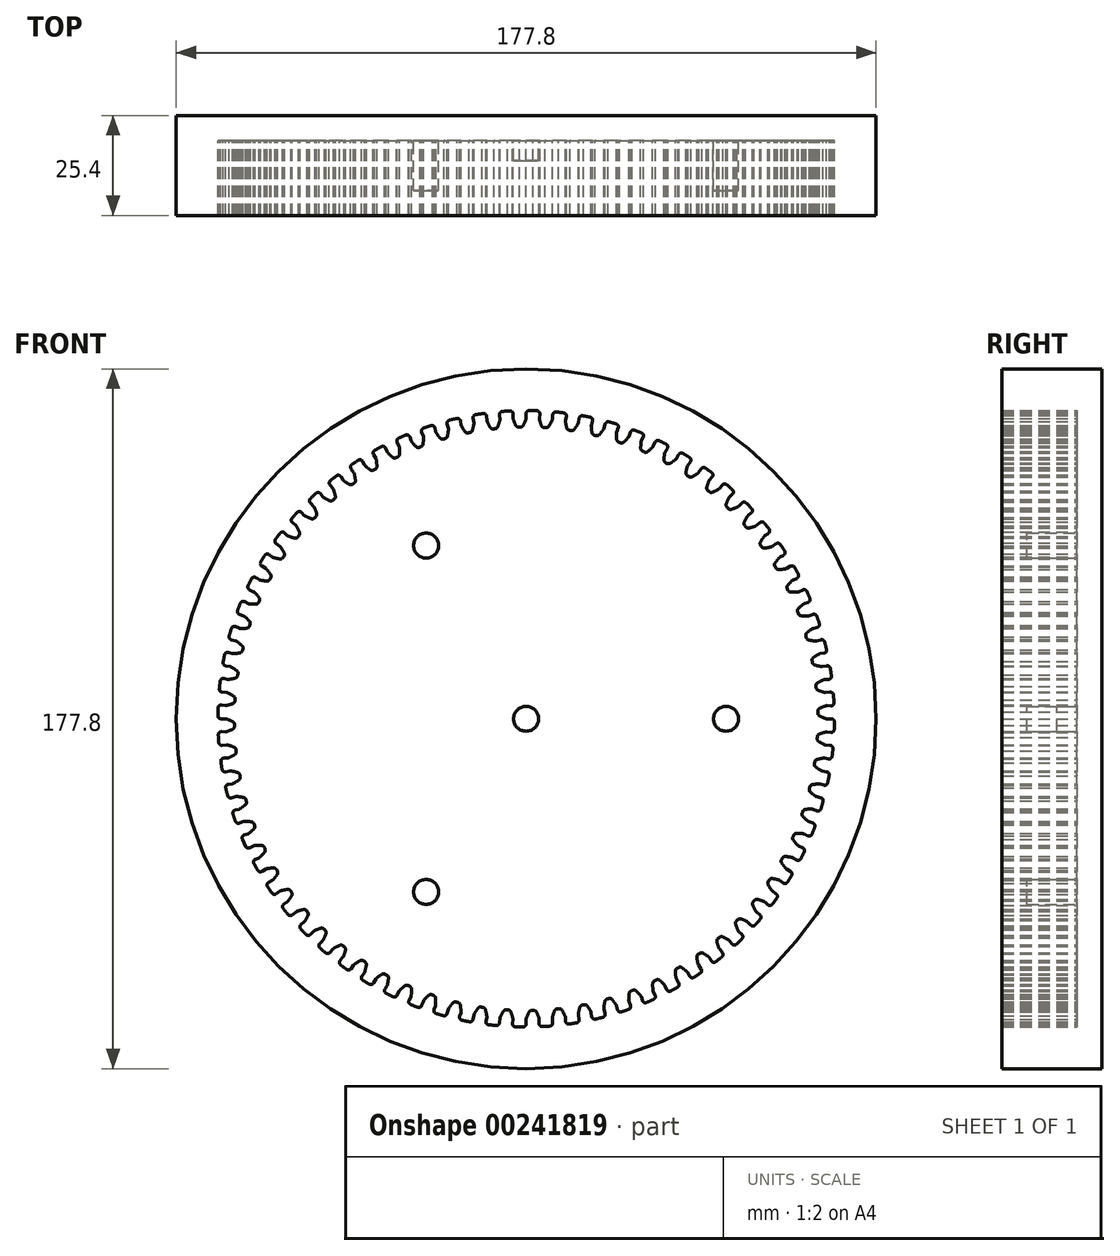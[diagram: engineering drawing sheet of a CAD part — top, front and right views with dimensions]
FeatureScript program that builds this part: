
annotation { "Feature Type Name" : "Feature", "Feature Type Description" : "" }
export const myFeature = defineFeature(function(context is Context, id is Id, definition is map)
    precondition{}
    {
        {
            var Q0;
            Q0=qCreatedBy(makeId("Front.planeOp"),FACE);
            var sketch = newSketch(context, id + "F0", { "sketchPlane" : qUnion([Q0])});
            skArc(sketch, "E0", {"start": v(-4.1, 78.2) * mm, "mid": v(-5.07, 78.15) * mm, "end": v(-6.03, 78.08) * mm});
            skArc(sketch, "E1.MirrorCS", {"start": v(-0.05, 76.06) * mm, "mid": v(-0.38, 75.29) * mm, "end": v(-0.74, 74.53) * mm});
            skLineSegment(sketch, "E2.MirrorCS", {"start": v(0, 76.35) * mm, "end": v(0, 77.53) * mm});
            skLineSegment(sketch, "E3.MirrorCS", {"start": v(-1.45, 74.1) * mm, "end": v(-1.7, 74.1) * mm});
            skLineSegment(sketch, "E4.MirrorCS", {"start": v(-1.97, 74.1) * mm, "end": v(-1.7, 74.1) * mm});
            skArc(sketch, "E5.MirrorCS", {"start": v(-3.28, 76.13) * mm, "mid": v(-2.99, 75.34) * mm, "end": v(-2.66, 74.57) * mm});
            skLineSegment(sketch, "E6.MirrorCS", {"start": v(-3.32, 76.42) * mm, "end": v(-3.28, 77.39) * mm});
            skPoint(sketch, "E7.end.orphan", {"position": v(-1.7, 78.3) * mm});
            skPoint(sketch, "E7.start.orphan", {"position": v(-0.96, 78.31) * mm});
            skPoint(sketch, "E8.MirrorCS.start.orphan", {"position": v(-2.45, 78.28) * mm});
            skPoint(sketch, "E9.orphan", {"position": v(-3.32, 76.13) * mm});
            skPoint(sketch, "E10.MirrorCS.end.orphan", {"position": v(-3.2, 73.49) * mm});
            skPoint(sketch, "E11.end.orphan", {"position": v(0, 73.56) * mm});
            skPoint(sketch, "E12.orphan", {"position": v(-3.2, 78.91) * mm});
            skPoint(sketch, "E13.orphan", {"position": v(0, 78.84) * mm});
            skPoint(sketch, "E14.start.orphan", {"position": v(0, 76.2) * mm});
            skPoint(sketch, "E15.visualSharp", {"position": v(-2.45, 74.12) * mm});
            skArc(sketch, "E15.filletArc", {"start": v(-2.48, 74.18) * mm, "mid": v(-2.44, 74.14) * mm, "end": v(-2.4, 74.12) * mm});
            skArc(sketch, "E16.filletArc", {"start": v(-0.05, 76.06) * mm, "mid": v(-0.01, 76.2) * mm, "end": v(0, 76.35) * mm});
            skPoint(sketch, "E17.visualSharp", {"position": v(-3.32, 76.27) * mm});
            skArc(sketch, "E17.filletArc", {"start": v(-3.32, 76.42) * mm, "mid": v(-3.3, 76.27) * mm, "end": v(-3.28, 76.13) * mm});
            skPoint(sketch, "E18.visualSharp", {"position": v(-0.96, 74.09) * mm});
            skArc(sketch, "E18.filletArc", {"start": v(-1.45, 74.1) * mm, "mid": v(-1.03, 74.21) * mm, "end": v(-0.74, 74.53) * mm});
            skArc(sketch, "E19.filletArc", {"start": v(-2.66, 74.57) * mm, "mid": v(-2.38, 74.24) * mm, "end": v(-1.97, 74.1) * mm});
            skPoint(sketch, "E20.visualSharp", {"position": v(-3.24, 78.25) * mm});
            skArc(sketch, "E20.filletArc", {"start": v(-3.28, 77.39) * mm, "mid": v(-3.5, 77.98) * mm, "end": v(-4.1, 78.2) * mm});
            skPoint(sketch, "E21.visualSharp", {"position": v(0, 78.32) * mm});
            skArc(sketch, "E21.filletArc", {"start": v(0.8, 78.31) * mm, "mid": v(0.23, 78.08) * mm, "end": v(0, 77.53) * mm});
            skCircle(sketch, "E22", {"center": v(0, 0) * mm, "radius": 88.9 * mm});
            skArc(sketch, "E23.1.0", {"start": v(-10, 76.8) * mm, "mid": v(-10.3, 77.38) * mm, "end": v(-10.9, 77.55) * mm});
            skLineSegment(sketch, "E23.1.1", {"start": v(-9.97, 75.84) * mm, "end": v(-10, 76.8) * mm});
            skArc(sketch, "E23.1.2", {"start": v(-9.97, 75.84) * mm, "mid": v(-9.94, 75.7) * mm, "end": v(-9.9, 75.55) * mm});
            skArc(sketch, "E23.1.3", {"start": v(-9.9, 75.55) * mm, "mid": v(-9.54, 74.8) * mm, "end": v(-9.15, 74.06) * mm});
            skArc(sketch, "E23.1.4", {"start": v(-9.15, 74.06) * mm, "mid": v(-8.84, 73.75) * mm, "end": v(-8.42, 73.65) * mm});
            skLineSegment(sketch, "E23.1.5", {"start": v(-8.42, 73.65) * mm, "end": v(-8.16, 73.67) * mm});
            skLineSegment(sketch, "E23.1.6", {"start": v(-7.9, 73.69) * mm, "end": v(-8.16, 73.67) * mm});
            skArc(sketch, "E23.1.7", {"start": v(-7.9, 73.69) * mm, "mid": v(-7.5, 73.84) * mm, "end": v(-7.23, 74.18) * mm});
            skArc(sketch, "E23.1.8", {"start": v(-6.68, 75.77) * mm, "mid": v(-6.94, 74.97) * mm, "end": v(-7.23, 74.18) * mm});
            skArc(sketch, "E23.1.9", {"start": v(-6.68, 75.77) * mm, "mid": v(-6.66, 75.9) * mm, "end": v(-6.65, 76.06) * mm});
            skLineSegment(sketch, "E23.1.10", {"start": v(-6.65, 76.06) * mm, "end": v(-6.76, 77.23) * mm});
            skArc(sketch, "E23.1.11", {"start": v(-6.03, 78.08) * mm, "mid": v(-6.57, 77.8) * mm, "end": v(-6.76, 77.23) * mm});
            skArc(sketch, "E23.2.0", {"start": v(-16.66, 75.64) * mm, "mid": v(-17, 76.19) * mm, "end": v(-17.62, 76.3) * mm});
            skLineSegment(sketch, "E23.2.1", {"start": v(-16.54, 74.68) * mm, "end": v(-16.66, 75.64) * mm});
            skArc(sketch, "E23.2.2", {"start": v(-16.54, 74.68) * mm, "mid": v(-16.5, 74.54) * mm, "end": v(-16.45, 74.4) * mm});
            skArc(sketch, "E23.2.3", {"start": v(-16.45, 74.4) * mm, "mid": v(-16.02, 73.68) * mm, "end": v(-15.57, 72.98) * mm});
            skArc(sketch, "E23.2.4", {"start": v(-15.57, 72.98) * mm, "mid": v(-15.24, 72.7) * mm, "end": v(-14.8, 72.64) * mm});
            skLineSegment(sketch, "E23.2.5", {"start": v(-14.8, 72.64) * mm, "end": v(-14.55, 72.68) * mm});
            skLineSegment(sketch, "E23.2.6", {"start": v(-14.3, 72.72) * mm, "end": v(-14.55, 72.68) * mm});
            skArc(sketch, "E23.2.7", {"start": v(-14.3, 72.72) * mm, "mid": v(-13.9, 72.9) * mm, "end": v(-13.67, 73.27) * mm});
            skArc(sketch, "E23.2.8", {"start": v(-13.26, 74.9) * mm, "mid": v(-13.45, 74.08) * mm, "end": v(-13.67, 73.27) * mm});
            skArc(sketch, "E23.2.9", {"start": v(-13.26, 74.9) * mm, "mid": v(-13.25, 75.04) * mm, "end": v(-13.26, 75.19) * mm});
            skLineSegment(sketch, "E23.2.10", {"start": v(-13.26, 75.19) * mm, "end": v(-13.46, 76.35) * mm});
            skArc(sketch, "E23.2.11", {"start": v(-12.82, 77.26) * mm, "mid": v(-13.33, 76.94) * mm, "end": v(-13.46, 76.35) * mm});
            skArc(sketch, "E23.3.0", {"start": v(-23.2, 73.9) * mm, "mid": v(-23.57, 74.42) * mm, "end": v(-24.2, 74.48) * mm});
            skLineSegment(sketch, "E23.3.1", {"start": v(-22.98, 72.96) * mm, "end": v(-23.2, 73.9) * mm});
            skArc(sketch, "E23.3.2", {"start": v(-22.98, 72.96) * mm, "mid": v(-22.94, 72.82) * mm, "end": v(-22.87, 72.69) * mm});
            skArc(sketch, "E23.3.3", {"start": v(-22.87, 72.69) * mm, "mid": v(-22.38, 72) * mm, "end": v(-21.87, 71.34) * mm});
            skArc(sketch, "E23.3.4", {"start": v(-21.87, 71.34) * mm, "mid": v(-21.52, 71.1) * mm, "end": v(-21.08, 71.07) * mm});
            skLineSegment(sketch, "E23.3.5", {"start": v(-21.08, 71.07) * mm, "end": v(-20.83, 71.13) * mm});
            skLineSegment(sketch, "E23.3.6", {"start": v(-20.58, 71.2) * mm, "end": v(-20.83, 71.13) * mm});
            skArc(sketch, "E23.3.7", {"start": v(-20.58, 71.2) * mm, "mid": v(-20.2, 71.42) * mm, "end": v(-20, 71.8) * mm});
            skArc(sketch, "E23.3.8", {"start": v(-19.74, 73.45) * mm, "mid": v(-19.85, 72.62) * mm, "end": v(-20, 71.8) * mm});
            skArc(sketch, "E23.3.9", {"start": v(-19.74, 73.45) * mm, "mid": v(-19.74, 73.6) * mm, "end": v(-19.76, 73.75) * mm});
            skLineSegment(sketch, "E23.3.10", {"start": v(-19.76, 73.75) * mm, "end": v(-20.07, 74.88) * mm});
            skArc(sketch, "E23.3.11", {"start": v(-19.5, 75.85) * mm, "mid": v(-19.98, 75.48) * mm, "end": v(-20.07, 74.88) * mm});
            skArc(sketch, "E23.4.0", {"start": v(-29.55, 71.6) * mm, "mid": v(-29.97, 72.08) * mm, "end": v(-30.6, 72.09) * mm});
            skLineSegment(sketch, "E23.4.1", {"start": v(-29.25, 70.68) * mm, "end": v(-29.55, 71.6) * mm});
            skArc(sketch, "E23.4.2", {"start": v(-29.25, 70.68) * mm, "mid": v(-29.2, 70.54) * mm, "end": v(-29.12, 70.42) * mm});
            skArc(sketch, "E23.4.3", {"start": v(-29.12, 70.42) * mm, "mid": v(-28.57, 69.78) * mm, "end": v(-28, 69.17) * mm});
            skArc(sketch, "E23.4.4", {"start": v(-28, 69.17) * mm, "mid": v(-27.63, 68.95) * mm, "end": v(-27.2, 68.96) * mm});
            skLineSegment(sketch, "E23.4.5", {"start": v(-27.2, 68.96) * mm, "end": v(-26.95, 69.05) * mm});
            skLineSegment(sketch, "E23.4.6", {"start": v(-26.7, 69.13) * mm, "end": v(-26.95, 69.05) * mm});
            skArc(sketch, "E23.4.7", {"start": v(-26.7, 69.13) * mm, "mid": v(-26.35, 69.38) * mm, "end": v(-26.18, 69.78) * mm});
            skArc(sketch, "E23.4.8", {"start": v(-26.07, 71.45) * mm, "mid": v(-26.1, 70.62) * mm, "end": v(-26.18, 69.78) * mm});
            skArc(sketch, "E23.4.9", {"start": v(-26.07, 71.45) * mm, "mid": v(-26.08, 71.6) * mm, "end": v(-26.11, 71.74) * mm});
            skLineSegment(sketch, "E23.4.10", {"start": v(-26.11, 71.74) * mm, "end": v(-26.52, 72.85) * mm});
            skArc(sketch, "E23.4.11", {"start": v(-26.04, 73.86) * mm, "mid": v(-26.49, 73.46) * mm, "end": v(-26.52, 72.85) * mm});
            skArc(sketch, "E23.5.0", {"start": v(-35.67, 68.75) * mm, "mid": v(-36.14, 69.2) * mm, "end": v(-36.77, 69.15) * mm});
            skLineSegment(sketch, "E23.5.1", {"start": v(-35.3, 67.86) * mm, "end": v(-35.67, 68.75) * mm});
            skArc(sketch, "E23.5.2", {"start": v(-35.3, 67.86) * mm, "mid": v(-35.23, 67.73) * mm, "end": v(-35.14, 67.61) * mm});
            skArc(sketch, "E23.5.3", {"start": v(-35.14, 67.61) * mm, "mid": v(-34.55, 67.02) * mm, "end": v(-33.93, 66.46) * mm});
            skArc(sketch, "E23.5.4", {"start": v(-33.93, 66.46) * mm, "mid": v(-33.53, 66.28) * mm, "end": v(-33.1, 66.33) * mm});
            skLineSegment(sketch, "E23.5.5", {"start": v(-33.1, 66.33) * mm, "end": v(-32.86, 66.43) * mm});
            skLineSegment(sketch, "E23.5.6", {"start": v(-32.63, 66.54) * mm, "end": v(-32.86, 66.43) * mm});
            skArc(sketch, "E23.5.7", {"start": v(-32.63, 66.54) * mm, "mid": v(-32.3, 66.82) * mm, "end": v(-32.16, 67.24) * mm});
            skArc(sketch, "E23.5.8", {"start": v(-32.2, 68.91) * mm, "mid": v(-32.16, 68.07) * mm, "end": v(-32.16, 67.24) * mm});
            skArc(sketch, "E23.5.9", {"start": v(-32.2, 68.91) * mm, "mid": v(-32.22, 69.06) * mm, "end": v(-32.27, 69.2) * mm});
            skLineSegment(sketch, "E23.5.10", {"start": v(-32.27, 69.2) * mm, "end": v(-32.76, 70.26) * mm});
            skArc(sketch, "E23.5.11", {"start": v(-32.38, 71.31) * mm, "mid": v(-32.79, 70.87) * mm, "end": v(-32.76, 70.26) * mm});
            skArc(sketch, "E23.6.0", {"start": v(-41.53, 65.38) * mm, "mid": v(-42.03, 65.78) * mm, "end": v(-42.66, 65.68) * mm});
            skLineSegment(sketch, "E23.6.1", {"start": v(-41.08, 64.52) * mm, "end": v(-41.53, 65.38) * mm});
            skArc(sketch, "E23.6.2", {"start": v(-41.08, 64.52) * mm, "mid": v(-41, 64.4) * mm, "end": v(-40.9, 64.3) * mm});
            skArc(sketch, "E23.6.3", {"start": v(-40.9, 64.3) * mm, "mid": v(-40.26, 63.76) * mm, "end": v(-39.6, 63.25) * mm});
            skArc(sketch, "E23.6.4", {"start": v(-39.6, 63.25) * mm, "mid": v(-39.18, 63.1) * mm, "end": v(-38.76, 63.2) * mm});
            skLineSegment(sketch, "E23.6.5", {"start": v(-38.76, 63.2) * mm, "end": v(-38.53, 63.32) * mm});
            skLineSegment(sketch, "E23.6.6", {"start": v(-38.3, 63.44) * mm, "end": v(-38.53, 63.32) * mm});
            skArc(sketch, "E23.6.7", {"start": v(-38.3, 63.44) * mm, "mid": v(-38, 63.75) * mm, "end": v(-37.9, 64.18) * mm});
            skArc(sketch, "E23.6.8", {"start": v(-38.08, 65.84) * mm, "mid": v(-37.97, 65.01) * mm, "end": v(-37.9, 64.18) * mm});
            skArc(sketch, "E23.6.9", {"start": v(-38.08, 65.84) * mm, "mid": v(-38.11, 65.99) * mm, "end": v(-38.17, 66.12) * mm});
            skLineSegment(sketch, "E23.6.10", {"start": v(-38.17, 66.12) * mm, "end": v(-38.76, 67.14) * mm});
            skArc(sketch, "E23.6.11", {"start": v(-38.47, 68.22) * mm, "mid": v(-38.84, 67.74) * mm, "end": v(-38.76, 67.14) * mm});
            skArc(sketch, "E23.7.0", {"start": v(-47.07, 61.51) * mm, "mid": v(-47.6, 61.87) * mm, "end": v(-48.22, 61.71) * mm});
            skLineSegment(sketch, "E23.7.1", {"start": v(-46.55, 60.7) * mm, "end": v(-47.07, 61.51) * mm});
            skArc(sketch, "E23.7.2", {"start": v(-46.55, 60.7) * mm, "mid": v(-46.46, 60.58) * mm, "end": v(-46.35, 60.48) * mm});
            skArc(sketch, "E23.7.3", {"start": v(-46.35, 60.48) * mm, "mid": v(-45.66, 60) * mm, "end": v(-44.95, 59.56) * mm});
            skArc(sketch, "E23.7.4", {"start": v(-44.95, 59.56) * mm, "mid": v(-44.53, 59.45) * mm, "end": v(-44.12, 59.58) * mm});
            skLineSegment(sketch, "E23.7.5", {"start": v(-44.12, 59.58) * mm, "end": v(-43.9, 59.72) * mm});
            skLineSegment(sketch, "E23.7.6", {"start": v(-43.69, 59.86) * mm, "end": v(-43.9, 59.72) * mm});
            skArc(sketch, "E23.7.7", {"start": v(-43.69, 59.86) * mm, "mid": v(-43.4, 60.2) * mm, "end": v(-43.35, 60.63) * mm});
            skArc(sketch, "E23.7.8", {"start": v(-43.67, 62.27) * mm, "mid": v(-43.5, 61.46) * mm, "end": v(-43.35, 60.63) * mm});
            skArc(sketch, "E23.7.9", {"start": v(-43.67, 62.27) * mm, "mid": v(-43.72, 62.41) * mm, "end": v(-43.8, 62.54) * mm});
            skLineSegment(sketch, "E23.7.10", {"start": v(-43.8, 62.54) * mm, "end": v(-44.47, 63.5) * mm});
            skArc(sketch, "E23.7.11", {"start": v(-44.27, 64.6) * mm, "mid": v(-44.6, 64.1) * mm, "end": v(-44.47, 63.5) * mm});
            skArc(sketch, "E23.8.0", {"start": v(-52.25, 57.18) * mm, "mid": v(-52.81, 57.48) * mm, "end": v(-53.41, 57.27) * mm});
            skLineSegment(sketch, "E23.8.1", {"start": v(-51.66, 56.4) * mm, "end": v(-52.25, 57.18) * mm});
            skArc(sketch, "E23.8.2", {"start": v(-51.66, 56.4) * mm, "mid": v(-51.56, 56.3) * mm, "end": v(-51.44, 56.21) * mm});
            skArc(sketch, "E23.8.3", {"start": v(-51.44, 56.21) * mm, "mid": v(-50.72, 55.8) * mm, "end": v(-49.97, 55.42) * mm});
            skArc(sketch, "E23.8.4", {"start": v(-49.97, 55.42) * mm, "mid": v(-49.54, 55.34) * mm, "end": v(-49.14, 55.5) * mm});
            skLineSegment(sketch, "E23.8.5", {"start": v(-49.14, 55.5) * mm, "end": v(-48.94, 55.66) * mm});
            skLineSegment(sketch, "E23.8.6", {"start": v(-48.74, 55.83) * mm, "end": v(-48.94, 55.66) * mm});
            skArc(sketch, "E23.8.7", {"start": v(-48.74, 55.83) * mm, "mid": v(-48.5, 56.19) * mm, "end": v(-48.47, 56.62) * mm});
            skArc(sketch, "E23.8.8", {"start": v(-48.93, 58.23) * mm, "mid": v(-48.68, 57.43) * mm, "end": v(-48.47, 56.62) * mm});
            skArc(sketch, "E23.8.9", {"start": v(-48.93, 58.23) * mm, "mid": v(-49, 58.36) * mm, "end": v(-49.08, 58.49) * mm});
            skLineSegment(sketch, "E23.8.10", {"start": v(-49.08, 58.49) * mm, "end": v(-49.83, 59.39) * mm});
            skArc(sketch, "E23.8.11", {"start": v(-49.73, 60.5) * mm, "mid": v(-50.01, 59.97) * mm, "end": v(-49.83, 59.39) * mm});
            skArc(sketch, "E23.9.0", {"start": v(-57.04, 52.4) * mm, "mid": v(-57.62, 52.66) * mm, "end": v(-58.2, 52.4) * mm});
            skLineSegment(sketch, "E23.9.1", {"start": v(-56.38, 51.7) * mm, "end": v(-57.04, 52.4) * mm});
            skArc(sketch, "E23.9.2", {"start": v(-56.38, 51.7) * mm, "mid": v(-56.27, 51.6) * mm, "end": v(-56.15, 51.52) * mm});
            skArc(sketch, "E23.9.3", {"start": v(-56.15, 51.52) * mm, "mid": v(-55.39, 51.17) * mm, "end": v(-54.61, 50.85) * mm});
            skArc(sketch, "E23.9.4", {"start": v(-54.61, 50.85) * mm, "mid": v(-54.18, 50.81) * mm, "end": v(-53.8, 51.01) * mm});
            skLineSegment(sketch, "E23.9.5", {"start": v(-53.8, 51.01) * mm, "end": v(-53.6, 51.19) * mm});
            skLineSegment(sketch, "E23.9.6", {"start": v(-53.42, 51.37) * mm, "end": v(-53.6, 51.19) * mm});
            skArc(sketch, "E23.9.7", {"start": v(-53.42, 51.37) * mm, "mid": v(-53.2, 51.75) * mm, "end": v(-53.22, 52.18) * mm});
            skArc(sketch, "E23.9.8", {"start": v(-53.82, 53.74) * mm, "mid": v(-53.5, 52.97) * mm, "end": v(-53.22, 52.18) * mm});
            skArc(sketch, "E23.9.9", {"start": v(-53.82, 53.74) * mm, "mid": v(-53.9, 53.87) * mm, "end": v(-53.99, 53.99) * mm});
            skLineSegment(sketch, "E23.9.10", {"start": v(-53.99, 53.99) * mm, "end": v(-54.82, 54.82) * mm});
            skArc(sketch, "E23.9.11", {"start": v(-54.81, 55.94) * mm, "mid": v(-55.05, 55.38) * mm, "end": v(-54.82, 54.82) * mm});
            skArc(sketch, "E23.10.0", {"start": v(-61.39, 47.24) * mm, "mid": v(-62, 47.44) * mm, "end": v(-62.55, 47.13) * mm});
            skLineSegment(sketch, "E23.10.1", {"start": v(-60.67, 46.58) * mm, "end": v(-61.39, 47.24) * mm});
            skArc(sketch, "E23.10.2", {"start": v(-60.67, 46.58) * mm, "mid": v(-60.56, 46.5) * mm, "end": v(-60.42, 46.43) * mm});
            skArc(sketch, "E23.10.3", {"start": v(-60.42, 46.43) * mm, "mid": v(-59.64, 46.14) * mm, "end": v(-58.84, 45.9) * mm});
            skArc(sketch, "E23.10.4", {"start": v(-58.84, 45.9) * mm, "mid": v(-58.4, 45.9) * mm, "end": v(-58.03, 46.13) * mm});
            skLineSegment(sketch, "E23.10.5", {"start": v(-58.03, 46.13) * mm, "end": v(-57.86, 46.32) * mm});
            skLineSegment(sketch, "E23.10.6", {"start": v(-57.7, 46.52) * mm, "end": v(-57.86, 46.32) * mm});
            skArc(sketch, "E23.10.7", {"start": v(-57.7, 46.52) * mm, "mid": v(-57.51, 46.91) * mm, "end": v(-57.57, 47.34) * mm});
            skArc(sketch, "E23.10.8", {"start": v(-58.3, 48.85) * mm, "mid": v(-57.92, 48.1) * mm, "end": v(-57.57, 47.34) * mm});
            skArc(sketch, "E23.10.9", {"start": v(-58.3, 48.85) * mm, "mid": v(-58.38, 48.97) * mm, "end": v(-58.49, 49.08) * mm});
            skLineSegment(sketch, "E23.10.10", {"start": v(-58.49, 49.08) * mm, "end": v(-59.39, 49.83) * mm});
            skArc(sketch, "E23.10.11", {"start": v(-59.48, 50.95) * mm, "mid": v(-59.67, 50.37) * mm, "end": v(-59.39, 49.83) * mm});
            skArc(sketch, "E23.11.0", {"start": v(-65.27, 41.7) * mm, "mid": v(-65.9, 41.86) * mm, "end": v(-66.42, 41.5) * mm});
            skLineSegment(sketch, "E23.11.1", {"start": v(-64.5, 41.12) * mm, "end": v(-65.27, 41.7) * mm});
            skArc(sketch, "E23.11.2", {"start": v(-64.5, 41.12) * mm, "mid": v(-64.38, 41.04) * mm, "end": v(-64.24, 40.98) * mm});
            skArc(sketch, "E23.11.3", {"start": v(-64.24, 40.98) * mm, "mid": v(-63.43, 40.77) * mm, "end": v(-62.61, 40.6) * mm});
            skArc(sketch, "E23.11.4", {"start": v(-62.61, 40.6) * mm, "mid": v(-62.18, 40.63) * mm, "end": v(-61.83, 40.9) * mm});
            skLineSegment(sketch, "E23.11.5", {"start": v(-61.83, 40.9) * mm, "end": v(-61.68, 41.1) * mm});
            skLineSegment(sketch, "E23.11.6", {"start": v(-61.53, 41.31) * mm, "end": v(-61.68, 41.1) * mm});
            skArc(sketch, "E23.11.7", {"start": v(-61.53, 41.31) * mm, "mid": v(-61.38, 41.72) * mm, "end": v(-61.47, 42.15) * mm});
            skArc(sketch, "E23.11.8", {"start": v(-62.34, 43.58) * mm, "mid": v(-61.89, 42.87) * mm, "end": v(-61.47, 42.15) * mm});
            skArc(sketch, "E23.11.9", {"start": v(-62.34, 43.58) * mm, "mid": v(-62.43, 43.7) * mm, "end": v(-62.54, 43.8) * mm});
            skLineSegment(sketch, "E23.11.10", {"start": v(-62.54, 43.8) * mm, "end": v(-63.5, 44.47) * mm});
            skArc(sketch, "E23.11.11", {"start": v(-63.7, 45.57) * mm, "mid": v(-63.83, 44.98) * mm, "end": v(-63.5, 44.47) * mm});
            skArc(sketch, "E23.12.0", {"start": v(-68.66, 35.86) * mm, "mid": v(-69.29, 35.95) * mm, "end": v(-69.78, 35.55) * mm});
            skLineSegment(sketch, "E23.12.1", {"start": v(-67.84, 35.34) * mm, "end": v(-68.66, 35.86) * mm});
            skArc(sketch, "E23.12.2", {"start": v(-67.84, 35.34) * mm, "mid": v(-67.7, 35.27) * mm, "end": v(-67.57, 35.23) * mm});
            skArc(sketch, "E23.12.3", {"start": v(-67.57, 35.23) * mm, "mid": v(-66.74, 35.09) * mm, "end": v(-65.91, 34.98) * mm});
            skArc(sketch, "E23.12.4", {"start": v(-65.91, 34.98) * mm, "mid": v(-65.48, 35.06) * mm, "end": v(-65.16, 35.35) * mm});
            skLineSegment(sketch, "E23.12.5", {"start": v(-65.16, 35.35) * mm, "end": v(-65.03, 35.57) * mm});
            skLineSegment(sketch, "E23.12.6", {"start": v(-64.9, 35.8) * mm, "end": v(-65.03, 35.57) * mm});
            skArc(sketch, "E23.12.7", {"start": v(-64.9, 35.8) * mm, "mid": v(-64.78, 36.21) * mm, "end": v(-64.91, 36.63) * mm});
            skArc(sketch, "E23.12.8", {"start": v(-65.9, 37.98) * mm, "mid": v(-65.4, 37.32) * mm, "end": v(-64.91, 36.63) * mm});
            skArc(sketch, "E23.12.9", {"start": v(-65.9, 37.98) * mm, "mid": v(-66, 38.09) * mm, "end": v(-66.12, 38.17) * mm});
            skLineSegment(sketch, "E23.12.10", {"start": v(-66.12, 38.17) * mm, "end": v(-67.14, 38.76) * mm});
            skArc(sketch, "E23.12.11", {"start": v(-67.42, 39.85) * mm, "mid": v(-67.5, 39.24) * mm, "end": v(-67.14, 38.76) * mm});
            skArc(sketch, "E23.13.0", {"start": v(-71.52, 29.74) * mm, "mid": v(-72.16, 29.78) * mm, "end": v(-72.62, 29.33) * mm});
            skLineSegment(sketch, "E23.13.1", {"start": v(-70.66, 29.3) * mm, "end": v(-71.52, 29.74) * mm});
            skArc(sketch, "E23.13.2", {"start": v(-70.66, 29.3) * mm, "mid": v(-70.53, 29.23) * mm, "end": v(-70.38, 29.2) * mm});
            skArc(sketch, "E23.13.3", {"start": v(-70.38, 29.2) * mm, "mid": v(-69.55, 29.14) * mm, "end": v(-68.71, 29.1) * mm});
            skArc(sketch, "E23.13.4", {"start": v(-68.71, 29.1) * mm, "mid": v(-68.3, 29.22) * mm, "end": v(-68, 29.54) * mm});
            skLineSegment(sketch, "E23.13.5", {"start": v(-68, 29.54) * mm, "end": v(-67.88, 29.77) * mm});
            skLineSegment(sketch, "E23.13.6", {"start": v(-67.77, 30) * mm, "end": v(-67.88, 29.77) * mm});
            skArc(sketch, "E23.13.7", {"start": v(-67.77, 30) * mm, "mid": v(-67.7, 30.43) * mm, "end": v(-67.86, 30.83) * mm});
            skArc(sketch, "E23.13.8", {"start": v(-68.96, 32.1) * mm, "mid": v(-68.4, 31.48) * mm, "end": v(-67.86, 30.83) * mm});
            skArc(sketch, "E23.13.9", {"start": v(-68.96, 32.1) * mm, "mid": v(-69.07, 32.2) * mm, "end": v(-69.2, 32.27) * mm});
            skLineSegment(sketch, "E23.13.10", {"start": v(-69.2, 32.27) * mm, "end": v(-70.26, 32.76) * mm});
            skArc(sketch, "E23.13.11", {"start": v(-70.64, 33.82) * mm, "mid": v(-70.67, 33.21) * mm, "end": v(-70.26, 32.76) * mm});
            skArc(sketch, "E23.14.0", {"start": v(-73.84, 23.4) * mm, "mid": v(-74.48, 23.38) * mm, "end": v(-74.9, 22.9) * mm});
            skLineSegment(sketch, "E23.14.1", {"start": v(-72.95, 23.02) * mm, "end": v(-73.84, 23.4) * mm});
            skArc(sketch, "E23.14.2", {"start": v(-72.95, 23.02) * mm, "mid": v(-72.8, 22.98) * mm, "end": v(-72.66, 22.96) * mm});
            skArc(sketch, "E23.14.3", {"start": v(-72.66, 22.96) * mm, "mid": v(-71.82, 22.96) * mm, "end": v(-70.99, 23) * mm});
            skArc(sketch, "E23.14.4", {"start": v(-70.99, 23) * mm, "mid": v(-70.58, 23.15) * mm, "end": v(-70.31, 23.5) * mm});
            skLineSegment(sketch, "E23.14.5", {"start": v(-70.31, 23.5) * mm, "end": v(-70.21, 23.74) * mm});
            skLineSegment(sketch, "E23.14.6", {"start": v(-70.12, 23.98) * mm, "end": v(-70.21, 23.74) * mm});
            skArc(sketch, "E23.14.7", {"start": v(-70.12, 23.98) * mm, "mid": v(-70.09, 24.41) * mm, "end": v(-70.29, 24.8) * mm});
            skArc(sketch, "E23.14.8", {"start": v(-71.5, 25.96) * mm, "mid": v(-70.88, 25.4) * mm, "end": v(-70.29, 24.8) * mm});
            skArc(sketch, "E23.14.9", {"start": v(-71.5, 25.96) * mm, "mid": v(-71.61, 26.05) * mm, "end": v(-71.74, 26.11) * mm});
            skLineSegment(sketch, "E23.14.10", {"start": v(-71.74, 26.11) * mm, "end": v(-72.85, 26.52) * mm});
            skArc(sketch, "E23.14.11", {"start": v(-73.32, 27.53) * mm, "mid": v(-73.3, 26.93) * mm, "end": v(-72.85, 26.52) * mm});
            skArc(sketch, "E23.15.0", {"start": v(-75.6, 16.87) * mm, "mid": v(-76.23, 16.8) * mm, "end": v(-76.6, 16.28) * mm});
            skLineSegment(sketch, "E23.15.1", {"start": v(-74.67, 16.57) * mm, "end": v(-75.6, 16.87) * mm});
            skArc(sketch, "E23.15.2", {"start": v(-74.67, 16.57) * mm, "mid": v(-74.53, 16.54) * mm, "end": v(-74.38, 16.54) * mm});
            skArc(sketch, "E23.15.3", {"start": v(-74.38, 16.54) * mm, "mid": v(-73.55, 16.62) * mm, "end": v(-72.72, 16.73) * mm});
            skArc(sketch, "E23.15.4", {"start": v(-72.72, 16.73) * mm, "mid": v(-72.33, 16.91) * mm, "end": v(-72.1, 17.28) * mm});
            skLineSegment(sketch, "E23.15.5", {"start": v(-72.1, 17.28) * mm, "end": v(-72.02, 17.53) * mm});
            skLineSegment(sketch, "E23.15.6", {"start": v(-71.95, 17.78) * mm, "end": v(-72.02, 17.53) * mm});
            skArc(sketch, "E23.15.7", {"start": v(-71.95, 17.78) * mm, "mid": v(-71.95, 18.21) * mm, "end": v(-72.18, 18.58) * mm});
            skArc(sketch, "E23.15.8", {"start": v(-73.48, 19.63) * mm, "mid": v(-72.82, 19.12) * mm, "end": v(-72.18, 18.58) * mm});
            skArc(sketch, "E23.15.9", {"start": v(-73.48, 19.63) * mm, "mid": v(-73.6, 19.7) * mm, "end": v(-73.75, 19.76) * mm});
            skLineSegment(sketch, "E23.15.10", {"start": v(-73.75, 19.76) * mm, "end": v(-74.88, 20.07) * mm});
            skArc(sketch, "E23.15.11", {"start": v(-75.44, 21.04) * mm, "mid": v(-75.36, 20.44) * mm, "end": v(-74.88, 20.07) * mm});
            skArc(sketch, "E23.16.0", {"start": v(-76.78, 10.21) * mm, "mid": v(-77.4, 10.09) * mm, "end": v(-77.73, 9.54) * mm});
            skLineSegment(sketch, "E23.16.1", {"start": v(-75.84, 10) * mm, "end": v(-76.78, 10.21) * mm});
            skArc(sketch, "E23.16.2", {"start": v(-75.84, 10) * mm, "mid": v(-75.69, 9.98) * mm, "end": v(-75.54, 10) * mm});
            skArc(sketch, "E23.16.3", {"start": v(-75.54, 10) * mm, "mid": v(-74.72, 10.14) * mm, "end": v(-73.9, 10.33) * mm});
            skArc(sketch, "E23.16.4", {"start": v(-73.9, 10.33) * mm, "mid": v(-73.53, 10.55) * mm, "end": v(-73.32, 10.93) * mm});
            skLineSegment(sketch, "E23.16.5", {"start": v(-73.32, 10.93) * mm, "end": v(-73.27, 11.18) * mm});
            skLineSegment(sketch, "E23.16.6", {"start": v(-73.22, 11.44) * mm, "end": v(-73.27, 11.18) * mm});
            skArc(sketch, "E23.16.7", {"start": v(-73.22, 11.44) * mm, "mid": v(-73.26, 11.87) * mm, "end": v(-73.53, 12.22) * mm});
            skArc(sketch, "E23.16.8", {"start": v(-74.91, 13.15) * mm, "mid": v(-74.2, 12.7) * mm, "end": v(-73.53, 12.22) * mm});
            skArc(sketch, "E23.16.9", {"start": v(-74.91, 13.15) * mm, "mid": v(-75.05, 13.22) * mm, "end": v(-75.19, 13.26) * mm});
            skLineSegment(sketch, "E23.16.10", {"start": v(-75.19, 13.26) * mm, "end": v(-76.35, 13.46) * mm});
            skArc(sketch, "E23.16.11", {"start": v(-76.98, 14.38) * mm, "mid": v(-76.86, 13.79) * mm, "end": v(-76.35, 13.46) * mm});
            skArc(sketch, "E23.17.0", {"start": v(-77.38, 3.48) * mm, "mid": v(-78, 3.3) * mm, "end": v(-78.27, 2.73) * mm});
            skLineSegment(sketch, "E23.17.1", {"start": v(-76.42, 3.36) * mm, "end": v(-77.38, 3.48) * mm});
            skArc(sketch, "E23.17.2", {"start": v(-76.42, 3.36) * mm, "mid": v(-76.27, 3.35) * mm, "end": v(-76.13, 3.37) * mm});
            skArc(sketch, "E23.17.3", {"start": v(-76.13, 3.37) * mm, "mid": v(-75.32, 3.6) * mm, "end": v(-74.52, 3.85) * mm});
            skArc(sketch, "E23.17.4", {"start": v(-74.52, 3.85) * mm, "mid": v(-74.16, 4.1) * mm, "end": v(-74, 4.5) * mm});
            skLineSegment(sketch, "E23.17.5", {"start": v(-74, 4.5) * mm, "end": v(-73.97, 4.76) * mm});
            skLineSegment(sketch, "E23.17.6", {"start": v(-73.94, 5.01) * mm, "end": v(-73.97, 4.76) * mm});
            skArc(sketch, "E23.17.7", {"start": v(-73.94, 5.01) * mm, "mid": v(-74.02, 5.44) * mm, "end": v(-74.31, 5.76) * mm});
            skArc(sketch, "E23.17.8", {"start": v(-75.77, 6.57) * mm, "mid": v(-75.03, 6.18) * mm, "end": v(-74.31, 5.76) * mm});
            skArc(sketch, "E23.17.9", {"start": v(-75.77, 6.57) * mm, "mid": v(-75.91, 6.63) * mm, "end": v(-76.06, 6.65) * mm});
            skLineSegment(sketch, "E23.17.10", {"start": v(-76.06, 6.65) * mm, "end": v(-77.23, 6.76) * mm});
            skArc(sketch, "E23.17.11", {"start": v(-77.95, 7.62) * mm, "mid": v(-77.77, 7.04) * mm, "end": v(-77.23, 6.76) * mm});
            skArc(sketch, "E23.18.0", {"start": v(-77.39, -3.28) * mm, "mid": v(-77.98, -3.5) * mm, "end": v(-78.2, -4.1) * mm});
            skLineSegment(sketch, "E23.18.1", {"start": v(-76.42, -3.32) * mm, "end": v(-77.39, -3.28) * mm});
            skArc(sketch, "E23.18.2", {"start": v(-76.42, -3.32) * mm, "mid": v(-76.27, -3.3) * mm, "end": v(-76.13, -3.28) * mm});
            skArc(sketch, "E23.18.3", {"start": v(-76.13, -3.28) * mm, "mid": v(-75.34, -2.99) * mm, "end": v(-74.57, -2.66) * mm});
            skArc(sketch, "E23.18.4", {"start": v(-74.57, -2.66) * mm, "mid": v(-74.24, -2.38) * mm, "end": v(-74.1, -1.97) * mm});
            skLineSegment(sketch, "E23.18.5", {"start": v(-74.1, -1.97) * mm, "end": v(-74.1, -1.7) * mm});
            skLineSegment(sketch, "E23.18.6", {"start": v(-74.1, -1.45) * mm, "end": v(-74.1, -1.7) * mm});
            skArc(sketch, "E23.18.7", {"start": v(-74.1, -1.45) * mm, "mid": v(-74.21, -1.03) * mm, "end": v(-74.53, -0.74) * mm});
            skArc(sketch, "E23.18.8", {"start": v(-76.06, -0.05) * mm, "mid": v(-75.29, -0.38) * mm, "end": v(-74.53, -0.74) * mm});
            skArc(sketch, "E23.18.9", {"start": v(-76.06, -0.05) * mm, "mid": v(-76.2, -0.01) * mm, "end": v(-76.35, 0) * mm});
            skLineSegment(sketch, "E23.18.10", {"start": v(-76.35, 0) * mm, "end": v(-77.53, 0) * mm});
            skArc(sketch, "E23.18.11", {"start": v(-78.31, 0.8) * mm, "mid": v(-78.08, 0.23) * mm, "end": v(-77.53, 0) * mm});
            skArc(sketch, "E23.19.0", {"start": v(-76.8, -10) * mm, "mid": v(-77.38, -10.3) * mm, "end": v(-77.55, -10.9) * mm});
            skLineSegment(sketch, "E23.19.1", {"start": v(-75.84, -9.97) * mm, "end": v(-76.8, -10) * mm});
            skArc(sketch, "E23.19.2", {"start": v(-75.84, -9.97) * mm, "mid": v(-75.7, -9.94) * mm, "end": v(-75.55, -9.9) * mm});
            skArc(sketch, "E23.19.3", {"start": v(-75.55, -9.9) * mm, "mid": v(-74.8, -9.54) * mm, "end": v(-74.06, -9.15) * mm});
            skArc(sketch, "E23.19.4", {"start": v(-74.06, -9.15) * mm, "mid": v(-73.75, -8.84) * mm, "end": v(-73.65, -8.42) * mm});
            skLineSegment(sketch, "E23.19.5", {"start": v(-73.65, -8.42) * mm, "end": v(-73.67, -8.16) * mm});
            skLineSegment(sketch, "E23.19.6", {"start": v(-73.69, -7.9) * mm, "end": v(-73.67, -8.16) * mm});
            skArc(sketch, "E23.19.7", {"start": v(-73.69, -7.9) * mm, "mid": v(-73.84, -7.5) * mm, "end": v(-74.18, -7.23) * mm});
            skArc(sketch, "E23.19.8", {"start": v(-75.77, -6.68) * mm, "mid": v(-74.97, -6.94) * mm, "end": v(-74.18, -7.23) * mm});
            skArc(sketch, "E23.19.9", {"start": v(-75.77, -6.68) * mm, "mid": v(-75.9, -6.66) * mm, "end": v(-76.06, -6.65) * mm});
            skLineSegment(sketch, "E23.19.10", {"start": v(-76.06, -6.65) * mm, "end": v(-77.23, -6.76) * mm});
            skArc(sketch, "E23.19.11", {"start": v(-78.08, -6.03) * mm, "mid": v(-77.8, -6.57) * mm, "end": v(-77.23, -6.76) * mm});
            skArc(sketch, "E23.20.0", {"start": v(-75.64, -16.66) * mm, "mid": v(-76.19, -17) * mm, "end": v(-76.3, -17.62) * mm});
            skLineSegment(sketch, "E23.20.1", {"start": v(-74.68, -16.54) * mm, "end": v(-75.64, -16.66) * mm});
            skArc(sketch, "E23.20.2", {"start": v(-74.68, -16.54) * mm, "mid": v(-74.54, -16.5) * mm, "end": v(-74.4, -16.45) * mm});
            skArc(sketch, "E23.20.3", {"start": v(-74.4, -16.45) * mm, "mid": v(-73.68, -16.02) * mm, "end": v(-72.98, -15.57) * mm});
            skArc(sketch, "E23.20.4", {"start": v(-72.98, -15.57) * mm, "mid": v(-72.7, -15.24) * mm, "end": v(-72.64, -14.8) * mm});
            skLineSegment(sketch, "E23.20.5", {"start": v(-72.64, -14.8) * mm, "end": v(-72.68, -14.55) * mm});
            skLineSegment(sketch, "E23.20.6", {"start": v(-72.72, -14.3) * mm, "end": v(-72.68, -14.55) * mm});
            skArc(sketch, "E23.20.7", {"start": v(-72.72, -14.3) * mm, "mid": v(-72.9, -13.9) * mm, "end": v(-73.27, -13.67) * mm});
            skArc(sketch, "E23.20.8", {"start": v(-74.9, -13.26) * mm, "mid": v(-74.08, -13.45) * mm, "end": v(-73.27, -13.67) * mm});
            skArc(sketch, "E23.20.9", {"start": v(-74.9, -13.26) * mm, "mid": v(-75.04, -13.25) * mm, "end": v(-75.19, -13.26) * mm});
            skLineSegment(sketch, "E23.20.10", {"start": v(-75.19, -13.26) * mm, "end": v(-76.35, -13.46) * mm});
            skArc(sketch, "E23.20.11", {"start": v(-77.26, -12.82) * mm, "mid": v(-76.94, -13.33) * mm, "end": v(-76.35, -13.46) * mm});
            skArc(sketch, "E23.21.0", {"start": v(-73.9, -23.2) * mm, "mid": v(-74.42, -23.57) * mm, "end": v(-74.48, -24.2) * mm});
            skLineSegment(sketch, "E23.21.1", {"start": v(-72.96, -22.98) * mm, "end": v(-73.9, -23.2) * mm});
            skArc(sketch, "E23.21.2", {"start": v(-72.96, -22.98) * mm, "mid": v(-72.82, -22.94) * mm, "end": v(-72.69, -22.87) * mm});
            skArc(sketch, "E23.21.3", {"start": v(-72.69, -22.87) * mm, "mid": v(-72, -22.38) * mm, "end": v(-71.34, -21.87) * mm});
            skArc(sketch, "E23.21.4", {"start": v(-71.34, -21.87) * mm, "mid": v(-71.1, -21.52) * mm, "end": v(-71.07, -21.08) * mm});
            skLineSegment(sketch, "E23.21.5", {"start": v(-71.07, -21.08) * mm, "end": v(-71.13, -20.83) * mm});
            skLineSegment(sketch, "E23.21.6", {"start": v(-71.2, -20.58) * mm, "end": v(-71.13, -20.83) * mm});
            skArc(sketch, "E23.21.7", {"start": v(-71.2, -20.58) * mm, "mid": v(-71.42, -20.2) * mm, "end": v(-71.8, -20) * mm});
            skArc(sketch, "E23.21.8", {"start": v(-73.45, -19.74) * mm, "mid": v(-72.62, -19.85) * mm, "end": v(-71.8, -20) * mm});
            skArc(sketch, "E23.21.9", {"start": v(-73.45, -19.74) * mm, "mid": v(-73.6, -19.74) * mm, "end": v(-73.75, -19.76) * mm});
            skLineSegment(sketch, "E23.21.10", {"start": v(-73.75, -19.76) * mm, "end": v(-74.88, -20.07) * mm});
            skArc(sketch, "E23.21.11", {"start": v(-75.85, -19.5) * mm, "mid": v(-75.48, -19.98) * mm, "end": v(-74.88, -20.07) * mm});
            skArc(sketch, "E23.22.0", {"start": v(-71.6, -29.55) * mm, "mid": v(-72.08, -29.97) * mm, "end": v(-72.09, -30.6) * mm});
            skLineSegment(sketch, "E23.22.1", {"start": v(-70.68, -29.25) * mm, "end": v(-71.6, -29.55) * mm});
            skArc(sketch, "E23.22.2", {"start": v(-70.68, -29.25) * mm, "mid": v(-70.54, -29.2) * mm, "end": v(-70.42, -29.12) * mm});
            skArc(sketch, "E23.22.3", {"start": v(-70.42, -29.12) * mm, "mid": v(-69.78, -28.57) * mm, "end": v(-69.17, -28) * mm});
            skArc(sketch, "E23.22.4", {"start": v(-69.17, -28) * mm, "mid": v(-68.95, -27.63) * mm, "end": v(-68.96, -27.2) * mm});
            skLineSegment(sketch, "E23.22.5", {"start": v(-68.96, -27.2) * mm, "end": v(-69.05, -26.95) * mm});
            skLineSegment(sketch, "E23.22.6", {"start": v(-69.13, -26.7) * mm, "end": v(-69.05, -26.95) * mm});
            skArc(sketch, "E23.22.7", {"start": v(-69.13, -26.7) * mm, "mid": v(-69.38, -26.35) * mm, "end": v(-69.78, -26.18) * mm});
            skArc(sketch, "E23.22.8", {"start": v(-71.45, -26.07) * mm, "mid": v(-70.62, -26.1) * mm, "end": v(-69.78, -26.18) * mm});
            skArc(sketch, "E23.22.9", {"start": v(-71.45, -26.07) * mm, "mid": v(-71.6, -26.08) * mm, "end": v(-71.74, -26.11) * mm});
            skLineSegment(sketch, "E23.22.10", {"start": v(-71.74, -26.11) * mm, "end": v(-72.85, -26.52) * mm});
            skArc(sketch, "E23.22.11", {"start": v(-73.86, -26.04) * mm, "mid": v(-73.46, -26.49) * mm, "end": v(-72.85, -26.52) * mm});
            skArc(sketch, "E23.23.0", {"start": v(-68.75, -35.67) * mm, "mid": v(-69.2, -36.14) * mm, "end": v(-69.15, -36.77) * mm});
            skLineSegment(sketch, "E23.23.1", {"start": v(-67.86, -35.3) * mm, "end": v(-68.75, -35.67) * mm});
            skArc(sketch, "E23.23.2", {"start": v(-67.86, -35.3) * mm, "mid": v(-67.73, -35.23) * mm, "end": v(-67.61, -35.14) * mm});
            skArc(sketch, "E23.23.3", {"start": v(-67.61, -35.14) * mm, "mid": v(-67.02, -34.55) * mm, "end": v(-66.46, -33.93) * mm});
            skArc(sketch, "E23.23.4", {"start": v(-66.46, -33.93) * mm, "mid": v(-66.28, -33.53) * mm, "end": v(-66.33, -33.1) * mm});
            skLineSegment(sketch, "E23.23.5", {"start": v(-66.33, -33.1) * mm, "end": v(-66.43, -32.86) * mm});
            skLineSegment(sketch, "E23.23.6", {"start": v(-66.54, -32.63) * mm, "end": v(-66.43, -32.86) * mm});
            skArc(sketch, "E23.23.7", {"start": v(-66.54, -32.63) * mm, "mid": v(-66.82, -32.3) * mm, "end": v(-67.24, -32.16) * mm});
            skArc(sketch, "E23.23.8", {"start": v(-68.91, -32.2) * mm, "mid": v(-68.07, -32.16) * mm, "end": v(-67.24, -32.16) * mm});
            skArc(sketch, "E23.23.9", {"start": v(-68.91, -32.2) * mm, "mid": v(-69.06, -32.22) * mm, "end": v(-69.2, -32.27) * mm});
            skLineSegment(sketch, "E23.23.10", {"start": v(-69.2, -32.27) * mm, "end": v(-70.26, -32.76) * mm});
            skArc(sketch, "E23.23.11", {"start": v(-71.31, -32.38) * mm, "mid": v(-70.87, -32.79) * mm, "end": v(-70.26, -32.76) * mm});
            skArc(sketch, "E23.24.0", {"start": v(-65.38, -41.53) * mm, "mid": v(-65.78, -42.03) * mm, "end": v(-65.68, -42.66) * mm});
            skLineSegment(sketch, "E23.24.1", {"start": v(-64.52, -41.08) * mm, "end": v(-65.38, -41.53) * mm});
            skArc(sketch, "E23.24.2", {"start": v(-64.52, -41.08) * mm, "mid": v(-64.4, -41) * mm, "end": v(-64.3, -40.9) * mm});
            skArc(sketch, "E23.24.3", {"start": v(-64.3, -40.9) * mm, "mid": v(-63.76, -40.26) * mm, "end": v(-63.25, -39.6) * mm});
            skArc(sketch, "E23.24.4", {"start": v(-63.25, -39.6) * mm, "mid": v(-63.1, -39.18) * mm, "end": v(-63.2, -38.76) * mm});
            skLineSegment(sketch, "E23.24.5", {"start": v(-63.2, -38.76) * mm, "end": v(-63.32, -38.53) * mm});
            skLineSegment(sketch, "E23.24.6", {"start": v(-63.44, -38.3) * mm, "end": v(-63.32, -38.53) * mm});
            skArc(sketch, "E23.24.7", {"start": v(-63.44, -38.3) * mm, "mid": v(-63.75, -38) * mm, "end": v(-64.18, -37.9) * mm});
            skArc(sketch, "E23.24.8", {"start": v(-65.84, -38.08) * mm, "mid": v(-65.01, -37.97) * mm, "end": v(-64.18, -37.9) * mm});
            skArc(sketch, "E23.24.9", {"start": v(-65.84, -38.08) * mm, "mid": v(-65.99, -38.11) * mm, "end": v(-66.12, -38.17) * mm});
            skLineSegment(sketch, "E23.24.10", {"start": v(-66.12, -38.17) * mm, "end": v(-67.14, -38.76) * mm});
            skArc(sketch, "E23.24.11", {"start": v(-68.22, -38.47) * mm, "mid": v(-67.74, -38.84) * mm, "end": v(-67.14, -38.76) * mm});
            skArc(sketch, "E23.25.0", {"start": v(-61.51, -47.07) * mm, "mid": v(-61.87, -47.6) * mm, "end": v(-61.71, -48.22) * mm});
            skLineSegment(sketch, "E23.25.1", {"start": v(-60.7, -46.55) * mm, "end": v(-61.51, -47.07) * mm});
            skArc(sketch, "E23.25.2", {"start": v(-60.7, -46.55) * mm, "mid": v(-60.58, -46.46) * mm, "end": v(-60.48, -46.35) * mm});
            skArc(sketch, "E23.25.3", {"start": v(-60.48, -46.35) * mm, "mid": v(-60, -45.66) * mm, "end": v(-59.56, -44.95) * mm});
            skArc(sketch, "E23.25.4", {"start": v(-59.56, -44.95) * mm, "mid": v(-59.45, -44.53) * mm, "end": v(-59.58, -44.12) * mm});
            skLineSegment(sketch, "E23.25.5", {"start": v(-59.58, -44.12) * mm, "end": v(-59.72, -43.9) * mm});
            skLineSegment(sketch, "E23.25.6", {"start": v(-59.86, -43.69) * mm, "end": v(-59.72, -43.9) * mm});
            skArc(sketch, "E23.25.7", {"start": v(-59.86, -43.69) * mm, "mid": v(-60.2, -43.4) * mm, "end": v(-60.63, -43.35) * mm});
            skArc(sketch, "E23.25.8", {"start": v(-62.27, -43.67) * mm, "mid": v(-61.46, -43.5) * mm, "end": v(-60.63, -43.35) * mm});
            skArc(sketch, "E23.25.9", {"start": v(-62.27, -43.67) * mm, "mid": v(-62.41, -43.72) * mm, "end": v(-62.54, -43.8) * mm});
            skLineSegment(sketch, "E23.25.10", {"start": v(-62.54, -43.8) * mm, "end": v(-63.5, -44.47) * mm});
            skArc(sketch, "E23.25.11", {"start": v(-64.6, -44.27) * mm, "mid": v(-64.1, -44.6) * mm, "end": v(-63.5, -44.47) * mm});
            skArc(sketch, "E23.26.0", {"start": v(-57.18, -52.25) * mm, "mid": v(-57.48, -52.81) * mm, "end": v(-57.27, -53.41) * mm});
            skLineSegment(sketch, "E23.26.1", {"start": v(-56.4, -51.66) * mm, "end": v(-57.18, -52.25) * mm});
            skArc(sketch, "E23.26.2", {"start": v(-56.4, -51.66) * mm, "mid": v(-56.3, -51.56) * mm, "end": v(-56.21, -51.44) * mm});
            skArc(sketch, "E23.26.3", {"start": v(-56.21, -51.44) * mm, "mid": v(-55.8, -50.72) * mm, "end": v(-55.42, -49.97) * mm});
            skArc(sketch, "E23.26.4", {"start": v(-55.42, -49.97) * mm, "mid": v(-55.34, -49.54) * mm, "end": v(-55.5, -49.14) * mm});
            skLineSegment(sketch, "E23.26.5", {"start": v(-55.5, -49.14) * mm, "end": v(-55.66, -48.94) * mm});
            skLineSegment(sketch, "E23.26.6", {"start": v(-55.83, -48.74) * mm, "end": v(-55.66, -48.94) * mm});
            skArc(sketch, "E23.26.7", {"start": v(-55.83, -48.74) * mm, "mid": v(-56.19, -48.5) * mm, "end": v(-56.62, -48.47) * mm});
            skArc(sketch, "E23.26.8", {"start": v(-58.23, -48.93) * mm, "mid": v(-57.43, -48.68) * mm, "end": v(-56.62, -48.47) * mm});
            skArc(sketch, "E23.26.9", {"start": v(-58.23, -48.93) * mm, "mid": v(-58.36, -49) * mm, "end": v(-58.49, -49.08) * mm});
            skLineSegment(sketch, "E23.26.10", {"start": v(-58.49, -49.08) * mm, "end": v(-59.39, -49.83) * mm});
            skArc(sketch, "E23.26.11", {"start": v(-60.5, -49.73) * mm, "mid": v(-59.97, -50.01) * mm, "end": v(-59.39, -49.83) * mm});
            skArc(sketch, "E23.27.0", {"start": v(-52.4, -57.04) * mm, "mid": v(-52.66, -57.62) * mm, "end": v(-52.4, -58.2) * mm});
            skLineSegment(sketch, "E23.27.1", {"start": v(-51.7, -56.38) * mm, "end": v(-52.4, -57.04) * mm});
            skArc(sketch, "E23.27.2", {"start": v(-51.7, -56.38) * mm, "mid": v(-51.6, -56.27) * mm, "end": v(-51.52, -56.15) * mm});
            skArc(sketch, "E23.27.3", {"start": v(-51.52, -56.15) * mm, "mid": v(-51.17, -55.39) * mm, "end": v(-50.85, -54.61) * mm});
            skArc(sketch, "E23.27.4", {"start": v(-50.85, -54.61) * mm, "mid": v(-50.81, -54.18) * mm, "end": v(-51.01, -53.8) * mm});
            skLineSegment(sketch, "E23.27.5", {"start": v(-51.01, -53.8) * mm, "end": v(-51.19, -53.6) * mm});
            skLineSegment(sketch, "E23.27.6", {"start": v(-51.37, -53.42) * mm, "end": v(-51.19, -53.6) * mm});
            skArc(sketch, "E23.27.7", {"start": v(-51.37, -53.42) * mm, "mid": v(-51.75, -53.2) * mm, "end": v(-52.18, -53.22) * mm});
            skArc(sketch, "E23.27.8", {"start": v(-53.74, -53.82) * mm, "mid": v(-52.97, -53.5) * mm, "end": v(-52.18, -53.22) * mm});
            skArc(sketch, "E23.27.9", {"start": v(-53.74, -53.82) * mm, "mid": v(-53.87, -53.9) * mm, "end": v(-53.99, -53.99) * mm});
            skLineSegment(sketch, "E23.27.10", {"start": v(-53.99, -53.99) * mm, "end": v(-54.82, -54.82) * mm});
            skArc(sketch, "E23.27.11", {"start": v(-55.94, -54.81) * mm, "mid": v(-55.38, -55.05) * mm, "end": v(-54.82, -54.82) * mm});
            skArc(sketch, "E23.28.0", {"start": v(-47.24, -61.39) * mm, "mid": v(-47.44, -62) * mm, "end": v(-47.13, -62.55) * mm});
            skLineSegment(sketch, "E23.28.1", {"start": v(-46.58, -60.67) * mm, "end": v(-47.24, -61.39) * mm});
            skArc(sketch, "E23.28.2", {"start": v(-46.58, -60.67) * mm, "mid": v(-46.5, -60.56) * mm, "end": v(-46.43, -60.42) * mm});
            skArc(sketch, "E23.28.3", {"start": v(-46.43, -60.42) * mm, "mid": v(-46.14, -59.64) * mm, "end": v(-45.9, -58.84) * mm});
            skArc(sketch, "E23.28.4", {"start": v(-45.9, -58.84) * mm, "mid": v(-45.9, -58.4) * mm, "end": v(-46.13, -58.03) * mm});
            skLineSegment(sketch, "E23.28.5", {"start": v(-46.13, -58.03) * mm, "end": v(-46.32, -57.86) * mm});
            skLineSegment(sketch, "E23.28.6", {"start": v(-46.52, -57.7) * mm, "end": v(-46.32, -57.86) * mm});
            skArc(sketch, "E23.28.7", {"start": v(-46.52, -57.7) * mm, "mid": v(-46.91, -57.51) * mm, "end": v(-47.34, -57.57) * mm});
            skArc(sketch, "E23.28.8", {"start": v(-48.85, -58.3) * mm, "mid": v(-48.1, -57.92) * mm, "end": v(-47.34, -57.57) * mm});
            skArc(sketch, "E23.28.9", {"start": v(-48.85, -58.3) * mm, "mid": v(-48.97, -58.38) * mm, "end": v(-49.08, -58.49) * mm});
            skLineSegment(sketch, "E23.28.10", {"start": v(-49.08, -58.49) * mm, "end": v(-49.83, -59.39) * mm});
            skArc(sketch, "E23.28.11", {"start": v(-50.95, -59.48) * mm, "mid": v(-50.37, -59.67) * mm, "end": v(-49.83, -59.39) * mm});
            skArc(sketch, "E23.29.0", {"start": v(-41.7, -65.27) * mm, "mid": v(-41.86, -65.9) * mm, "end": v(-41.5, -66.42) * mm});
            skLineSegment(sketch, "E23.29.1", {"start": v(-41.12, -64.5) * mm, "end": v(-41.7, -65.27) * mm});
            skArc(sketch, "E23.29.2", {"start": v(-41.12, -64.5) * mm, "mid": v(-41.04, -64.38) * mm, "end": v(-40.98, -64.24) * mm});
            skArc(sketch, "E23.29.3", {"start": v(-40.98, -64.24) * mm, "mid": v(-40.77, -63.43) * mm, "end": v(-40.6, -62.61) * mm});
            skArc(sketch, "E23.29.4", {"start": v(-40.6, -62.61) * mm, "mid": v(-40.63, -62.18) * mm, "end": v(-40.9, -61.83) * mm});
            skLineSegment(sketch, "E23.29.5", {"start": v(-40.9, -61.83) * mm, "end": v(-41.1, -61.68) * mm});
            skLineSegment(sketch, "E23.29.6", {"start": v(-41.31, -61.53) * mm, "end": v(-41.1, -61.68) * mm});
            skArc(sketch, "E23.29.7", {"start": v(-41.31, -61.53) * mm, "mid": v(-41.72, -61.38) * mm, "end": v(-42.15, -61.47) * mm});
            skArc(sketch, "E23.29.8", {"start": v(-43.58, -62.34) * mm, "mid": v(-42.87, -61.89) * mm, "end": v(-42.15, -61.47) * mm});
            skArc(sketch, "E23.29.9", {"start": v(-43.58, -62.34) * mm, "mid": v(-43.7, -62.43) * mm, "end": v(-43.8, -62.54) * mm});
            skLineSegment(sketch, "E23.29.10", {"start": v(-43.8, -62.54) * mm, "end": v(-44.47, -63.5) * mm});
            skArc(sketch, "E23.29.11", {"start": v(-45.57, -63.7) * mm, "mid": v(-44.98, -63.83) * mm, "end": v(-44.47, -63.5) * mm});
            skArc(sketch, "E23.30.0", {"start": v(-35.86, -68.66) * mm, "mid": v(-35.95, -69.29) * mm, "end": v(-35.55, -69.78) * mm});
            skLineSegment(sketch, "E23.30.1", {"start": v(-35.34, -67.84) * mm, "end": v(-35.86, -68.66) * mm});
            skArc(sketch, "E23.30.2", {"start": v(-35.34, -67.84) * mm, "mid": v(-35.27, -67.7) * mm, "end": v(-35.23, -67.57) * mm});
            skArc(sketch, "E23.30.3", {"start": v(-35.23, -67.57) * mm, "mid": v(-35.09, -66.74) * mm, "end": v(-34.98, -65.91) * mm});
            skArc(sketch, "E23.30.4", {"start": v(-34.98, -65.91) * mm, "mid": v(-35.06, -65.48) * mm, "end": v(-35.35, -65.16) * mm});
            skLineSegment(sketch, "E23.30.5", {"start": v(-35.35, -65.16) * mm, "end": v(-35.57, -65.03) * mm});
            skLineSegment(sketch, "E23.30.6", {"start": v(-35.8, -64.9) * mm, "end": v(-35.57, -65.03) * mm});
            skArc(sketch, "E23.30.7", {"start": v(-35.8, -64.9) * mm, "mid": v(-36.21, -64.78) * mm, "end": v(-36.63, -64.91) * mm});
            skArc(sketch, "E23.30.8", {"start": v(-37.98, -65.9) * mm, "mid": v(-37.32, -65.4) * mm, "end": v(-36.63, -64.91) * mm});
            skArc(sketch, "E23.30.9", {"start": v(-37.98, -65.9) * mm, "mid": v(-38.09, -66) * mm, "end": v(-38.17, -66.12) * mm});
            skLineSegment(sketch, "E23.30.10", {"start": v(-38.17, -66.12) * mm, "end": v(-38.76, -67.14) * mm});
            skArc(sketch, "E23.30.11", {"start": v(-39.85, -67.42) * mm, "mid": v(-39.24, -67.5) * mm, "end": v(-38.76, -67.14) * mm});
            skArc(sketch, "E23.31.0", {"start": v(-29.74, -71.52) * mm, "mid": v(-29.78, -72.16) * mm, "end": v(-29.33, -72.62) * mm});
            skLineSegment(sketch, "E23.31.1", {"start": v(-29.3, -70.66) * mm, "end": v(-29.74, -71.52) * mm});
            skArc(sketch, "E23.31.2", {"start": v(-29.3, -70.66) * mm, "mid": v(-29.23, -70.53) * mm, "end": v(-29.2, -70.38) * mm});
            skArc(sketch, "E23.31.3", {"start": v(-29.2, -70.38) * mm, "mid": v(-29.14, -69.55) * mm, "end": v(-29.1, -68.71) * mm});
            skArc(sketch, "E23.31.4", {"start": v(-29.1, -68.71) * mm, "mid": v(-29.22, -68.3) * mm, "end": v(-29.54, -68) * mm});
            skLineSegment(sketch, "E23.31.5", {"start": v(-29.54, -68) * mm, "end": v(-29.77, -67.88) * mm});
            skLineSegment(sketch, "E23.31.6", {"start": v(-30, -67.77) * mm, "end": v(-29.77, -67.88) * mm});
            skArc(sketch, "E23.31.7", {"start": v(-30, -67.77) * mm, "mid": v(-30.43, -67.7) * mm, "end": v(-30.83, -67.86) * mm});
            skArc(sketch, "E23.31.8", {"start": v(-32.1, -68.96) * mm, "mid": v(-31.48, -68.4) * mm, "end": v(-30.83, -67.86) * mm});
            skArc(sketch, "E23.31.9", {"start": v(-32.1, -68.96) * mm, "mid": v(-32.2, -69.07) * mm, "end": v(-32.27, -69.2) * mm});
            skLineSegment(sketch, "E23.31.10", {"start": v(-32.27, -69.2) * mm, "end": v(-32.76, -70.26) * mm});
            skArc(sketch, "E23.31.11", {"start": v(-33.82, -70.64) * mm, "mid": v(-33.21, -70.67) * mm, "end": v(-32.76, -70.26) * mm});
            skArc(sketch, "E23.32.0", {"start": v(-23.4, -73.84) * mm, "mid": v(-23.38, -74.48) * mm, "end": v(-22.9, -74.9) * mm});
            skLineSegment(sketch, "E23.32.1", {"start": v(-23.02, -72.95) * mm, "end": v(-23.4, -73.84) * mm});
            skArc(sketch, "E23.32.2", {"start": v(-23.02, -72.95) * mm, "mid": v(-22.98, -72.8) * mm, "end": v(-22.96, -72.66) * mm});
            skArc(sketch, "E23.32.3", {"start": v(-22.96, -72.66) * mm, "mid": v(-22.96, -71.82) * mm, "end": v(-23, -70.99) * mm});
            skArc(sketch, "E23.32.4", {"start": v(-23, -70.99) * mm, "mid": v(-23.15, -70.58) * mm, "end": v(-23.5, -70.31) * mm});
            skLineSegment(sketch, "E23.32.5", {"start": v(-23.5, -70.31) * mm, "end": v(-23.74, -70.21) * mm});
            skLineSegment(sketch, "E23.32.6", {"start": v(-23.98, -70.12) * mm, "end": v(-23.74, -70.21) * mm});
            skArc(sketch, "E23.32.7", {"start": v(-23.98, -70.12) * mm, "mid": v(-24.41, -70.09) * mm, "end": v(-24.8, -70.29) * mm});
            skArc(sketch, "E23.32.8", {"start": v(-25.96, -71.5) * mm, "mid": v(-25.4, -70.88) * mm, "end": v(-24.8, -70.29) * mm});
            skArc(sketch, "E23.32.9", {"start": v(-25.96, -71.5) * mm, "mid": v(-26.05, -71.61) * mm, "end": v(-26.11, -71.74) * mm});
            skLineSegment(sketch, "E23.32.10", {"start": v(-26.11, -71.74) * mm, "end": v(-26.52, -72.85) * mm});
            skArc(sketch, "E23.32.11", {"start": v(-27.53, -73.32) * mm, "mid": v(-26.93, -73.3) * mm, "end": v(-26.52, -72.85) * mm});
            skArc(sketch, "E23.33.0", {"start": v(-16.87, -75.6) * mm, "mid": v(-16.8, -76.23) * mm, "end": v(-16.28, -76.6) * mm});
            skLineSegment(sketch, "E23.33.1", {"start": v(-16.57, -74.67) * mm, "end": v(-16.87, -75.6) * mm});
            skArc(sketch, "E23.33.2", {"start": v(-16.57, -74.67) * mm, "mid": v(-16.54, -74.53) * mm, "end": v(-16.54, -74.38) * mm});
            skArc(sketch, "E23.33.3", {"start": v(-16.54, -74.38) * mm, "mid": v(-16.62, -73.55) * mm, "end": v(-16.73, -72.72) * mm});
            skArc(sketch, "E23.33.4", {"start": v(-16.73, -72.72) * mm, "mid": v(-16.91, -72.33) * mm, "end": v(-17.28, -72.1) * mm});
            skLineSegment(sketch, "E23.33.5", {"start": v(-17.28, -72.1) * mm, "end": v(-17.53, -72.02) * mm});
            skLineSegment(sketch, "E23.33.6", {"start": v(-17.78, -71.95) * mm, "end": v(-17.53, -72.02) * mm});
            skArc(sketch, "E23.33.7", {"start": v(-17.78, -71.95) * mm, "mid": v(-18.21, -71.95) * mm, "end": v(-18.58, -72.18) * mm});
            skArc(sketch, "E23.33.8", {"start": v(-19.63, -73.48) * mm, "mid": v(-19.12, -72.82) * mm, "end": v(-18.58, -72.18) * mm});
            skArc(sketch, "E23.33.9", {"start": v(-19.63, -73.48) * mm, "mid": v(-19.7, -73.6) * mm, "end": v(-19.76, -73.75) * mm});
            skLineSegment(sketch, "E23.33.10", {"start": v(-19.76, -73.75) * mm, "end": v(-20.07, -74.88) * mm});
            skArc(sketch, "E23.33.11", {"start": v(-21.04, -75.44) * mm, "mid": v(-20.44, -75.36) * mm, "end": v(-20.07, -74.88) * mm});
            skArc(sketch, "E23.34.0", {"start": v(-10.21, -76.78) * mm, "mid": v(-10.09, -77.4) * mm, "end": v(-9.54, -77.73) * mm});
            skLineSegment(sketch, "E23.34.1", {"start": v(-10, -75.84) * mm, "end": v(-10.21, -76.78) * mm});
            skArc(sketch, "E23.34.2", {"start": v(-10, -75.84) * mm, "mid": v(-9.98, -75.69) * mm, "end": v(-10, -75.54) * mm});
            skArc(sketch, "E23.34.3", {"start": v(-10, -75.54) * mm, "mid": v(-10.14, -74.72) * mm, "end": v(-10.33, -73.9) * mm});
            skArc(sketch, "E23.34.4", {"start": v(-10.33, -73.9) * mm, "mid": v(-10.55, -73.53) * mm, "end": v(-10.93, -73.32) * mm});
            skLineSegment(sketch, "E23.34.5", {"start": v(-10.93, -73.32) * mm, "end": v(-11.18, -73.27) * mm});
            skLineSegment(sketch, "E23.34.6", {"start": v(-11.44, -73.22) * mm, "end": v(-11.18, -73.27) * mm});
            skArc(sketch, "E23.34.7", {"start": v(-11.44, -73.22) * mm, "mid": v(-11.87, -73.26) * mm, "end": v(-12.22, -73.53) * mm});
            skArc(sketch, "E23.34.8", {"start": v(-13.15, -74.91) * mm, "mid": v(-12.7, -74.2) * mm, "end": v(-12.22, -73.53) * mm});
            skArc(sketch, "E23.34.9", {"start": v(-13.15, -74.91) * mm, "mid": v(-13.22, -75.05) * mm, "end": v(-13.26, -75.19) * mm});
            skLineSegment(sketch, "E23.34.10", {"start": v(-13.26, -75.19) * mm, "end": v(-13.46, -76.35) * mm});
            skArc(sketch, "E23.34.11", {"start": v(-14.38, -76.98) * mm, "mid": v(-13.79, -76.86) * mm, "end": v(-13.46, -76.35) * mm});
            skArc(sketch, "E23.35.0", {"start": v(-3.48, -77.38) * mm, "mid": v(-3.3, -78) * mm, "end": v(-2.73, -78.27) * mm});
            skLineSegment(sketch, "E23.35.1", {"start": v(-3.36, -76.42) * mm, "end": v(-3.48, -77.38) * mm});
            skArc(sketch, "E23.35.2", {"start": v(-3.36, -76.42) * mm, "mid": v(-3.35, -76.27) * mm, "end": v(-3.37, -76.13) * mm});
            skArc(sketch, "E23.35.3", {"start": v(-3.37, -76.13) * mm, "mid": v(-3.6, -75.32) * mm, "end": v(-3.85, -74.52) * mm});
            skArc(sketch, "E23.35.4", {"start": v(-3.85, -74.52) * mm, "mid": v(-4.1, -74.16) * mm, "end": v(-4.5, -74) * mm});
            skLineSegment(sketch, "E23.35.5", {"start": v(-4.5, -74) * mm, "end": v(-4.76, -73.97) * mm});
            skLineSegment(sketch, "E23.35.6", {"start": v(-5.01, -73.94) * mm, "end": v(-4.76, -73.97) * mm});
            skArc(sketch, "E23.35.7", {"start": v(-5.01, -73.94) * mm, "mid": v(-5.44, -74.02) * mm, "end": v(-5.76, -74.31) * mm});
            skArc(sketch, "E23.35.8", {"start": v(-6.57, -75.77) * mm, "mid": v(-6.18, -75.03) * mm, "end": v(-5.76, -74.31) * mm});
            skArc(sketch, "E23.35.9", {"start": v(-6.57, -75.77) * mm, "mid": v(-6.63, -75.91) * mm, "end": v(-6.65, -76.06) * mm});
            skLineSegment(sketch, "E23.35.10", {"start": v(-6.65, -76.06) * mm, "end": v(-6.76, -77.23) * mm});
            skArc(sketch, "E23.35.11", {"start": v(-7.62, -77.95) * mm, "mid": v(-7.04, -77.77) * mm, "end": v(-6.76, -77.23) * mm});
            skArc(sketch, "E23.36.0", {"start": v(3.28, -77.39) * mm, "mid": v(3.5, -77.98) * mm, "end": v(4.1, -78.2) * mm});
            skLineSegment(sketch, "E23.36.1", {"start": v(3.32, -76.42) * mm, "end": v(3.28, -77.39) * mm});
            skArc(sketch, "E23.36.2", {"start": v(3.32, -76.42) * mm, "mid": v(3.3, -76.27) * mm, "end": v(3.28, -76.13) * mm});
            skArc(sketch, "E23.36.3", {"start": v(3.28, -76.13) * mm, "mid": v(2.99, -75.34) * mm, "end": v(2.66, -74.57) * mm});
            skArc(sketch, "E23.36.4", {"start": v(2.66, -74.57) * mm, "mid": v(2.38, -74.24) * mm, "end": v(1.97, -74.1) * mm});
            skLineSegment(sketch, "E23.36.5", {"start": v(1.97, -74.1) * mm, "end": v(1.7, -74.1) * mm});
            skLineSegment(sketch, "E23.36.6", {"start": v(1.45, -74.1) * mm, "end": v(1.7, -74.1) * mm});
            skArc(sketch, "E23.36.7", {"start": v(1.45, -74.1) * mm, "mid": v(1.03, -74.21) * mm, "end": v(0.74, -74.53) * mm});
            skArc(sketch, "E23.36.8", {"start": v(0.05, -76.06) * mm, "mid": v(0.38, -75.29) * mm, "end": v(0.74, -74.53) * mm});
            skArc(sketch, "E23.36.9", {"start": v(0.05, -76.06) * mm, "mid": v(0.01, -76.2) * mm, "end": v(0, -76.35) * mm});
            skLineSegment(sketch, "E23.36.10", {"start": v(0, -76.35) * mm, "end": v(0, -77.53) * mm});
            skArc(sketch, "E23.36.11", {"start": v(-0.8, -78.31) * mm, "mid": v(-0.23, -78.08) * mm, "end": v(0, -77.53) * mm});
            skArc(sketch, "E23.37.0", {"start": v(10, -76.8) * mm, "mid": v(10.3, -77.38) * mm, "end": v(10.9, -77.55) * mm});
            skLineSegment(sketch, "E23.37.1", {"start": v(9.97, -75.84) * mm, "end": v(10, -76.8) * mm});
            skArc(sketch, "E23.37.2", {"start": v(9.97, -75.84) * mm, "mid": v(9.94, -75.7) * mm, "end": v(9.9, -75.55) * mm});
            skArc(sketch, "E23.37.3", {"start": v(9.9, -75.55) * mm, "mid": v(9.54, -74.8) * mm, "end": v(9.15, -74.06) * mm});
            skArc(sketch, "E23.37.4", {"start": v(9.15, -74.06) * mm, "mid": v(8.84, -73.75) * mm, "end": v(8.42, -73.65) * mm});
            skLineSegment(sketch, "E23.37.5", {"start": v(8.42, -73.65) * mm, "end": v(8.16, -73.67) * mm});
            skLineSegment(sketch, "E23.37.6", {"start": v(7.9, -73.69) * mm, "end": v(8.16, -73.67) * mm});
            skArc(sketch, "E23.37.7", {"start": v(7.9, -73.69) * mm, "mid": v(7.5, -73.84) * mm, "end": v(7.23, -74.18) * mm});
            skArc(sketch, "E23.37.8", {"start": v(6.68, -75.77) * mm, "mid": v(6.94, -74.97) * mm, "end": v(7.23, -74.18) * mm});
            skArc(sketch, "E23.37.9", {"start": v(6.68, -75.77) * mm, "mid": v(6.66, -75.9) * mm, "end": v(6.65, -76.06) * mm});
            skLineSegment(sketch, "E23.37.10", {"start": v(6.65, -76.06) * mm, "end": v(6.76, -77.23) * mm});
            skArc(sketch, "E23.37.11", {"start": v(6.03, -78.08) * mm, "mid": v(6.57, -77.8) * mm, "end": v(6.76, -77.23) * mm});
            skArc(sketch, "E23.38.0", {"start": v(16.66, -75.64) * mm, "mid": v(17, -76.19) * mm, "end": v(17.62, -76.3) * mm});
            skLineSegment(sketch, "E23.38.1", {"start": v(16.54, -74.68) * mm, "end": v(16.66, -75.64) * mm});
            skArc(sketch, "E23.38.2", {"start": v(16.54, -74.68) * mm, "mid": v(16.5, -74.54) * mm, "end": v(16.45, -74.4) * mm});
            skArc(sketch, "E23.38.3", {"start": v(16.45, -74.4) * mm, "mid": v(16.02, -73.68) * mm, "end": v(15.57, -72.98) * mm});
            skArc(sketch, "E23.38.4", {"start": v(15.57, -72.98) * mm, "mid": v(15.24, -72.7) * mm, "end": v(14.8, -72.64) * mm});
            skLineSegment(sketch, "E23.38.5", {"start": v(14.8, -72.64) * mm, "end": v(14.55, -72.68) * mm});
            skLineSegment(sketch, "E23.38.6", {"start": v(14.3, -72.72) * mm, "end": v(14.55, -72.68) * mm});
            skArc(sketch, "E23.38.7", {"start": v(14.3, -72.72) * mm, "mid": v(13.9, -72.9) * mm, "end": v(13.67, -73.27) * mm});
            skArc(sketch, "E23.38.8", {"start": v(13.26, -74.9) * mm, "mid": v(13.45, -74.08) * mm, "end": v(13.67, -73.27) * mm});
            skArc(sketch, "E23.38.9", {"start": v(13.26, -74.9) * mm, "mid": v(13.25, -75.04) * mm, "end": v(13.26, -75.19) * mm});
            skLineSegment(sketch, "E23.38.10", {"start": v(13.26, -75.19) * mm, "end": v(13.46, -76.35) * mm});
            skArc(sketch, "E23.38.11", {"start": v(12.82, -77.26) * mm, "mid": v(13.33, -76.94) * mm, "end": v(13.46, -76.35) * mm});
            skArc(sketch, "E23.39.0", {"start": v(23.2, -73.9) * mm, "mid": v(23.57, -74.42) * mm, "end": v(24.2, -74.48) * mm});
            skLineSegment(sketch, "E23.39.1", {"start": v(22.98, -72.96) * mm, "end": v(23.2, -73.9) * mm});
            skArc(sketch, "E23.39.2", {"start": v(22.98, -72.96) * mm, "mid": v(22.94, -72.82) * mm, "end": v(22.87, -72.69) * mm});
            skArc(sketch, "E23.39.3", {"start": v(22.87, -72.69) * mm, "mid": v(22.38, -72) * mm, "end": v(21.87, -71.34) * mm});
            skArc(sketch, "E23.39.4", {"start": v(21.87, -71.34) * mm, "mid": v(21.52, -71.1) * mm, "end": v(21.08, -71.07) * mm});
            skLineSegment(sketch, "E23.39.5", {"start": v(21.08, -71.07) * mm, "end": v(20.83, -71.13) * mm});
            skLineSegment(sketch, "E23.39.6", {"start": v(20.58, -71.2) * mm, "end": v(20.83, -71.13) * mm});
            skArc(sketch, "E23.39.7", {"start": v(20.58, -71.2) * mm, "mid": v(20.2, -71.42) * mm, "end": v(20, -71.8) * mm});
            skArc(sketch, "E23.39.8", {"start": v(19.74, -73.45) * mm, "mid": v(19.85, -72.62) * mm, "end": v(20, -71.8) * mm});
            skArc(sketch, "E23.39.9", {"start": v(19.74, -73.45) * mm, "mid": v(19.74, -73.6) * mm, "end": v(19.76, -73.75) * mm});
            skLineSegment(sketch, "E23.39.10", {"start": v(19.76, -73.75) * mm, "end": v(20.07, -74.88) * mm});
            skArc(sketch, "E23.39.11", {"start": v(19.5, -75.85) * mm, "mid": v(19.98, -75.48) * mm, "end": v(20.07, -74.88) * mm});
            skArc(sketch, "E23.40.0", {"start": v(29.55, -71.6) * mm, "mid": v(29.97, -72.08) * mm, "end": v(30.6, -72.09) * mm});
            skLineSegment(sketch, "E23.40.1", {"start": v(29.25, -70.68) * mm, "end": v(29.55, -71.6) * mm});
            skArc(sketch, "E23.40.2", {"start": v(29.25, -70.68) * mm, "mid": v(29.2, -70.54) * mm, "end": v(29.12, -70.42) * mm});
            skArc(sketch, "E23.40.3", {"start": v(29.12, -70.42) * mm, "mid": v(28.57, -69.78) * mm, "end": v(28, -69.17) * mm});
            skArc(sketch, "E23.40.4", {"start": v(28, -69.17) * mm, "mid": v(27.63, -68.95) * mm, "end": v(27.2, -68.96) * mm});
            skLineSegment(sketch, "E23.40.5", {"start": v(27.2, -68.96) * mm, "end": v(26.95, -69.05) * mm});
            skLineSegment(sketch, "E23.40.6", {"start": v(26.7, -69.13) * mm, "end": v(26.95, -69.05) * mm});
            skArc(sketch, "E23.40.7", {"start": v(26.7, -69.13) * mm, "mid": v(26.35, -69.38) * mm, "end": v(26.18, -69.78) * mm});
            skArc(sketch, "E23.40.8", {"start": v(26.07, -71.45) * mm, "mid": v(26.1, -70.62) * mm, "end": v(26.18, -69.78) * mm});
            skArc(sketch, "E23.40.9", {"start": v(26.07, -71.45) * mm, "mid": v(26.08, -71.6) * mm, "end": v(26.11, -71.74) * mm});
            skLineSegment(sketch, "E23.40.10", {"start": v(26.11, -71.74) * mm, "end": v(26.52, -72.85) * mm});
            skArc(sketch, "E23.40.11", {"start": v(26.04, -73.86) * mm, "mid": v(26.49, -73.46) * mm, "end": v(26.52, -72.85) * mm});
            skArc(sketch, "E23.41.0", {"start": v(35.67, -68.75) * mm, "mid": v(36.14, -69.2) * mm, "end": v(36.77, -69.15) * mm});
            skLineSegment(sketch, "E23.41.1", {"start": v(35.3, -67.86) * mm, "end": v(35.67, -68.75) * mm});
            skArc(sketch, "E23.41.2", {"start": v(35.3, -67.86) * mm, "mid": v(35.23, -67.73) * mm, "end": v(35.14, -67.61) * mm});
            skArc(sketch, "E23.41.3", {"start": v(35.14, -67.61) * mm, "mid": v(34.55, -67.02) * mm, "end": v(33.93, -66.46) * mm});
            skArc(sketch, "E23.41.4", {"start": v(33.93, -66.46) * mm, "mid": v(33.53, -66.28) * mm, "end": v(33.1, -66.33) * mm});
            skLineSegment(sketch, "E23.41.5", {"start": v(33.1, -66.33) * mm, "end": v(32.86, -66.43) * mm});
            skLineSegment(sketch, "E23.41.6", {"start": v(32.63, -66.54) * mm, "end": v(32.86, -66.43) * mm});
            skArc(sketch, "E23.41.7", {"start": v(32.63, -66.54) * mm, "mid": v(32.3, -66.82) * mm, "end": v(32.16, -67.24) * mm});
            skArc(sketch, "E23.41.8", {"start": v(32.2, -68.91) * mm, "mid": v(32.16, -68.07) * mm, "end": v(32.16, -67.24) * mm});
            skArc(sketch, "E23.41.9", {"start": v(32.2, -68.91) * mm, "mid": v(32.22, -69.06) * mm, "end": v(32.27, -69.2) * mm});
            skLineSegment(sketch, "E23.41.10", {"start": v(32.27, -69.2) * mm, "end": v(32.76, -70.26) * mm});
            skArc(sketch, "E23.41.11", {"start": v(32.38, -71.31) * mm, "mid": v(32.79, -70.87) * mm, "end": v(32.76, -70.26) * mm});
            skArc(sketch, "E23.42.0", {"start": v(41.53, -65.38) * mm, "mid": v(42.03, -65.78) * mm, "end": v(42.66, -65.68) * mm});
            skLineSegment(sketch, "E23.42.1", {"start": v(41.08, -64.52) * mm, "end": v(41.53, -65.38) * mm});
            skArc(sketch, "E23.42.2", {"start": v(41.08, -64.52) * mm, "mid": v(41, -64.4) * mm, "end": v(40.9, -64.3) * mm});
            skArc(sketch, "E23.42.3", {"start": v(40.9, -64.3) * mm, "mid": v(40.26, -63.76) * mm, "end": v(39.6, -63.25) * mm});
            skArc(sketch, "E23.42.4", {"start": v(39.6, -63.25) * mm, "mid": v(39.18, -63.1) * mm, "end": v(38.76, -63.2) * mm});
            skLineSegment(sketch, "E23.42.5", {"start": v(38.76, -63.2) * mm, "end": v(38.53, -63.32) * mm});
            skLineSegment(sketch, "E23.42.6", {"start": v(38.3, -63.44) * mm, "end": v(38.53, -63.32) * mm});
            skArc(sketch, "E23.42.7", {"start": v(38.3, -63.44) * mm, "mid": v(38, -63.75) * mm, "end": v(37.9, -64.18) * mm});
            skArc(sketch, "E23.42.8", {"start": v(38.08, -65.84) * mm, "mid": v(37.97, -65.01) * mm, "end": v(37.9, -64.18) * mm});
            skArc(sketch, "E23.42.9", {"start": v(38.08, -65.84) * mm, "mid": v(38.11, -65.99) * mm, "end": v(38.17, -66.12) * mm});
            skLineSegment(sketch, "E23.42.10", {"start": v(38.17, -66.12) * mm, "end": v(38.76, -67.14) * mm});
            skArc(sketch, "E23.42.11", {"start": v(38.47, -68.22) * mm, "mid": v(38.84, -67.74) * mm, "end": v(38.76, -67.14) * mm});
            skArc(sketch, "E23.43.0", {"start": v(47.07, -61.51) * mm, "mid": v(47.6, -61.87) * mm, "end": v(48.22, -61.71) * mm});
            skLineSegment(sketch, "E23.43.1", {"start": v(46.55, -60.7) * mm, "end": v(47.07, -61.51) * mm});
            skArc(sketch, "E23.43.2", {"start": v(46.55, -60.7) * mm, "mid": v(46.46, -60.58) * mm, "end": v(46.35, -60.48) * mm});
            skArc(sketch, "E23.43.3", {"start": v(46.35, -60.48) * mm, "mid": v(45.66, -60) * mm, "end": v(44.95, -59.56) * mm});
            skArc(sketch, "E23.43.4", {"start": v(44.95, -59.56) * mm, "mid": v(44.53, -59.45) * mm, "end": v(44.12, -59.58) * mm});
            skLineSegment(sketch, "E23.43.5", {"start": v(44.12, -59.58) * mm, "end": v(43.9, -59.72) * mm});
            skLineSegment(sketch, "E23.43.6", {"start": v(43.69, -59.86) * mm, "end": v(43.9, -59.72) * mm});
            skArc(sketch, "E23.43.7", {"start": v(43.69, -59.86) * mm, "mid": v(43.4, -60.2) * mm, "end": v(43.35, -60.63) * mm});
            skArc(sketch, "E23.43.8", {"start": v(43.67, -62.27) * mm, "mid": v(43.5, -61.46) * mm, "end": v(43.35, -60.63) * mm});
            skArc(sketch, "E23.43.9", {"start": v(43.67, -62.27) * mm, "mid": v(43.72, -62.41) * mm, "end": v(43.8, -62.54) * mm});
            skLineSegment(sketch, "E23.43.10", {"start": v(43.8, -62.54) * mm, "end": v(44.47, -63.5) * mm});
            skArc(sketch, "E23.43.11", {"start": v(44.27, -64.6) * mm, "mid": v(44.6, -64.1) * mm, "end": v(44.47, -63.5) * mm});
            skArc(sketch, "E23.44.0", {"start": v(52.25, -57.18) * mm, "mid": v(52.81, -57.48) * mm, "end": v(53.41, -57.27) * mm});
            skLineSegment(sketch, "E23.44.1", {"start": v(51.66, -56.4) * mm, "end": v(52.25, -57.18) * mm});
            skArc(sketch, "E23.44.2", {"start": v(51.66, -56.4) * mm, "mid": v(51.56, -56.3) * mm, "end": v(51.44, -56.21) * mm});
            skArc(sketch, "E23.44.3", {"start": v(51.44, -56.21) * mm, "mid": v(50.72, -55.8) * mm, "end": v(49.97, -55.42) * mm});
            skArc(sketch, "E23.44.4", {"start": v(49.97, -55.42) * mm, "mid": v(49.54, -55.34) * mm, "end": v(49.14, -55.5) * mm});
            skLineSegment(sketch, "E23.44.5", {"start": v(49.14, -55.5) * mm, "end": v(48.94, -55.66) * mm});
            skLineSegment(sketch, "E23.44.6", {"start": v(48.74, -55.83) * mm, "end": v(48.94, -55.66) * mm});
            skArc(sketch, "E23.44.7", {"start": v(48.74, -55.83) * mm, "mid": v(48.5, -56.19) * mm, "end": v(48.47, -56.62) * mm});
            skArc(sketch, "E23.44.8", {"start": v(48.93, -58.23) * mm, "mid": v(48.68, -57.43) * mm, "end": v(48.47, -56.62) * mm});
            skArc(sketch, "E23.44.9", {"start": v(48.93, -58.23) * mm, "mid": v(49, -58.36) * mm, "end": v(49.08, -58.49) * mm});
            skLineSegment(sketch, "E23.44.10", {"start": v(49.08, -58.49) * mm, "end": v(49.83, -59.39) * mm});
            skArc(sketch, "E23.44.11", {"start": v(49.73, -60.5) * mm, "mid": v(50.01, -59.97) * mm, "end": v(49.83, -59.39) * mm});
            skArc(sketch, "E23.45.0", {"start": v(57.04, -52.4) * mm, "mid": v(57.62, -52.66) * mm, "end": v(58.2, -52.4) * mm});
            skLineSegment(sketch, "E23.45.1", {"start": v(56.38, -51.7) * mm, "end": v(57.04, -52.4) * mm});
            skArc(sketch, "E23.45.2", {"start": v(56.38, -51.7) * mm, "mid": v(56.27, -51.6) * mm, "end": v(56.15, -51.52) * mm});
            skArc(sketch, "E23.45.3", {"start": v(56.15, -51.52) * mm, "mid": v(55.39, -51.17) * mm, "end": v(54.61, -50.85) * mm});
            skArc(sketch, "E23.45.4", {"start": v(54.61, -50.85) * mm, "mid": v(54.18, -50.81) * mm, "end": v(53.8, -51.01) * mm});
            skLineSegment(sketch, "E23.45.5", {"start": v(53.8, -51.01) * mm, "end": v(53.6, -51.19) * mm});
            skLineSegment(sketch, "E23.45.6", {"start": v(53.42, -51.37) * mm, "end": v(53.6, -51.19) * mm});
            skArc(sketch, "E23.45.7", {"start": v(53.42, -51.37) * mm, "mid": v(53.2, -51.75) * mm, "end": v(53.22, -52.18) * mm});
            skArc(sketch, "E23.45.8", {"start": v(53.82, -53.74) * mm, "mid": v(53.5, -52.97) * mm, "end": v(53.22, -52.18) * mm});
            skArc(sketch, "E23.45.9", {"start": v(53.82, -53.74) * mm, "mid": v(53.9, -53.87) * mm, "end": v(53.99, -53.99) * mm});
            skLineSegment(sketch, "E23.45.10", {"start": v(53.99, -53.99) * mm, "end": v(54.82, -54.82) * mm});
            skArc(sketch, "E23.45.11", {"start": v(54.81, -55.94) * mm, "mid": v(55.05, -55.38) * mm, "end": v(54.82, -54.82) * mm});
            skArc(sketch, "E23.46.0", {"start": v(61.39, -47.24) * mm, "mid": v(62, -47.44) * mm, "end": v(62.55, -47.13) * mm});
            skLineSegment(sketch, "E23.46.1", {"start": v(60.67, -46.58) * mm, "end": v(61.39, -47.24) * mm});
            skArc(sketch, "E23.46.2", {"start": v(60.67, -46.58) * mm, "mid": v(60.56, -46.5) * mm, "end": v(60.42, -46.43) * mm});
            skArc(sketch, "E23.46.3", {"start": v(60.42, -46.43) * mm, "mid": v(59.64, -46.14) * mm, "end": v(58.84, -45.9) * mm});
            skArc(sketch, "E23.46.4", {"start": v(58.84, -45.9) * mm, "mid": v(58.4, -45.9) * mm, "end": v(58.03, -46.13) * mm});
            skLineSegment(sketch, "E23.46.5", {"start": v(58.03, -46.13) * mm, "end": v(57.86, -46.32) * mm});
            skLineSegment(sketch, "E23.46.6", {"start": v(57.7, -46.52) * mm, "end": v(57.86, -46.32) * mm});
            skArc(sketch, "E23.46.7", {"start": v(57.7, -46.52) * mm, "mid": v(57.51, -46.91) * mm, "end": v(57.57, -47.34) * mm});
            skArc(sketch, "E23.46.8", {"start": v(58.3, -48.85) * mm, "mid": v(57.92, -48.1) * mm, "end": v(57.57, -47.34) * mm});
            skArc(sketch, "E23.46.9", {"start": v(58.3, -48.85) * mm, "mid": v(58.38, -48.97) * mm, "end": v(58.49, -49.08) * mm});
            skLineSegment(sketch, "E23.46.10", {"start": v(58.49, -49.08) * mm, "end": v(59.39, -49.83) * mm});
            skArc(sketch, "E23.46.11", {"start": v(59.48, -50.95) * mm, "mid": v(59.67, -50.37) * mm, "end": v(59.39, -49.83) * mm});
            skArc(sketch, "E23.47.0", {"start": v(65.27, -41.7) * mm, "mid": v(65.9, -41.86) * mm, "end": v(66.42, -41.5) * mm});
            skLineSegment(sketch, "E23.47.1", {"start": v(64.5, -41.12) * mm, "end": v(65.27, -41.7) * mm});
            skArc(sketch, "E23.47.2", {"start": v(64.5, -41.12) * mm, "mid": v(64.38, -41.04) * mm, "end": v(64.24, -40.98) * mm});
            skArc(sketch, "E23.47.3", {"start": v(64.24, -40.98) * mm, "mid": v(63.43, -40.77) * mm, "end": v(62.61, -40.6) * mm});
            skArc(sketch, "E23.47.4", {"start": v(62.61, -40.6) * mm, "mid": v(62.18, -40.63) * mm, "end": v(61.83, -40.9) * mm});
            skLineSegment(sketch, "E23.47.5", {"start": v(61.83, -40.9) * mm, "end": v(61.68, -41.1) * mm});
            skLineSegment(sketch, "E23.47.6", {"start": v(61.53, -41.31) * mm, "end": v(61.68, -41.1) * mm});
            skArc(sketch, "E23.47.7", {"start": v(61.53, -41.31) * mm, "mid": v(61.38, -41.72) * mm, "end": v(61.47, -42.15) * mm});
            skArc(sketch, "E23.47.8", {"start": v(62.34, -43.58) * mm, "mid": v(61.89, -42.87) * mm, "end": v(61.47, -42.15) * mm});
            skArc(sketch, "E23.47.9", {"start": v(62.34, -43.58) * mm, "mid": v(62.43, -43.7) * mm, "end": v(62.54, -43.8) * mm});
            skLineSegment(sketch, "E23.47.10", {"start": v(62.54, -43.8) * mm, "end": v(63.5, -44.47) * mm});
            skArc(sketch, "E23.47.11", {"start": v(63.7, -45.57) * mm, "mid": v(63.83, -44.98) * mm, "end": v(63.5, -44.47) * mm});
            skArc(sketch, "E23.48.0", {"start": v(68.66, -35.86) * mm, "mid": v(69.29, -35.95) * mm, "end": v(69.78, -35.55) * mm});
            skLineSegment(sketch, "E23.48.1", {"start": v(67.84, -35.34) * mm, "end": v(68.66, -35.86) * mm});
            skArc(sketch, "E23.48.2", {"start": v(67.84, -35.34) * mm, "mid": v(67.7, -35.27) * mm, "end": v(67.57, -35.23) * mm});
            skArc(sketch, "E23.48.3", {"start": v(67.57, -35.23) * mm, "mid": v(66.74, -35.09) * mm, "end": v(65.91, -34.98) * mm});
            skArc(sketch, "E23.48.4", {"start": v(65.91, -34.98) * mm, "mid": v(65.48, -35.06) * mm, "end": v(65.16, -35.35) * mm});
            skLineSegment(sketch, "E23.48.5", {"start": v(65.16, -35.35) * mm, "end": v(65.03, -35.57) * mm});
            skLineSegment(sketch, "E23.48.6", {"start": v(64.9, -35.8) * mm, "end": v(65.03, -35.57) * mm});
            skArc(sketch, "E23.48.7", {"start": v(64.9, -35.8) * mm, "mid": v(64.78, -36.21) * mm, "end": v(64.91, -36.63) * mm});
            skArc(sketch, "E23.48.8", {"start": v(65.9, -37.98) * mm, "mid": v(65.4, -37.32) * mm, "end": v(64.91, -36.63) * mm});
            skArc(sketch, "E23.48.9", {"start": v(65.9, -37.98) * mm, "mid": v(66, -38.09) * mm, "end": v(66.12, -38.17) * mm});
            skLineSegment(sketch, "E23.48.10", {"start": v(66.12, -38.17) * mm, "end": v(67.14, -38.76) * mm});
            skArc(sketch, "E23.48.11", {"start": v(67.42, -39.85) * mm, "mid": v(67.5, -39.24) * mm, "end": v(67.14, -38.76) * mm});
            skArc(sketch, "E23.49.0", {"start": v(71.52, -29.74) * mm, "mid": v(72.16, -29.78) * mm, "end": v(72.62, -29.33) * mm});
            skLineSegment(sketch, "E23.49.1", {"start": v(70.66, -29.3) * mm, "end": v(71.52, -29.74) * mm});
            skArc(sketch, "E23.49.2", {"start": v(70.66, -29.3) * mm, "mid": v(70.53, -29.23) * mm, "end": v(70.38, -29.2) * mm});
            skArc(sketch, "E23.49.3", {"start": v(70.38, -29.2) * mm, "mid": v(69.55, -29.14) * mm, "end": v(68.71, -29.1) * mm});
            skArc(sketch, "E23.49.4", {"start": v(68.71, -29.1) * mm, "mid": v(68.3, -29.22) * mm, "end": v(68, -29.54) * mm});
            skLineSegment(sketch, "E23.49.5", {"start": v(68, -29.54) * mm, "end": v(67.88, -29.77) * mm});
            skLineSegment(sketch, "E23.49.6", {"start": v(67.77, -30) * mm, "end": v(67.88, -29.77) * mm});
            skArc(sketch, "E23.49.7", {"start": v(67.77, -30) * mm, "mid": v(67.7, -30.43) * mm, "end": v(67.86, -30.83) * mm});
            skArc(sketch, "E23.49.8", {"start": v(68.96, -32.1) * mm, "mid": v(68.4, -31.48) * mm, "end": v(67.86, -30.83) * mm});
            skArc(sketch, "E23.49.9", {"start": v(68.96, -32.1) * mm, "mid": v(69.07, -32.2) * mm, "end": v(69.2, -32.27) * mm});
            skLineSegment(sketch, "E23.49.10", {"start": v(69.2, -32.27) * mm, "end": v(70.26, -32.76) * mm});
            skArc(sketch, "E23.49.11", {"start": v(70.64, -33.82) * mm, "mid": v(70.67, -33.21) * mm, "end": v(70.26, -32.76) * mm});
            skArc(sketch, "E23.50.0", {"start": v(73.84, -23.4) * mm, "mid": v(74.48, -23.38) * mm, "end": v(74.9, -22.9) * mm});
            skLineSegment(sketch, "E23.50.1", {"start": v(72.95, -23.02) * mm, "end": v(73.84, -23.4) * mm});
            skArc(sketch, "E23.50.2", {"start": v(72.95, -23.02) * mm, "mid": v(72.8, -22.98) * mm, "end": v(72.66, -22.96) * mm});
            skArc(sketch, "E23.50.3", {"start": v(72.66, -22.96) * mm, "mid": v(71.82, -22.96) * mm, "end": v(70.99, -23) * mm});
            skArc(sketch, "E23.50.4", {"start": v(70.99, -23) * mm, "mid": v(70.58, -23.15) * mm, "end": v(70.31, -23.5) * mm});
            skLineSegment(sketch, "E23.50.5", {"start": v(70.31, -23.5) * mm, "end": v(70.21, -23.74) * mm});
            skLineSegment(sketch, "E23.50.6", {"start": v(70.12, -23.98) * mm, "end": v(70.21, -23.74) * mm});
            skArc(sketch, "E23.50.7", {"start": v(70.12, -23.98) * mm, "mid": v(70.09, -24.41) * mm, "end": v(70.29, -24.8) * mm});
            skArc(sketch, "E23.50.8", {"start": v(71.5, -25.96) * mm, "mid": v(70.88, -25.4) * mm, "end": v(70.29, -24.8) * mm});
            skArc(sketch, "E23.50.9", {"start": v(71.5, -25.96) * mm, "mid": v(71.61, -26.05) * mm, "end": v(71.74, -26.11) * mm});
            skLineSegment(sketch, "E23.50.10", {"start": v(71.74, -26.11) * mm, "end": v(72.85, -26.52) * mm});
            skArc(sketch, "E23.50.11", {"start": v(73.32, -27.53) * mm, "mid": v(73.3, -26.93) * mm, "end": v(72.85, -26.52) * mm});
            skArc(sketch, "E23.51.0", {"start": v(75.6, -16.87) * mm, "mid": v(76.23, -16.8) * mm, "end": v(76.6, -16.28) * mm});
            skLineSegment(sketch, "E23.51.1", {"start": v(74.67, -16.57) * mm, "end": v(75.6, -16.87) * mm});
            skArc(sketch, "E23.51.2", {"start": v(74.67, -16.57) * mm, "mid": v(74.53, -16.54) * mm, "end": v(74.38, -16.54) * mm});
            skArc(sketch, "E23.51.3", {"start": v(74.38, -16.54) * mm, "mid": v(73.55, -16.62) * mm, "end": v(72.72, -16.73) * mm});
            skArc(sketch, "E23.51.4", {"start": v(72.72, -16.73) * mm, "mid": v(72.33, -16.91) * mm, "end": v(72.1, -17.28) * mm});
            skLineSegment(sketch, "E23.51.5", {"start": v(72.1, -17.28) * mm, "end": v(72.02, -17.53) * mm});
            skLineSegment(sketch, "E23.51.6", {"start": v(71.95, -17.78) * mm, "end": v(72.02, -17.53) * mm});
            skArc(sketch, "E23.51.7", {"start": v(71.95, -17.78) * mm, "mid": v(71.95, -18.21) * mm, "end": v(72.18, -18.58) * mm});
            skArc(sketch, "E23.51.8", {"start": v(73.48, -19.63) * mm, "mid": v(72.82, -19.12) * mm, "end": v(72.18, -18.58) * mm});
            skArc(sketch, "E23.51.9", {"start": v(73.48, -19.63) * mm, "mid": v(73.6, -19.7) * mm, "end": v(73.75, -19.76) * mm});
            skLineSegment(sketch, "E23.51.10", {"start": v(73.75, -19.76) * mm, "end": v(74.88, -20.07) * mm});
            skArc(sketch, "E23.51.11", {"start": v(75.44, -21.04) * mm, "mid": v(75.36, -20.44) * mm, "end": v(74.88, -20.07) * mm});
            skArc(sketch, "E23.52.0", {"start": v(76.78, -10.21) * mm, "mid": v(77.4, -10.09) * mm, "end": v(77.73, -9.54) * mm});
            skLineSegment(sketch, "E23.52.1", {"start": v(75.84, -10) * mm, "end": v(76.78, -10.21) * mm});
            skArc(sketch, "E23.52.2", {"start": v(75.84, -10) * mm, "mid": v(75.69, -9.98) * mm, "end": v(75.54, -10) * mm});
            skArc(sketch, "E23.52.3", {"start": v(75.54, -10) * mm, "mid": v(74.72, -10.14) * mm, "end": v(73.9, -10.33) * mm});
            skArc(sketch, "E23.52.4", {"start": v(73.9, -10.33) * mm, "mid": v(73.53, -10.55) * mm, "end": v(73.32, -10.93) * mm});
            skLineSegment(sketch, "E23.52.5", {"start": v(73.32, -10.93) * mm, "end": v(73.27, -11.18) * mm});
            skLineSegment(sketch, "E23.52.6", {"start": v(73.22, -11.44) * mm, "end": v(73.27, -11.18) * mm});
            skArc(sketch, "E23.52.7", {"start": v(73.22, -11.44) * mm, "mid": v(73.26, -11.87) * mm, "end": v(73.53, -12.22) * mm});
            skArc(sketch, "E23.52.8", {"start": v(74.91, -13.15) * mm, "mid": v(74.2, -12.7) * mm, "end": v(73.53, -12.22) * mm});
            skArc(sketch, "E23.52.9", {"start": v(74.91, -13.15) * mm, "mid": v(75.05, -13.22) * mm, "end": v(75.19, -13.26) * mm});
            skLineSegment(sketch, "E23.52.10", {"start": v(75.19, -13.26) * mm, "end": v(76.35, -13.46) * mm});
            skArc(sketch, "E23.52.11", {"start": v(76.98, -14.38) * mm, "mid": v(76.86, -13.79) * mm, "end": v(76.35, -13.46) * mm});
            skArc(sketch, "E23.53.0", {"start": v(77.38, -3.48) * mm, "mid": v(78, -3.3) * mm, "end": v(78.27, -2.73) * mm});
            skLineSegment(sketch, "E23.53.1", {"start": v(76.42, -3.36) * mm, "end": v(77.38, -3.48) * mm});
            skArc(sketch, "E23.53.2", {"start": v(76.42, -3.36) * mm, "mid": v(76.27, -3.35) * mm, "end": v(76.13, -3.37) * mm});
            skArc(sketch, "E23.53.3", {"start": v(76.13, -3.37) * mm, "mid": v(75.32, -3.6) * mm, "end": v(74.52, -3.85) * mm});
            skArc(sketch, "E23.53.4", {"start": v(74.52, -3.85) * mm, "mid": v(74.16, -4.1) * mm, "end": v(74, -4.5) * mm});
            skLineSegment(sketch, "E23.53.5", {"start": v(74, -4.5) * mm, "end": v(73.97, -4.76) * mm});
            skLineSegment(sketch, "E23.53.6", {"start": v(73.94, -5.01) * mm, "end": v(73.97, -4.76) * mm});
            skArc(sketch, "E23.53.7", {"start": v(73.94, -5.01) * mm, "mid": v(74.02, -5.44) * mm, "end": v(74.31, -5.76) * mm});
            skArc(sketch, "E23.53.8", {"start": v(75.77, -6.57) * mm, "mid": v(75.03, -6.18) * mm, "end": v(74.31, -5.76) * mm});
            skArc(sketch, "E23.53.9", {"start": v(75.77, -6.57) * mm, "mid": v(75.91, -6.63) * mm, "end": v(76.06, -6.65) * mm});
            skLineSegment(sketch, "E23.53.10", {"start": v(76.06, -6.65) * mm, "end": v(77.23, -6.76) * mm});
            skArc(sketch, "E23.53.11", {"start": v(77.95, -7.62) * mm, "mid": v(77.77, -7.04) * mm, "end": v(77.23, -6.76) * mm});
            skArc(sketch, "E23.54.0", {"start": v(77.39, 3.28) * mm, "mid": v(77.98, 3.5) * mm, "end": v(78.2, 4.1) * mm});
            skLineSegment(sketch, "E23.54.1", {"start": v(76.42, 3.32) * mm, "end": v(77.39, 3.28) * mm});
            skArc(sketch, "E23.54.2", {"start": v(76.42, 3.32) * mm, "mid": v(76.27, 3.3) * mm, "end": v(76.13, 3.28) * mm});
            skArc(sketch, "E23.54.3", {"start": v(76.13, 3.28) * mm, "mid": v(75.34, 2.99) * mm, "end": v(74.57, 2.66) * mm});
            skArc(sketch, "E23.54.4", {"start": v(74.57, 2.66) * mm, "mid": v(74.24, 2.38) * mm, "end": v(74.1, 1.97) * mm});
            skLineSegment(sketch, "E23.54.5", {"start": v(74.1, 1.97) * mm, "end": v(74.1, 1.7) * mm});
            skLineSegment(sketch, "E23.54.6", {"start": v(74.1, 1.45) * mm, "end": v(74.1, 1.7) * mm});
            skArc(sketch, "E23.54.7", {"start": v(74.1, 1.45) * mm, "mid": v(74.21, 1.03) * mm, "end": v(74.53, 0.74) * mm});
            skArc(sketch, "E23.54.8", {"start": v(76.06, 0.05) * mm, "mid": v(75.29, 0.38) * mm, "end": v(74.53, 0.74) * mm});
            skArc(sketch, "E23.54.9", {"start": v(76.06, 0.05) * mm, "mid": v(76.2, 0.01) * mm, "end": v(76.35, 0) * mm});
            skLineSegment(sketch, "E23.54.10", {"start": v(76.35, 0) * mm, "end": v(77.53, 0) * mm});
            skArc(sketch, "E23.54.11", {"start": v(78.31, -0.8) * mm, "mid": v(78.08, -0.23) * mm, "end": v(77.53, 0) * mm});
            skArc(sketch, "E23.55.0", {"start": v(76.8, 10) * mm, "mid": v(77.38, 10.3) * mm, "end": v(77.55, 10.9) * mm});
            skLineSegment(sketch, "E23.55.1", {"start": v(75.84, 9.97) * mm, "end": v(76.8, 10) * mm});
            skArc(sketch, "E23.55.2", {"start": v(75.84, 9.97) * mm, "mid": v(75.7, 9.94) * mm, "end": v(75.55, 9.9) * mm});
            skArc(sketch, "E23.55.3", {"start": v(75.55, 9.9) * mm, "mid": v(74.8, 9.54) * mm, "end": v(74.06, 9.15) * mm});
            skArc(sketch, "E23.55.4", {"start": v(74.06, 9.15) * mm, "mid": v(73.75, 8.84) * mm, "end": v(73.65, 8.42) * mm});
            skLineSegment(sketch, "E23.55.5", {"start": v(73.65, 8.42) * mm, "end": v(73.67, 8.16) * mm});
            skLineSegment(sketch, "E23.55.6", {"start": v(73.69, 7.9) * mm, "end": v(73.67, 8.16) * mm});
            skArc(sketch, "E23.55.7", {"start": v(73.69, 7.9) * mm, "mid": v(73.84, 7.5) * mm, "end": v(74.18, 7.23) * mm});
            skArc(sketch, "E23.55.8", {"start": v(75.77, 6.68) * mm, "mid": v(74.97, 6.94) * mm, "end": v(74.18, 7.23) * mm});
            skArc(sketch, "E23.55.9", {"start": v(75.77, 6.68) * mm, "mid": v(75.9, 6.66) * mm, "end": v(76.06, 6.65) * mm});
            skLineSegment(sketch, "E23.55.10", {"start": v(76.06, 6.65) * mm, "end": v(77.23, 6.76) * mm});
            skArc(sketch, "E23.55.11", {"start": v(78.08, 6.03) * mm, "mid": v(77.8, 6.57) * mm, "end": v(77.23, 6.76) * mm});
            skArc(sketch, "E23.56.0", {"start": v(75.64, 16.66) * mm, "mid": v(76.19, 17) * mm, "end": v(76.3, 17.62) * mm});
            skLineSegment(sketch, "E23.56.1", {"start": v(74.68, 16.54) * mm, "end": v(75.64, 16.66) * mm});
            skArc(sketch, "E23.56.2", {"start": v(74.68, 16.54) * mm, "mid": v(74.54, 16.5) * mm, "end": v(74.4, 16.45) * mm});
            skArc(sketch, "E23.56.3", {"start": v(74.4, 16.45) * mm, "mid": v(73.68, 16.02) * mm, "end": v(72.98, 15.57) * mm});
            skArc(sketch, "E23.56.4", {"start": v(72.98, 15.57) * mm, "mid": v(72.7, 15.24) * mm, "end": v(72.64, 14.8) * mm});
            skLineSegment(sketch, "E23.56.5", {"start": v(72.64, 14.8) * mm, "end": v(72.68, 14.55) * mm});
            skLineSegment(sketch, "E23.56.6", {"start": v(72.72, 14.3) * mm, "end": v(72.68, 14.55) * mm});
            skArc(sketch, "E23.56.7", {"start": v(72.72, 14.3) * mm, "mid": v(72.9, 13.9) * mm, "end": v(73.27, 13.67) * mm});
            skArc(sketch, "E23.56.8", {"start": v(74.9, 13.26) * mm, "mid": v(74.08, 13.45) * mm, "end": v(73.27, 13.67) * mm});
            skArc(sketch, "E23.56.9", {"start": v(74.9, 13.26) * mm, "mid": v(75.04, 13.25) * mm, "end": v(75.19, 13.26) * mm});
            skLineSegment(sketch, "E23.56.10", {"start": v(75.19, 13.26) * mm, "end": v(76.35, 13.46) * mm});
            skArc(sketch, "E23.56.11", {"start": v(77.26, 12.82) * mm, "mid": v(76.94, 13.33) * mm, "end": v(76.35, 13.46) * mm});
            skArc(sketch, "E23.57.0", {"start": v(73.9, 23.2) * mm, "mid": v(74.42, 23.57) * mm, "end": v(74.48, 24.2) * mm});
            skLineSegment(sketch, "E23.57.1", {"start": v(72.96, 22.98) * mm, "end": v(73.9, 23.2) * mm});
            skArc(sketch, "E23.57.2", {"start": v(72.96, 22.98) * mm, "mid": v(72.82, 22.94) * mm, "end": v(72.69, 22.87) * mm});
            skArc(sketch, "E23.57.3", {"start": v(72.69, 22.87) * mm, "mid": v(72, 22.38) * mm, "end": v(71.34, 21.87) * mm});
            skArc(sketch, "E23.57.4", {"start": v(71.34, 21.87) * mm, "mid": v(71.1, 21.52) * mm, "end": v(71.07, 21.08) * mm});
            skLineSegment(sketch, "E23.57.5", {"start": v(71.07, 21.08) * mm, "end": v(71.13, 20.83) * mm});
            skLineSegment(sketch, "E23.57.6", {"start": v(71.2, 20.58) * mm, "end": v(71.13, 20.83) * mm});
            skArc(sketch, "E23.57.7", {"start": v(71.2, 20.58) * mm, "mid": v(71.42, 20.2) * mm, "end": v(71.8, 20) * mm});
            skArc(sketch, "E23.57.8", {"start": v(73.45, 19.74) * mm, "mid": v(72.62, 19.85) * mm, "end": v(71.8, 20) * mm});
            skArc(sketch, "E23.57.9", {"start": v(73.45, 19.74) * mm, "mid": v(73.6, 19.74) * mm, "end": v(73.75, 19.76) * mm});
            skLineSegment(sketch, "E23.57.10", {"start": v(73.75, 19.76) * mm, "end": v(74.88, 20.07) * mm});
            skArc(sketch, "E23.57.11", {"start": v(75.85, 19.5) * mm, "mid": v(75.48, 19.98) * mm, "end": v(74.88, 20.07) * mm});
            skArc(sketch, "E23.58.0", {"start": v(71.6, 29.55) * mm, "mid": v(72.08, 29.97) * mm, "end": v(72.09, 30.6) * mm});
            skLineSegment(sketch, "E23.58.1", {"start": v(70.68, 29.25) * mm, "end": v(71.6, 29.55) * mm});
            skArc(sketch, "E23.58.2", {"start": v(70.68, 29.25) * mm, "mid": v(70.54, 29.2) * mm, "end": v(70.42, 29.12) * mm});
            skArc(sketch, "E23.58.3", {"start": v(70.42, 29.12) * mm, "mid": v(69.78, 28.57) * mm, "end": v(69.17, 28) * mm});
            skArc(sketch, "E23.58.4", {"start": v(69.17, 28) * mm, "mid": v(68.95, 27.63) * mm, "end": v(68.96, 27.2) * mm});
            skLineSegment(sketch, "E23.58.5", {"start": v(68.96, 27.2) * mm, "end": v(69.05, 26.95) * mm});
            skLineSegment(sketch, "E23.58.6", {"start": v(69.13, 26.7) * mm, "end": v(69.05, 26.95) * mm});
            skArc(sketch, "E23.58.7", {"start": v(69.13, 26.7) * mm, "mid": v(69.38, 26.35) * mm, "end": v(69.78, 26.18) * mm});
            skArc(sketch, "E23.58.8", {"start": v(71.45, 26.07) * mm, "mid": v(70.62, 26.1) * mm, "end": v(69.78, 26.18) * mm});
            skArc(sketch, "E23.58.9", {"start": v(71.45, 26.07) * mm, "mid": v(71.6, 26.08) * mm, "end": v(71.74, 26.11) * mm});
            skLineSegment(sketch, "E23.58.10", {"start": v(71.74, 26.11) * mm, "end": v(72.85, 26.52) * mm});
            skArc(sketch, "E23.58.11", {"start": v(73.86, 26.04) * mm, "mid": v(73.46, 26.49) * mm, "end": v(72.85, 26.52) * mm});
            skArc(sketch, "E23.59.0", {"start": v(68.75, 35.67) * mm, "mid": v(69.2, 36.14) * mm, "end": v(69.15, 36.77) * mm});
            skLineSegment(sketch, "E23.59.1", {"start": v(67.86, 35.3) * mm, "end": v(68.75, 35.67) * mm});
            skArc(sketch, "E23.59.2", {"start": v(67.86, 35.3) * mm, "mid": v(67.73, 35.23) * mm, "end": v(67.61, 35.14) * mm});
            skArc(sketch, "E23.59.3", {"start": v(67.61, 35.14) * mm, "mid": v(67.02, 34.55) * mm, "end": v(66.46, 33.93) * mm});
            skArc(sketch, "E23.59.4", {"start": v(66.46, 33.93) * mm, "mid": v(66.28, 33.53) * mm, "end": v(66.33, 33.1) * mm});
            skLineSegment(sketch, "E23.59.5", {"start": v(66.33, 33.1) * mm, "end": v(66.43, 32.86) * mm});
            skLineSegment(sketch, "E23.59.6", {"start": v(66.54, 32.63) * mm, "end": v(66.43, 32.86) * mm});
            skArc(sketch, "E23.59.7", {"start": v(66.54, 32.63) * mm, "mid": v(66.82, 32.3) * mm, "end": v(67.24, 32.16) * mm});
            skArc(sketch, "E23.59.8", {"start": v(68.91, 32.2) * mm, "mid": v(68.07, 32.16) * mm, "end": v(67.24, 32.16) * mm});
            skArc(sketch, "E23.59.9", {"start": v(68.91, 32.2) * mm, "mid": v(69.06, 32.22) * mm, "end": v(69.2, 32.27) * mm});
            skLineSegment(sketch, "E23.59.10", {"start": v(69.2, 32.27) * mm, "end": v(70.26, 32.76) * mm});
            skArc(sketch, "E23.59.11", {"start": v(71.31, 32.38) * mm, "mid": v(70.87, 32.79) * mm, "end": v(70.26, 32.76) * mm});
            skArc(sketch, "E23.60.0", {"start": v(65.38, 41.53) * mm, "mid": v(65.78, 42.03) * mm, "end": v(65.68, 42.66) * mm});
            skLineSegment(sketch, "E23.60.1", {"start": v(64.52, 41.08) * mm, "end": v(65.38, 41.53) * mm});
            skArc(sketch, "E23.60.2", {"start": v(64.52, 41.08) * mm, "mid": v(64.4, 41) * mm, "end": v(64.3, 40.9) * mm});
            skArc(sketch, "E23.60.3", {"start": v(64.3, 40.9) * mm, "mid": v(63.76, 40.26) * mm, "end": v(63.25, 39.6) * mm});
            skArc(sketch, "E23.60.4", {"start": v(63.25, 39.6) * mm, "mid": v(63.1, 39.18) * mm, "end": v(63.2, 38.76) * mm});
            skLineSegment(sketch, "E23.60.5", {"start": v(63.2, 38.76) * mm, "end": v(63.32, 38.53) * mm});
            skLineSegment(sketch, "E23.60.6", {"start": v(63.44, 38.3) * mm, "end": v(63.32, 38.53) * mm});
            skArc(sketch, "E23.60.7", {"start": v(63.44, 38.3) * mm, "mid": v(63.75, 38) * mm, "end": v(64.18, 37.9) * mm});
            skArc(sketch, "E23.60.8", {"start": v(65.84, 38.08) * mm, "mid": v(65.01, 37.97) * mm, "end": v(64.18, 37.9) * mm});
            skArc(sketch, "E23.60.9", {"start": v(65.84, 38.08) * mm, "mid": v(65.99, 38.11) * mm, "end": v(66.12, 38.17) * mm});
            skLineSegment(sketch, "E23.60.10", {"start": v(66.12, 38.17) * mm, "end": v(67.14, 38.76) * mm});
            skArc(sketch, "E23.60.11", {"start": v(68.22, 38.47) * mm, "mid": v(67.74, 38.84) * mm, "end": v(67.14, 38.76) * mm});
            skArc(sketch, "E23.61.0", {"start": v(61.51, 47.07) * mm, "mid": v(61.87, 47.6) * mm, "end": v(61.71, 48.22) * mm});
            skLineSegment(sketch, "E23.61.1", {"start": v(60.7, 46.55) * mm, "end": v(61.51, 47.07) * mm});
            skArc(sketch, "E23.61.2", {"start": v(60.7, 46.55) * mm, "mid": v(60.58, 46.46) * mm, "end": v(60.48, 46.35) * mm});
            skArc(sketch, "E23.61.3", {"start": v(60.48, 46.35) * mm, "mid": v(60, 45.66) * mm, "end": v(59.56, 44.95) * mm});
            skArc(sketch, "E23.61.4", {"start": v(59.56, 44.95) * mm, "mid": v(59.45, 44.53) * mm, "end": v(59.58, 44.12) * mm});
            skLineSegment(sketch, "E23.61.5", {"start": v(59.58, 44.12) * mm, "end": v(59.72, 43.9) * mm});
            skLineSegment(sketch, "E23.61.6", {"start": v(59.86, 43.69) * mm, "end": v(59.72, 43.9) * mm});
            skArc(sketch, "E23.61.7", {"start": v(59.86, 43.69) * mm, "mid": v(60.2, 43.4) * mm, "end": v(60.63, 43.35) * mm});
            skArc(sketch, "E23.61.8", {"start": v(62.27, 43.67) * mm, "mid": v(61.46, 43.5) * mm, "end": v(60.63, 43.35) * mm});
            skArc(sketch, "E23.61.9", {"start": v(62.27, 43.67) * mm, "mid": v(62.41, 43.72) * mm, "end": v(62.54, 43.8) * mm});
            skLineSegment(sketch, "E23.61.10", {"start": v(62.54, 43.8) * mm, "end": v(63.5, 44.47) * mm});
            skArc(sketch, "E23.61.11", {"start": v(64.6, 44.27) * mm, "mid": v(64.1, 44.6) * mm, "end": v(63.5, 44.47) * mm});
            skArc(sketch, "E23.62.0", {"start": v(57.18, 52.25) * mm, "mid": v(57.48, 52.81) * mm, "end": v(57.27, 53.41) * mm});
            skLineSegment(sketch, "E23.62.1", {"start": v(56.4, 51.66) * mm, "end": v(57.18, 52.25) * mm});
            skArc(sketch, "E23.62.2", {"start": v(56.4, 51.66) * mm, "mid": v(56.3, 51.56) * mm, "end": v(56.21, 51.44) * mm});
            skArc(sketch, "E23.62.3", {"start": v(56.21, 51.44) * mm, "mid": v(55.8, 50.72) * mm, "end": v(55.42, 49.97) * mm});
            skArc(sketch, "E23.62.4", {"start": v(55.42, 49.97) * mm, "mid": v(55.34, 49.54) * mm, "end": v(55.5, 49.14) * mm});
            skLineSegment(sketch, "E23.62.5", {"start": v(55.5, 49.14) * mm, "end": v(55.66, 48.94) * mm});
            skLineSegment(sketch, "E23.62.6", {"start": v(55.83, 48.74) * mm, "end": v(55.66, 48.94) * mm});
            skArc(sketch, "E23.62.7", {"start": v(55.83, 48.74) * mm, "mid": v(56.19, 48.5) * mm, "end": v(56.62, 48.47) * mm});
            skArc(sketch, "E23.62.8", {"start": v(58.23, 48.93) * mm, "mid": v(57.43, 48.68) * mm, "end": v(56.62, 48.47) * mm});
            skArc(sketch, "E23.62.9", {"start": v(58.23, 48.93) * mm, "mid": v(58.36, 49) * mm, "end": v(58.49, 49.08) * mm});
            skLineSegment(sketch, "E23.62.10", {"start": v(58.49, 49.08) * mm, "end": v(59.39, 49.83) * mm});
            skArc(sketch, "E23.62.11", {"start": v(60.5, 49.73) * mm, "mid": v(59.97, 50.01) * mm, "end": v(59.39, 49.83) * mm});
            skArc(sketch, "E23.63.0", {"start": v(52.4, 57.04) * mm, "mid": v(52.66, 57.62) * mm, "end": v(52.4, 58.2) * mm});
            skLineSegment(sketch, "E23.63.1", {"start": v(51.7, 56.38) * mm, "end": v(52.4, 57.04) * mm});
            skArc(sketch, "E23.63.2", {"start": v(51.7, 56.38) * mm, "mid": v(51.6, 56.27) * mm, "end": v(51.52, 56.15) * mm});
            skArc(sketch, "E23.63.3", {"start": v(51.52, 56.15) * mm, "mid": v(51.17, 55.39) * mm, "end": v(50.85, 54.61) * mm});
            skArc(sketch, "E23.63.4", {"start": v(50.85, 54.61) * mm, "mid": v(50.81, 54.18) * mm, "end": v(51.01, 53.8) * mm});
            skLineSegment(sketch, "E23.63.5", {"start": v(51.01, 53.8) * mm, "end": v(51.19, 53.6) * mm});
            skLineSegment(sketch, "E23.63.6", {"start": v(51.37, 53.42) * mm, "end": v(51.19, 53.6) * mm});
            skArc(sketch, "E23.63.7", {"start": v(51.37, 53.42) * mm, "mid": v(51.75, 53.2) * mm, "end": v(52.18, 53.22) * mm});
            skArc(sketch, "E23.63.8", {"start": v(53.74, 53.82) * mm, "mid": v(52.97, 53.5) * mm, "end": v(52.18, 53.22) * mm});
            skArc(sketch, "E23.63.9", {"start": v(53.74, 53.82) * mm, "mid": v(53.87, 53.9) * mm, "end": v(53.99, 53.99) * mm});
            skLineSegment(sketch, "E23.63.10", {"start": v(53.99, 53.99) * mm, "end": v(54.82, 54.82) * mm});
            skArc(sketch, "E23.63.11", {"start": v(55.94, 54.81) * mm, "mid": v(55.38, 55.05) * mm, "end": v(54.82, 54.82) * mm});
            skArc(sketch, "E23.64.0", {"start": v(47.24, 61.39) * mm, "mid": v(47.44, 62) * mm, "end": v(47.13, 62.55) * mm});
            skLineSegment(sketch, "E23.64.1", {"start": v(46.58, 60.67) * mm, "end": v(47.24, 61.39) * mm});
            skArc(sketch, "E23.64.2", {"start": v(46.58, 60.67) * mm, "mid": v(46.5, 60.56) * mm, "end": v(46.43, 60.42) * mm});
            skArc(sketch, "E23.64.3", {"start": v(46.43, 60.42) * mm, "mid": v(46.14, 59.64) * mm, "end": v(45.9, 58.84) * mm});
            skArc(sketch, "E23.64.4", {"start": v(45.9, 58.84) * mm, "mid": v(45.9, 58.4) * mm, "end": v(46.13, 58.03) * mm});
            skLineSegment(sketch, "E23.64.5", {"start": v(46.13, 58.03) * mm, "end": v(46.32, 57.86) * mm});
            skLineSegment(sketch, "E23.64.6", {"start": v(46.52, 57.7) * mm, "end": v(46.32, 57.86) * mm});
            skArc(sketch, "E23.64.7", {"start": v(46.52, 57.7) * mm, "mid": v(46.91, 57.51) * mm, "end": v(47.34, 57.57) * mm});
            skArc(sketch, "E23.64.8", {"start": v(48.85, 58.3) * mm, "mid": v(48.1, 57.92) * mm, "end": v(47.34, 57.57) * mm});
            skArc(sketch, "E23.64.9", {"start": v(48.85, 58.3) * mm, "mid": v(48.97, 58.38) * mm, "end": v(49.08, 58.49) * mm});
            skLineSegment(sketch, "E23.64.10", {"start": v(49.08, 58.49) * mm, "end": v(49.83, 59.39) * mm});
            skArc(sketch, "E23.64.11", {"start": v(50.95, 59.48) * mm, "mid": v(50.37, 59.67) * mm, "end": v(49.83, 59.39) * mm});
            skArc(sketch, "E23.65.0", {"start": v(41.7, 65.27) * mm, "mid": v(41.86, 65.9) * mm, "end": v(41.5, 66.42) * mm});
            skLineSegment(sketch, "E23.65.1", {"start": v(41.12, 64.5) * mm, "end": v(41.7, 65.27) * mm});
            skArc(sketch, "E23.65.2", {"start": v(41.12, 64.5) * mm, "mid": v(41.04, 64.38) * mm, "end": v(40.98, 64.24) * mm});
            skArc(sketch, "E23.65.3", {"start": v(40.98, 64.24) * mm, "mid": v(40.77, 63.43) * mm, "end": v(40.6, 62.61) * mm});
            skArc(sketch, "E23.65.4", {"start": v(40.6, 62.61) * mm, "mid": v(40.63, 62.18) * mm, "end": v(40.9, 61.83) * mm});
            skLineSegment(sketch, "E23.65.5", {"start": v(40.9, 61.83) * mm, "end": v(41.1, 61.68) * mm});
            skLineSegment(sketch, "E23.65.6", {"start": v(41.31, 61.53) * mm, "end": v(41.1, 61.68) * mm});
            skArc(sketch, "E23.65.7", {"start": v(41.31, 61.53) * mm, "mid": v(41.72, 61.38) * mm, "end": v(42.15, 61.47) * mm});
            skArc(sketch, "E23.65.8", {"start": v(43.58, 62.34) * mm, "mid": v(42.87, 61.89) * mm, "end": v(42.15, 61.47) * mm});
            skArc(sketch, "E23.65.9", {"start": v(43.58, 62.34) * mm, "mid": v(43.7, 62.43) * mm, "end": v(43.8, 62.54) * mm});
            skLineSegment(sketch, "E23.65.10", {"start": v(43.8, 62.54) * mm, "end": v(44.47, 63.5) * mm});
            skArc(sketch, "E23.65.11", {"start": v(45.57, 63.7) * mm, "mid": v(44.98, 63.83) * mm, "end": v(44.47, 63.5) * mm});
            skArc(sketch, "E23.66.0", {"start": v(35.86, 68.66) * mm, "mid": v(35.95, 69.29) * mm, "end": v(35.55, 69.78) * mm});
            skLineSegment(sketch, "E23.66.1", {"start": v(35.34, 67.84) * mm, "end": v(35.86, 68.66) * mm});
            skArc(sketch, "E23.66.2", {"start": v(35.34, 67.84) * mm, "mid": v(35.27, 67.7) * mm, "end": v(35.23, 67.57) * mm});
            skArc(sketch, "E23.66.3", {"start": v(35.23, 67.57) * mm, "mid": v(35.09, 66.74) * mm, "end": v(34.98, 65.91) * mm});
            skArc(sketch, "E23.66.4", {"start": v(34.98, 65.91) * mm, "mid": v(35.06, 65.48) * mm, "end": v(35.35, 65.16) * mm});
            skLineSegment(sketch, "E23.66.5", {"start": v(35.35, 65.16) * mm, "end": v(35.57, 65.03) * mm});
            skLineSegment(sketch, "E23.66.6", {"start": v(35.8, 64.9) * mm, "end": v(35.57, 65.03) * mm});
            skArc(sketch, "E23.66.7", {"start": v(35.8, 64.9) * mm, "mid": v(36.21, 64.78) * mm, "end": v(36.63, 64.91) * mm});
            skArc(sketch, "E23.66.8", {"start": v(37.98, 65.9) * mm, "mid": v(37.32, 65.4) * mm, "end": v(36.63, 64.91) * mm});
            skArc(sketch, "E23.66.9", {"start": v(37.98, 65.9) * mm, "mid": v(38.09, 66) * mm, "end": v(38.17, 66.12) * mm});
            skLineSegment(sketch, "E23.66.10", {"start": v(38.17, 66.12) * mm, "end": v(38.76, 67.14) * mm});
            skArc(sketch, "E23.66.11", {"start": v(39.85, 67.42) * mm, "mid": v(39.24, 67.5) * mm, "end": v(38.76, 67.14) * mm});
            skArc(sketch, "E23.67.0", {"start": v(29.74, 71.52) * mm, "mid": v(29.78, 72.16) * mm, "end": v(29.33, 72.62) * mm});
            skLineSegment(sketch, "E23.67.1", {"start": v(29.3, 70.66) * mm, "end": v(29.74, 71.52) * mm});
            skArc(sketch, "E23.67.2", {"start": v(29.3, 70.66) * mm, "mid": v(29.23, 70.53) * mm, "end": v(29.2, 70.38) * mm});
            skArc(sketch, "E23.67.3", {"start": v(29.2, 70.38) * mm, "mid": v(29.14, 69.55) * mm, "end": v(29.1, 68.71) * mm});
            skArc(sketch, "E23.67.4", {"start": v(29.1, 68.71) * mm, "mid": v(29.22, 68.3) * mm, "end": v(29.54, 68) * mm});
            skLineSegment(sketch, "E23.67.5", {"start": v(29.54, 68) * mm, "end": v(29.77, 67.88) * mm});
            skLineSegment(sketch, "E23.67.6", {"start": v(30, 67.77) * mm, "end": v(29.77, 67.88) * mm});
            skArc(sketch, "E23.67.7", {"start": v(30, 67.77) * mm, "mid": v(30.43, 67.7) * mm, "end": v(30.83, 67.86) * mm});
            skArc(sketch, "E23.67.8", {"start": v(32.1, 68.96) * mm, "mid": v(31.48, 68.4) * mm, "end": v(30.83, 67.86) * mm});
            skArc(sketch, "E23.67.9", {"start": v(32.1, 68.96) * mm, "mid": v(32.2, 69.07) * mm, "end": v(32.27, 69.2) * mm});
            skLineSegment(sketch, "E23.67.10", {"start": v(32.27, 69.2) * mm, "end": v(32.76, 70.26) * mm});
            skArc(sketch, "E23.67.11", {"start": v(33.82, 70.64) * mm, "mid": v(33.21, 70.67) * mm, "end": v(32.76, 70.26) * mm});
            skArc(sketch, "E23.68.0", {"start": v(23.4, 73.84) * mm, "mid": v(23.38, 74.48) * mm, "end": v(22.9, 74.9) * mm});
            skLineSegment(sketch, "E23.68.1", {"start": v(23.02, 72.95) * mm, "end": v(23.4, 73.84) * mm});
            skArc(sketch, "E23.68.2", {"start": v(23.02, 72.95) * mm, "mid": v(22.98, 72.8) * mm, "end": v(22.96, 72.66) * mm});
            skArc(sketch, "E23.68.3", {"start": v(22.96, 72.66) * mm, "mid": v(22.96, 71.82) * mm, "end": v(23, 70.99) * mm});
            skArc(sketch, "E23.68.4", {"start": v(23, 70.99) * mm, "mid": v(23.15, 70.58) * mm, "end": v(23.5, 70.31) * mm});
            skLineSegment(sketch, "E23.68.5", {"start": v(23.5, 70.31) * mm, "end": v(23.74, 70.21) * mm});
            skLineSegment(sketch, "E23.68.6", {"start": v(23.98, 70.12) * mm, "end": v(23.74, 70.21) * mm});
            skArc(sketch, "E23.68.7", {"start": v(23.98, 70.12) * mm, "mid": v(24.41, 70.09) * mm, "end": v(24.8, 70.29) * mm});
            skArc(sketch, "E23.68.8", {"start": v(25.96, 71.5) * mm, "mid": v(25.4, 70.88) * mm, "end": v(24.8, 70.29) * mm});
            skArc(sketch, "E23.68.9", {"start": v(25.96, 71.5) * mm, "mid": v(26.05, 71.61) * mm, "end": v(26.11, 71.74) * mm});
            skLineSegment(sketch, "E23.68.10", {"start": v(26.11, 71.74) * mm, "end": v(26.52, 72.85) * mm});
            skArc(sketch, "E23.68.11", {"start": v(27.53, 73.32) * mm, "mid": v(26.93, 73.3) * mm, "end": v(26.52, 72.85) * mm});
            skArc(sketch, "E23.69.0", {"start": v(16.87, 75.6) * mm, "mid": v(16.8, 76.23) * mm, "end": v(16.28, 76.6) * mm});
            skLineSegment(sketch, "E23.69.1", {"start": v(16.57, 74.67) * mm, "end": v(16.87, 75.6) * mm});
            skArc(sketch, "E23.69.2", {"start": v(16.57, 74.67) * mm, "mid": v(16.54, 74.53) * mm, "end": v(16.54, 74.38) * mm});
            skArc(sketch, "E23.69.3", {"start": v(16.54, 74.38) * mm, "mid": v(16.62, 73.55) * mm, "end": v(16.73, 72.72) * mm});
            skArc(sketch, "E23.69.4", {"start": v(16.73, 72.72) * mm, "mid": v(16.91, 72.33) * mm, "end": v(17.28, 72.1) * mm});
            skLineSegment(sketch, "E23.69.5", {"start": v(17.28, 72.1) * mm, "end": v(17.53, 72.02) * mm});
            skLineSegment(sketch, "E23.69.6", {"start": v(17.78, 71.95) * mm, "end": v(17.53, 72.02) * mm});
            skArc(sketch, "E23.69.7", {"start": v(17.78, 71.95) * mm, "mid": v(18.21, 71.95) * mm, "end": v(18.58, 72.18) * mm});
            skArc(sketch, "E23.69.8", {"start": v(19.63, 73.48) * mm, "mid": v(19.12, 72.82) * mm, "end": v(18.58, 72.18) * mm});
            skArc(sketch, "E23.69.9", {"start": v(19.63, 73.48) * mm, "mid": v(19.7, 73.6) * mm, "end": v(19.76, 73.75) * mm});
            skLineSegment(sketch, "E23.69.10", {"start": v(19.76, 73.75) * mm, "end": v(20.07, 74.88) * mm});
            skArc(sketch, "E23.69.11", {"start": v(21.04, 75.44) * mm, "mid": v(20.44, 75.36) * mm, "end": v(20.07, 74.88) * mm});
            skArc(sketch, "E23.70.0", {"start": v(10.21, 76.78) * mm, "mid": v(10.09, 77.4) * mm, "end": v(9.54, 77.73) * mm});
            skLineSegment(sketch, "E23.70.1", {"start": v(10, 75.84) * mm, "end": v(10.21, 76.78) * mm});
            skArc(sketch, "E23.70.2", {"start": v(10, 75.84) * mm, "mid": v(9.98, 75.69) * mm, "end": v(10, 75.54) * mm});
            skArc(sketch, "E23.70.3", {"start": v(10, 75.54) * mm, "mid": v(10.14, 74.72) * mm, "end": v(10.33, 73.9) * mm});
            skArc(sketch, "E23.70.4", {"start": v(10.33, 73.9) * mm, "mid": v(10.55, 73.53) * mm, "end": v(10.93, 73.32) * mm});
            skLineSegment(sketch, "E23.70.5", {"start": v(10.93, 73.32) * mm, "end": v(11.18, 73.27) * mm});
            skLineSegment(sketch, "E23.70.6", {"start": v(11.44, 73.22) * mm, "end": v(11.18, 73.27) * mm});
            skArc(sketch, "E23.70.7", {"start": v(11.44, 73.22) * mm, "mid": v(11.87, 73.26) * mm, "end": v(12.22, 73.53) * mm});
            skArc(sketch, "E23.70.8", {"start": v(13.15, 74.91) * mm, "mid": v(12.7, 74.2) * mm, "end": v(12.22, 73.53) * mm});
            skArc(sketch, "E23.70.9", {"start": v(13.15, 74.91) * mm, "mid": v(13.22, 75.05) * mm, "end": v(13.26, 75.19) * mm});
            skLineSegment(sketch, "E23.70.10", {"start": v(13.26, 75.19) * mm, "end": v(13.46, 76.35) * mm});
            skArc(sketch, "E23.70.11", {"start": v(14.38, 76.98) * mm, "mid": v(13.79, 76.86) * mm, "end": v(13.46, 76.35) * mm});
            skArc(sketch, "E23.71.0", {"start": v(3.48, 77.38) * mm, "mid": v(3.3, 78) * mm, "end": v(2.73, 78.27) * mm});
            skLineSegment(sketch, "E23.71.1", {"start": v(3.36, 76.42) * mm, "end": v(3.48, 77.38) * mm});
            skArc(sketch, "E23.71.2", {"start": v(3.36, 76.42) * mm, "mid": v(3.35, 76.27) * mm, "end": v(3.37, 76.13) * mm});
            skArc(sketch, "E23.71.3", {"start": v(3.37, 76.13) * mm, "mid": v(3.6, 75.32) * mm, "end": v(3.85, 74.52) * mm});
            skArc(sketch, "E23.71.4", {"start": v(3.85, 74.52) * mm, "mid": v(4.1, 74.16) * mm, "end": v(4.5, 74) * mm});
            skLineSegment(sketch, "E23.71.5", {"start": v(4.5, 74) * mm, "end": v(4.76, 73.97) * mm});
            skLineSegment(sketch, "E23.71.6", {"start": v(5.01, 73.94) * mm, "end": v(4.76, 73.97) * mm});
            skArc(sketch, "E23.71.7", {"start": v(5.01, 73.94) * mm, "mid": v(5.44, 74.02) * mm, "end": v(5.76, 74.31) * mm});
            skArc(sketch, "E23.71.8", {"start": v(6.57, 75.77) * mm, "mid": v(6.18, 75.03) * mm, "end": v(5.76, 74.31) * mm});
            skArc(sketch, "E23.71.9", {"start": v(6.57, 75.77) * mm, "mid": v(6.63, 75.91) * mm, "end": v(6.65, 76.06) * mm});
            skLineSegment(sketch, "E23.71.10", {"start": v(6.65, 76.06) * mm, "end": v(6.76, 77.23) * mm});
            skArc(sketch, "E23.71.11", {"start": v(7.62, 77.95) * mm, "mid": v(7.04, 77.77) * mm, "end": v(6.76, 77.23) * mm});
            skArc(sketch, "E24.trimOffspring", {"start": v(-10.9, 77.55) * mm, "mid": v(-11.86, 77.41) * mm, "end": v(-12.82, 77.26) * mm});
            skArc(sketch, "E25.trimOffspring", {"start": v(-17.62, 76.3) * mm, "mid": v(-18.56, 76.09) * mm, "end": v(-19.5, 75.85) * mm});
            skArc(sketch, "E26.trimOffspring", {"start": v(-24.2, 74.48) * mm, "mid": v(-25.12, 74.18) * mm, "end": v(-26.04, 73.86) * mm});
            skArc(sketch, "E27.trimOffspring", {"start": v(-30.6, 72.09) * mm, "mid": v(-31.5, 71.7) * mm, "end": v(-32.38, 71.31) * mm});
            skArc(sketch, "E28.trimOffspring", {"start": v(-36.77, 69.15) * mm, "mid": v(-37.62, 68.69) * mm, "end": v(-38.47, 68.22) * mm});
            skArc(sketch, "E29.trimOffspring", {"start": v(-42.66, 65.68) * mm, "mid": v(-43.47, 65.15) * mm, "end": v(-44.27, 64.6) * mm});
            skArc(sketch, "E30.trimOffspring", {"start": v(-48.22, 61.71) * mm, "mid": v(-48.98, 61.11) * mm, "end": v(-49.73, 60.5) * mm});
            skArc(sketch, "E31.trimOffspring", {"start": v(-53.41, 57.27) * mm, "mid": v(-54.12, 56.61) * mm, "end": v(-54.81, 55.94) * mm});
            skArc(sketch, "E32.trimOffspring", {"start": v(-58.2, 52.4) * mm, "mid": v(-58.85, 51.68) * mm, "end": v(-59.48, 50.95) * mm});
            skArc(sketch, "E33.trimOffspring", {"start": v(-62.55, 47.13) * mm, "mid": v(-63.13, 46.35) * mm, "end": v(-63.7, 45.57) * mm});
            skArc(sketch, "E34.trimOffspring", {"start": v(-66.42, 41.5) * mm, "mid": v(-66.93, 40.67) * mm, "end": v(-67.42, 39.85) * mm});
            skArc(sketch, "E35.trimOffspring", {"start": v(-69.78, 35.55) * mm, "mid": v(-70.22, 34.69) * mm, "end": v(-70.64, 33.82) * mm});
            skArc(sketch, "E36.trimOffspring", {"start": v(-72.62, 29.33) * mm, "mid": v(-72.97, 28.44) * mm, "end": v(-73.32, 27.53) * mm});
            skArc(sketch, "E37.trimOffspring", {"start": v(-74.9, 22.9) * mm, "mid": v(-75.17, 21.97) * mm, "end": v(-75.44, 21.04) * mm});
            skArc(sketch, "E38.trimOffspring", {"start": v(-76.6, 16.28) * mm, "mid": v(-76.8, 15.33) * mm, "end": v(-76.98, 14.38) * mm});
            skArc(sketch, "E39.trimOffspring", {"start": v(-77.73, 9.54) * mm, "mid": v(-77.85, 8.58) * mm, "end": v(-77.95, 7.62) * mm});
            skArc(sketch, "E40.trimOffspring", {"start": v(-78.27, 2.73) * mm, "mid": v(-78.3, 1.76) * mm, "end": v(-78.31, 0.8) * mm});
            skArc(sketch, "E41.trimOffspring", {"start": v(-78.2, -4.1) * mm, "mid": v(-78.15, -5.07) * mm, "end": v(-78.08, -6.03) * mm});
            skArc(sketch, "E42.trimOffspring", {"start": v(-77.55, -10.9) * mm, "mid": v(-77.41, -11.86) * mm, "end": v(-77.26, -12.82) * mm});
            skArc(sketch, "E43.trimOffspring", {"start": v(-76.3, -17.62) * mm, "mid": v(-76.09, -18.56) * mm, "end": v(-75.85, -19.5) * mm});
            skArc(sketch, "E44.trimOffspring", {"start": v(-74.48, -24.2) * mm, "mid": v(-74.18, -25.12) * mm, "end": v(-73.86, -26.04) * mm});
            skArc(sketch, "E45.trimOffspring", {"start": v(-69.15, -36.77) * mm, "mid": v(-68.69, -37.62) * mm, "end": v(-68.22, -38.47) * mm});
            skArc(sketch, "E46.trimOffspring", {"start": v(-65.68, -42.66) * mm, "mid": v(-65.15, -43.47) * mm, "end": v(-64.6, -44.27) * mm});
            skArc(sketch, "E47.trimOffspring", {"start": v(-61.71, -48.22) * mm, "mid": v(-61.11, -48.98) * mm, "end": v(-60.5, -49.73) * mm});
            skArc(sketch, "E48.trimOffspring", {"start": v(-57.27, -53.41) * mm, "mid": v(-56.61, -54.12) * mm, "end": v(-55.94, -54.81) * mm});
            skArc(sketch, "E49.trimOffspring", {"start": v(-52.4, -58.2) * mm, "mid": v(-51.68, -58.85) * mm, "end": v(-50.95, -59.48) * mm});
            skArc(sketch, "E50.trimOffspring", {"start": v(-47.13, -62.55) * mm, "mid": v(-46.35, -63.13) * mm, "end": v(-45.57, -63.7) * mm});
            skArc(sketch, "E51.trimOffspring", {"start": v(-41.5, -66.42) * mm, "mid": v(-40.67, -66.93) * mm, "end": v(-39.85, -67.42) * mm});
            skArc(sketch, "E52.trimOffspring", {"start": v(-35.55, -69.78) * mm, "mid": v(-34.69, -70.22) * mm, "end": v(-33.82, -70.64) * mm});
            skArc(sketch, "E53.trimOffspring", {"start": v(-29.33, -72.62) * mm, "mid": v(-28.44, -72.97) * mm, "end": v(-27.53, -73.32) * mm});
            skArc(sketch, "E54.trimOffspring", {"start": v(-22.9, -74.9) * mm, "mid": v(-21.97, -75.17) * mm, "end": v(-21.04, -75.44) * mm});
            skArc(sketch, "E55.trimOffspring", {"start": v(-16.28, -76.6) * mm, "mid": v(-15.33, -76.8) * mm, "end": v(-14.38, -76.98) * mm});
            skArc(sketch, "E56.trimOffspring", {"start": v(-9.54, -77.73) * mm, "mid": v(-8.58, -77.85) * mm, "end": v(-7.62, -77.95) * mm});
            skArc(sketch, "E57.trimOffspring", {"start": v(-2.73, -78.27) * mm, "mid": v(-1.76, -78.3) * mm, "end": v(-0.8, -78.31) * mm});
            skArc(sketch, "E58.trimOffspring", {"start": v(4.1, -78.2) * mm, "mid": v(5.07, -78.15) * mm, "end": v(6.03, -78.08) * mm});
            skArc(sketch, "E59.trimOffspring", {"start": v(10.9, -77.55) * mm, "mid": v(11.86, -77.41) * mm, "end": v(12.82, -77.26) * mm});
            skArc(sketch, "E60.trimOffspring", {"start": v(17.62, -76.3) * mm, "mid": v(18.56, -76.09) * mm, "end": v(19.5, -75.85) * mm});
            skArc(sketch, "E61.trimOffspring", {"start": v(24.2, -74.48) * mm, "mid": v(25.12, -74.18) * mm, "end": v(26.04, -73.86) * mm});
            skArc(sketch, "E62.trimOffspring", {"start": v(30.6, -72.09) * mm, "mid": v(31.5, -71.7) * mm, "end": v(32.38, -71.31) * mm});
            skArc(sketch, "E63.trimOffspring", {"start": v(36.77, -69.15) * mm, "mid": v(37.62, -68.69) * mm, "end": v(38.47, -68.22) * mm});
            skArc(sketch, "E64.trimOffspring", {"start": v(42.66, -65.68) * mm, "mid": v(43.47, -65.15) * mm, "end": v(44.27, -64.6) * mm});
            skArc(sketch, "E65.trimOffspring", {"start": v(48.22, -61.71) * mm, "mid": v(48.98, -61.11) * mm, "end": v(49.73, -60.5) * mm});
            skArc(sketch, "E66.trimOffspring", {"start": v(53.41, -57.27) * mm, "mid": v(54.12, -56.61) * mm, "end": v(54.81, -55.94) * mm});
            skArc(sketch, "E67.trimOffspring", {"start": v(58.2, -52.4) * mm, "mid": v(58.85, -51.68) * mm, "end": v(59.48, -50.95) * mm});
            skArc(sketch, "E68.trimOffspring", {"start": v(62.55, -47.13) * mm, "mid": v(63.13, -46.35) * mm, "end": v(63.7, -45.57) * mm});
            skArc(sketch, "E69.trimOffspring", {"start": v(66.42, -41.5) * mm, "mid": v(66.93, -40.67) * mm, "end": v(67.42, -39.85) * mm});
            skArc(sketch, "E70.trimOffspring", {"start": v(69.78, -35.55) * mm, "mid": v(70.22, -34.69) * mm, "end": v(70.64, -33.82) * mm});
            skArc(sketch, "E71.trimOffspring", {"start": v(72.62, -29.33) * mm, "mid": v(72.97, -28.44) * mm, "end": v(73.32, -27.53) * mm});
            skArc(sketch, "E72.trimOffspring", {"start": v(74.9, -22.9) * mm, "mid": v(75.17, -21.97) * mm, "end": v(75.44, -21.04) * mm});
            skArc(sketch, "E73.trimOffspring", {"start": v(76.6, -16.28) * mm, "mid": v(76.8, -15.33) * mm, "end": v(76.98, -14.38) * mm});
            skArc(sketch, "E74.trimOffspring", {"start": v(77.73, -9.54) * mm, "mid": v(77.85, -8.58) * mm, "end": v(77.95, -7.62) * mm});
            skArc(sketch, "E75.trimOffspring", {"start": v(78.27, -2.73) * mm, "mid": v(78.3, -1.76) * mm, "end": v(78.31, -0.8) * mm});
            skArc(sketch, "E76.trimOffspring", {"start": v(78.2, 4.1) * mm, "mid": v(78.15, 5.07) * mm, "end": v(78.08, 6.03) * mm});
            skArc(sketch, "E77.trimOffspring", {"start": v(77.55, 10.9) * mm, "mid": v(77.41, 11.86) * mm, "end": v(77.26, 12.82) * mm});
            skArc(sketch, "E78.trimOffspring", {"start": v(76.3, 17.62) * mm, "mid": v(76.09, 18.56) * mm, "end": v(75.85, 19.5) * mm});
            skArc(sketch, "E79.trimOffspring", {"start": v(74.48, 24.2) * mm, "mid": v(74.18, 25.12) * mm, "end": v(73.86, 26.04) * mm});
            skArc(sketch, "E80.trimOffspring", {"start": v(72.09, 30.6) * mm, "mid": v(71.7, 31.5) * mm, "end": v(71.31, 32.38) * mm});
            skArc(sketch, "E81.trimOffspring", {"start": v(69.15, 36.77) * mm, "mid": v(68.69, 37.62) * mm, "end": v(68.22, 38.47) * mm});
            skArc(sketch, "E82.trimOffspring", {"start": v(65.68, 42.66) * mm, "mid": v(65.15, 43.47) * mm, "end": v(64.6, 44.27) * mm});
            skArc(sketch, "E83.trimOffspring", {"start": v(61.71, 48.22) * mm, "mid": v(61.11, 48.98) * mm, "end": v(60.5, 49.73) * mm});
            skArc(sketch, "E84.trimOffspring", {"start": v(57.27, 53.41) * mm, "mid": v(56.61, 54.12) * mm, "end": v(55.94, 54.81) * mm});
            skArc(sketch, "E85.trimOffspring", {"start": v(52.4, 58.2) * mm, "mid": v(51.68, 58.85) * mm, "end": v(50.95, 59.48) * mm});
            skArc(sketch, "E86.trimOffspring", {"start": v(47.13, 62.55) * mm, "mid": v(46.35, 63.13) * mm, "end": v(45.57, 63.7) * mm});
            skArc(sketch, "E87.trimOffspring", {"start": v(41.5, 66.42) * mm, "mid": v(40.67, 66.93) * mm, "end": v(39.85, 67.42) * mm});
            skArc(sketch, "E88.trimOffspring", {"start": v(35.55, 69.78) * mm, "mid": v(34.69, 70.22) * mm, "end": v(33.82, 70.64) * mm});
            skArc(sketch, "E89.trimOffspring", {"start": v(29.33, 72.62) * mm, "mid": v(28.44, 72.97) * mm, "end": v(27.53, 73.32) * mm});
            skArc(sketch, "E90.trimOffspring", {"start": v(22.9, 74.9) * mm, "mid": v(21.97, 75.17) * mm, "end": v(21.04, 75.44) * mm});
            skArc(sketch, "E91.trimOffspring", {"start": v(16.28, 76.6) * mm, "mid": v(15.33, 76.8) * mm, "end": v(14.38, 76.98) * mm});
            skArc(sketch, "E92.trimOffspring", {"start": v(9.54, 77.73) * mm, "mid": v(8.58, 77.85) * mm, "end": v(7.62, 77.95) * mm});
            skArc(sketch, "E93.trimOffspring", {"start": v(2.73, 78.27) * mm, "mid": v(1.76, 78.3) * mm, "end": v(0.8, 78.31) * mm});
            skLineSegment(sketch, "E94", {"start": v(-72.09, -30.6) * mm, "end": v(-71.31, -32.38) * mm});
            skSolve(sketch);
        }
        {
            var Q0;
            Q0=makeQuery(id+"F0.imprint","IMPRINT",FACE,{"disambiguationData":[TD([[makeQuery(id+"F0.imprint","IMPRINT",EDGE,{"derivedFrom":sQuery(id+"F0.wireOp",EDGE,"E0")}),1.0]])]});
            extrude(context, id + "F1", {"entities" : qUnion([Q0]), "depth" : 6.35 * mm});
        }
        {
            var Q0;
            Q0=makeQuery(id+"F0.imprint","IMPRINT",FACE,{"disambiguationData":[TD([[makeQuery(id+"F0.imprint","IMPRINT",EDGE,{"derivedFrom":sQuery(id+"F0.wireOp",EDGE,"E0")}),-1.0]])]});
            extrude(context, id + "F2", {"entities" : qUnion([Q0]), "operationType" : NewBodyOperationType.ADD, "depth" : 25.4 * mm});
        }
        {
            var Q0;
            Q0=makeQuery(id+"F1.opExtrude","CAP_FACE",FACE,{"disambiguationData":[OSD([sQuery(id+"F0.wireOp",EDGE,"E0"),sQuery(id+"F0.wireOp",EDGE,"E1.MirrorCS"),sQuery(id+"F0.wireOp",EDGE,"E2.MirrorCS"),sQuery(id+"F0.wireOp",EDGE,"E3.MirrorCS"),sQuery(id+"F0.wireOp",EDGE,"E4.MirrorCS"),sQuery(id+"F0.wireOp",EDGE,"E5.MirrorCS"),sQuery(id+"F0.wireOp",EDGE,"E6.MirrorCS"),sQuery(id+"F0.wireOp",EDGE,"E16.filletArc"),sQuery(id+"F0.wireOp",EDGE,"E17.filletArc"),sQuery(id+"F0.wireOp",EDGE,"E18.filletArc"),sQuery(id+"F0.wireOp",EDGE,"E19.filletArc"),sQuery(id+"F0.wireOp",EDGE,"E20.filletArc"),sQuery(id+"F0.wireOp",EDGE,"E21.filletArc"),sQuery(id+"F0.wireOp",EDGE,"E23.1.0"),sQuery(id+"F0.wireOp",EDGE,"E23.1.1"),sQuery(id+"F0.wireOp",EDGE,"E23.1.2"),sQuery(id+"F0.wireOp",EDGE,"E23.1.3"),sQuery(id+"F0.wireOp",EDGE,"E23.1.4"),sQuery(id+"F0.wireOp",EDGE,"E23.1.5"),sQuery(id+"F0.wireOp",EDGE,"E23.1.6"),sQuery(id+"F0.wireOp",EDGE,"E23.1.7"),sQuery(id+"F0.wireOp",EDGE,"E23.1.8"),sQuery(id+"F0.wireOp",EDGE,"E23.1.9"),sQuery(id+"F0.wireOp",EDGE,"E23.1.10"),sQuery(id+"F0.wireOp",EDGE,"E23.1.11"),sQuery(id+"F0.wireOp",EDGE,"E23.2.0"),sQuery(id+"F0.wireOp",EDGE,"E23.2.1"),sQuery(id+"F0.wireOp",EDGE,"E23.2.2"),sQuery(id+"F0.wireOp",EDGE,"E23.2.3"),sQuery(id+"F0.wireOp",EDGE,"E23.2.4"),sQuery(id+"F0.wireOp",EDGE,"E23.2.5"),sQuery(id+"F0.wireOp",EDGE,"E23.2.6"),sQuery(id+"F0.wireOp",EDGE,"E23.2.7"),sQuery(id+"F0.wireOp",EDGE,"E23.2.8"),sQuery(id+"F0.wireOp",EDGE,"E23.2.9"),sQuery(id+"F0.wireOp",EDGE,"E23.2.10"),sQuery(id+"F0.wireOp",EDGE,"E23.2.11"),sQuery(id+"F0.wireOp",EDGE,"E23.3.0"),sQuery(id+"F0.wireOp",EDGE,"E23.3.1"),sQuery(id+"F0.wireOp",EDGE,"E23.3.2"),sQuery(id+"F0.wireOp",EDGE,"E23.3.3"),sQuery(id+"F0.wireOp",EDGE,"E23.3.4"),sQuery(id+"F0.wireOp",EDGE,"E23.3.5"),sQuery(id+"F0.wireOp",EDGE,"E23.3.6"),sQuery(id+"F0.wireOp",EDGE,"E23.3.7"),sQuery(id+"F0.wireOp",EDGE,"E23.3.8"),sQuery(id+"F0.wireOp",EDGE,"E23.3.9"),sQuery(id+"F0.wireOp",EDGE,"E23.3.10"),sQuery(id+"F0.wireOp",EDGE,"E23.3.11"),sQuery(id+"F0.wireOp",EDGE,"E23.4.0"),sQuery(id+"F0.wireOp",EDGE,"E23.4.1"),sQuery(id+"F0.wireOp",EDGE,"E23.4.2"),sQuery(id+"F0.wireOp",EDGE,"E23.4.3"),sQuery(id+"F0.wireOp",EDGE,"E23.4.4"),sQuery(id+"F0.wireOp",EDGE,"E23.4.5"),sQuery(id+"F0.wireOp",EDGE,"E23.4.6"),sQuery(id+"F0.wireOp",EDGE,"E23.4.7"),sQuery(id+"F0.wireOp",EDGE,"E23.4.8"),sQuery(id+"F0.wireOp",EDGE,"E23.4.9"),sQuery(id+"F0.wireOp",EDGE,"E23.4.10"),sQuery(id+"F0.wireOp",EDGE,"E23.4.11"),sQuery(id+"F0.wireOp",EDGE,"E23.5.0"),sQuery(id+"F0.wireOp",EDGE,"E23.5.1"),sQuery(id+"F0.wireOp",EDGE,"E23.5.2"),sQuery(id+"F0.wireOp",EDGE,"E23.5.3"),sQuery(id+"F0.wireOp",EDGE,"E23.5.4"),sQuery(id+"F0.wireOp",EDGE,"E23.5.5"),sQuery(id+"F0.wireOp",EDGE,"E23.5.6"),sQuery(id+"F0.wireOp",EDGE,"E23.5.7"),sQuery(id+"F0.wireOp",EDGE,"E23.5.8"),sQuery(id+"F0.wireOp",EDGE,"E23.5.9"),sQuery(id+"F0.wireOp",EDGE,"E23.5.10"),sQuery(id+"F0.wireOp",EDGE,"E23.5.11"),sQuery(id+"F0.wireOp",EDGE,"E23.6.0"),sQuery(id+"F0.wireOp",EDGE,"E23.6.1"),sQuery(id+"F0.wireOp",EDGE,"E23.6.2"),sQuery(id+"F0.wireOp",EDGE,"E23.6.3"),sQuery(id+"F0.wireOp",EDGE,"E23.6.4"),sQuery(id+"F0.wireOp",EDGE,"E23.6.5"),sQuery(id+"F0.wireOp",EDGE,"E23.6.6"),sQuery(id+"F0.wireOp",EDGE,"E23.6.7"),sQuery(id+"F0.wireOp",EDGE,"E23.6.8"),sQuery(id+"F0.wireOp",EDGE,"E23.6.9"),sQuery(id+"F0.wireOp",EDGE,"E23.6.10"),sQuery(id+"F0.wireOp",EDGE,"E23.6.11"),sQuery(id+"F0.wireOp",EDGE,"E23.7.0"),sQuery(id+"F0.wireOp",EDGE,"E23.7.1"),sQuery(id+"F0.wireOp",EDGE,"E23.7.2"),sQuery(id+"F0.wireOp",EDGE,"E23.7.3"),sQuery(id+"F0.wireOp",EDGE,"E23.7.4"),sQuery(id+"F0.wireOp",EDGE,"E23.7.5"),sQuery(id+"F0.wireOp",EDGE,"E23.7.6"),sQuery(id+"F0.wireOp",EDGE,"E23.7.7"),sQuery(id+"F0.wireOp",EDGE,"E23.7.8"),sQuery(id+"F0.wireOp",EDGE,"E23.7.9"),sQuery(id+"F0.wireOp",EDGE,"E23.7.10"),sQuery(id+"F0.wireOp",EDGE,"E23.7.11"),sQuery(id+"F0.wireOp",EDGE,"E23.8.0"),sQuery(id+"F0.wireOp",EDGE,"E23.8.1"),sQuery(id+"F0.wireOp",EDGE,"E23.8.2"),sQuery(id+"F0.wireOp",EDGE,"E23.8.3"),sQuery(id+"F0.wireOp",EDGE,"E23.8.4"),sQuery(id+"F0.wireOp",EDGE,"E23.8.5"),sQuery(id+"F0.wireOp",EDGE,"E23.8.6"),sQuery(id+"F0.wireOp",EDGE,"E23.8.7"),sQuery(id+"F0.wireOp",EDGE,"E23.8.8"),sQuery(id+"F0.wireOp",EDGE,"E23.8.9"),sQuery(id+"F0.wireOp",EDGE,"E23.8.10"),sQuery(id+"F0.wireOp",EDGE,"E23.8.11"),sQuery(id+"F0.wireOp",EDGE,"E23.9.0"),sQuery(id+"F0.wireOp",EDGE,"E23.9.1"),sQuery(id+"F0.wireOp",EDGE,"E23.9.2"),sQuery(id+"F0.wireOp",EDGE,"E23.9.3"),sQuery(id+"F0.wireOp",EDGE,"E23.9.4"),sQuery(id+"F0.wireOp",EDGE,"E23.9.5"),sQuery(id+"F0.wireOp",EDGE,"E23.9.6"),sQuery(id+"F0.wireOp",EDGE,"E23.9.7"),sQuery(id+"F0.wireOp",EDGE,"E23.9.8"),sQuery(id+"F0.wireOp",EDGE,"E23.9.9"),sQuery(id+"F0.wireOp",EDGE,"E23.9.10"),sQuery(id+"F0.wireOp",EDGE,"E23.9.11"),sQuery(id+"F0.wireOp",EDGE,"E23.10.0"),sQuery(id+"F0.wireOp",EDGE,"E23.10.1"),sQuery(id+"F0.wireOp",EDGE,"E23.10.2"),sQuery(id+"F0.wireOp",EDGE,"E23.10.3"),sQuery(id+"F0.wireOp",EDGE,"E23.10.4"),sQuery(id+"F0.wireOp",EDGE,"E23.10.5"),sQuery(id+"F0.wireOp",EDGE,"E23.10.6"),sQuery(id+"F0.wireOp",EDGE,"E23.10.7"),sQuery(id+"F0.wireOp",EDGE,"E23.10.8"),sQuery(id+"F0.wireOp",EDGE,"E23.10.9"),sQuery(id+"F0.wireOp",EDGE,"E23.10.10"),sQuery(id+"F0.wireOp",EDGE,"E23.10.11"),sQuery(id+"F0.wireOp",EDGE,"E23.11.0"),sQuery(id+"F0.wireOp",EDGE,"E23.11.1"),sQuery(id+"F0.wireOp",EDGE,"E23.11.2"),sQuery(id+"F0.wireOp",EDGE,"E23.11.3"),sQuery(id+"F0.wireOp",EDGE,"E23.11.4"),sQuery(id+"F0.wireOp",EDGE,"E23.11.5"),sQuery(id+"F0.wireOp",EDGE,"E23.11.6"),sQuery(id+"F0.wireOp",EDGE,"E23.11.7"),sQuery(id+"F0.wireOp",EDGE,"E23.11.8"),sQuery(id+"F0.wireOp",EDGE,"E23.11.9"),sQuery(id+"F0.wireOp",EDGE,"E23.11.10"),sQuery(id+"F0.wireOp",EDGE,"E23.11.11"),sQuery(id+"F0.wireOp",EDGE,"E23.12.0"),sQuery(id+"F0.wireOp",EDGE,"E23.12.1"),sQuery(id+"F0.wireOp",EDGE,"E23.12.2"),sQuery(id+"F0.wireOp",EDGE,"E23.12.3"),sQuery(id+"F0.wireOp",EDGE,"E23.12.4"),sQuery(id+"F0.wireOp",EDGE,"E23.12.5"),sQuery(id+"F0.wireOp",EDGE,"E23.12.6"),sQuery(id+"F0.wireOp",EDGE,"E23.12.7"),sQuery(id+"F0.wireOp",EDGE,"E23.12.8"),sQuery(id+"F0.wireOp",EDGE,"E23.12.9"),sQuery(id+"F0.wireOp",EDGE,"E23.12.10"),sQuery(id+"F0.wireOp",EDGE,"E23.12.11"),sQuery(id+"F0.wireOp",EDGE,"E23.13.0"),sQuery(id+"F0.wireOp",EDGE,"E23.13.1"),sQuery(id+"F0.wireOp",EDGE,"E23.13.2"),sQuery(id+"F0.wireOp",EDGE,"E23.13.3"),sQuery(id+"F0.wireOp",EDGE,"E23.13.4"),sQuery(id+"F0.wireOp",EDGE,"E23.13.5"),sQuery(id+"F0.wireOp",EDGE,"E23.13.6"),sQuery(id+"F0.wireOp",EDGE,"E23.13.7"),sQuery(id+"F0.wireOp",EDGE,"E23.13.8"),sQuery(id+"F0.wireOp",EDGE,"E23.13.9"),sQuery(id+"F0.wireOp",EDGE,"E23.13.10"),sQuery(id+"F0.wireOp",EDGE,"E23.13.11"),sQuery(id+"F0.wireOp",EDGE,"E23.14.0"),sQuery(id+"F0.wireOp",EDGE,"E23.14.1"),sQuery(id+"F0.wireOp",EDGE,"E23.14.2"),sQuery(id+"F0.wireOp",EDGE,"E23.14.3"),sQuery(id+"F0.wireOp",EDGE,"E23.14.4"),sQuery(id+"F0.wireOp",EDGE,"E23.14.5"),sQuery(id+"F0.wireOp",EDGE,"E23.14.6"),sQuery(id+"F0.wireOp",EDGE,"E23.14.7"),sQuery(id+"F0.wireOp",EDGE,"E23.14.8"),sQuery(id+"F0.wireOp",EDGE,"E23.14.9"),sQuery(id+"F0.wireOp",EDGE,"E23.14.10"),sQuery(id+"F0.wireOp",EDGE,"E23.14.11"),sQuery(id+"F0.wireOp",EDGE,"E23.15.0"),sQuery(id+"F0.wireOp",EDGE,"E23.15.1"),sQuery(id+"F0.wireOp",EDGE,"E23.15.2"),sQuery(id+"F0.wireOp",EDGE,"E23.15.3"),sQuery(id+"F0.wireOp",EDGE,"E23.15.4"),sQuery(id+"F0.wireOp",EDGE,"E23.15.5"),sQuery(id+"F0.wireOp",EDGE,"E23.15.6"),sQuery(id+"F0.wireOp",EDGE,"E23.15.7"),sQuery(id+"F0.wireOp",EDGE,"E23.15.8"),sQuery(id+"F0.wireOp",EDGE,"E23.15.9"),sQuery(id+"F0.wireOp",EDGE,"E23.15.10"),sQuery(id+"F0.wireOp",EDGE,"E23.15.11"),sQuery(id+"F0.wireOp",EDGE,"E23.16.0"),sQuery(id+"F0.wireOp",EDGE,"E23.16.1"),sQuery(id+"F0.wireOp",EDGE,"E23.16.2"),sQuery(id+"F0.wireOp",EDGE,"E23.16.3"),sQuery(id+"F0.wireOp",EDGE,"E23.16.4"),sQuery(id+"F0.wireOp",EDGE,"E23.16.5"),sQuery(id+"F0.wireOp",EDGE,"E23.16.6"),sQuery(id+"F0.wireOp",EDGE,"E23.16.7"),sQuery(id+"F0.wireOp",EDGE,"E23.16.8"),sQuery(id+"F0.wireOp",EDGE,"E23.16.9"),sQuery(id+"F0.wireOp",EDGE,"E23.16.10"),sQuery(id+"F0.wireOp",EDGE,"E23.16.11"),sQuery(id+"F0.wireOp",EDGE,"E23.17.0"),sQuery(id+"F0.wireOp",EDGE,"E23.17.1"),sQuery(id+"F0.wireOp",EDGE,"E23.17.2"),sQuery(id+"F0.wireOp",EDGE,"E23.17.3"),sQuery(id+"F0.wireOp",EDGE,"E23.17.4"),sQuery(id+"F0.wireOp",EDGE,"E23.17.5"),sQuery(id+"F0.wireOp",EDGE,"E23.17.6"),sQuery(id+"F0.wireOp",EDGE,"E23.17.7"),sQuery(id+"F0.wireOp",EDGE,"E23.17.8"),sQuery(id+"F0.wireOp",EDGE,"E23.17.9"),sQuery(id+"F0.wireOp",EDGE,"E23.17.10"),sQuery(id+"F0.wireOp",EDGE,"E23.17.11"),sQuery(id+"F0.wireOp",EDGE,"E23.18.0"),sQuery(id+"F0.wireOp",EDGE,"E23.18.1"),sQuery(id+"F0.wireOp",EDGE,"E23.18.2"),sQuery(id+"F0.wireOp",EDGE,"E23.18.3"),sQuery(id+"F0.wireOp",EDGE,"E23.18.4"),sQuery(id+"F0.wireOp",EDGE,"E23.18.5"),sQuery(id+"F0.wireOp",EDGE,"E23.18.6"),sQuery(id+"F0.wireOp",EDGE,"E23.18.7"),sQuery(id+"F0.wireOp",EDGE,"E23.18.8"),sQuery(id+"F0.wireOp",EDGE,"E23.18.9"),sQuery(id+"F0.wireOp",EDGE,"E23.18.10"),sQuery(id+"F0.wireOp",EDGE,"E23.18.11"),sQuery(id+"F0.wireOp",EDGE,"E23.19.0"),sQuery(id+"F0.wireOp",EDGE,"E23.19.1"),sQuery(id+"F0.wireOp",EDGE,"E23.19.2"),sQuery(id+"F0.wireOp",EDGE,"E23.19.3"),sQuery(id+"F0.wireOp",EDGE,"E23.19.4"),sQuery(id+"F0.wireOp",EDGE,"E23.19.5"),sQuery(id+"F0.wireOp",EDGE,"E23.19.6"),sQuery(id+"F0.wireOp",EDGE,"E23.19.7"),sQuery(id+"F0.wireOp",EDGE,"E23.19.8"),sQuery(id+"F0.wireOp",EDGE,"E23.19.9"),sQuery(id+"F0.wireOp",EDGE,"E23.19.10"),sQuery(id+"F0.wireOp",EDGE,"E23.19.11"),sQuery(id+"F0.wireOp",EDGE,"E23.20.0"),sQuery(id+"F0.wireOp",EDGE,"E23.20.1"),sQuery(id+"F0.wireOp",EDGE,"E23.20.2"),sQuery(id+"F0.wireOp",EDGE,"E23.20.3"),sQuery(id+"F0.wireOp",EDGE,"E23.20.4"),sQuery(id+"F0.wireOp",EDGE,"E23.20.5"),sQuery(id+"F0.wireOp",EDGE,"E23.20.6"),sQuery(id+"F0.wireOp",EDGE,"E23.20.7"),sQuery(id+"F0.wireOp",EDGE,"E23.20.8"),sQuery(id+"F0.wireOp",EDGE,"E23.20.9"),sQuery(id+"F0.wireOp",EDGE,"E23.20.10"),sQuery(id+"F0.wireOp",EDGE,"E23.20.11"),sQuery(id+"F0.wireOp",EDGE,"E23.21.0"),sQuery(id+"F0.wireOp",EDGE,"E23.21.1"),sQuery(id+"F0.wireOp",EDGE,"E23.21.2"),sQuery(id+"F0.wireOp",EDGE,"E23.21.3"),sQuery(id+"F0.wireOp",EDGE,"E23.21.4"),sQuery(id+"F0.wireOp",EDGE,"E23.21.5"),sQuery(id+"F0.wireOp",EDGE,"E23.21.6"),sQuery(id+"F0.wireOp",EDGE,"E23.21.7"),sQuery(id+"F0.wireOp",EDGE,"E23.21.8"),sQuery(id+"F0.wireOp",EDGE,"E23.21.9"),sQuery(id+"F0.wireOp",EDGE,"E23.21.10"),sQuery(id+"F0.wireOp",EDGE,"E23.21.11"),sQuery(id+"F0.wireOp",EDGE,"E23.22.0"),sQuery(id+"F0.wireOp",EDGE,"E23.22.1"),sQuery(id+"F0.wireOp",EDGE,"E23.22.2"),sQuery(id+"F0.wireOp",EDGE,"E23.22.3"),sQuery(id+"F0.wireOp",EDGE,"E23.22.4"),sQuery(id+"F0.wireOp",EDGE,"E23.22.5"),sQuery(id+"F0.wireOp",EDGE,"E23.22.6"),sQuery(id+"F0.wireOp",EDGE,"E23.22.7"),sQuery(id+"F0.wireOp",EDGE,"E23.22.8"),sQuery(id+"F0.wireOp",EDGE,"E23.22.9"),sQuery(id+"F0.wireOp",EDGE,"E23.22.10"),sQuery(id+"F0.wireOp",EDGE,"E23.22.11"),sQuery(id+"F0.wireOp",EDGE,"E23.23.0"),sQuery(id+"F0.wireOp",EDGE,"E23.23.1"),sQuery(id+"F0.wireOp",EDGE,"E23.23.2"),sQuery(id+"F0.wireOp",EDGE,"E23.23.3"),sQuery(id+"F0.wireOp",EDGE,"E23.23.4"),sQuery(id+"F0.wireOp",EDGE,"E23.23.5"),sQuery(id+"F0.wireOp",EDGE,"E23.23.6"),sQuery(id+"F0.wireOp",EDGE,"E23.23.7"),sQuery(id+"F0.wireOp",EDGE,"E23.23.8"),sQuery(id+"F0.wireOp",EDGE,"E23.23.9"),sQuery(id+"F0.wireOp",EDGE,"E23.23.10"),sQuery(id+"F0.wireOp",EDGE,"E23.23.11"),sQuery(id+"F0.wireOp",EDGE,"E23.24.0"),sQuery(id+"F0.wireOp",EDGE,"E23.24.1"),sQuery(id+"F0.wireOp",EDGE,"E23.24.2"),sQuery(id+"F0.wireOp",EDGE,"E23.24.3"),sQuery(id+"F0.wireOp",EDGE,"E23.24.4"),sQuery(id+"F0.wireOp",EDGE,"E23.24.5"),sQuery(id+"F0.wireOp",EDGE,"E23.24.6"),sQuery(id+"F0.wireOp",EDGE,"E23.24.7"),sQuery(id+"F0.wireOp",EDGE,"E23.24.8"),sQuery(id+"F0.wireOp",EDGE,"E23.24.9"),sQuery(id+"F0.wireOp",EDGE,"E23.24.10"),sQuery(id+"F0.wireOp",EDGE,"E23.24.11"),sQuery(id+"F0.wireOp",EDGE,"E23.25.0"),sQuery(id+"F0.wireOp",EDGE,"E23.25.1"),sQuery(id+"F0.wireOp",EDGE,"E23.25.2"),sQuery(id+"F0.wireOp",EDGE,"E23.25.3"),sQuery(id+"F0.wireOp",EDGE,"E23.25.4"),sQuery(id+"F0.wireOp",EDGE,"E23.25.5"),sQuery(id+"F0.wireOp",EDGE,"E23.25.6"),sQuery(id+"F0.wireOp",EDGE,"E23.25.7"),sQuery(id+"F0.wireOp",EDGE,"E23.25.8"),sQuery(id+"F0.wireOp",EDGE,"E23.25.9"),sQuery(id+"F0.wireOp",EDGE,"E23.25.10"),sQuery(id+"F0.wireOp",EDGE,"E23.25.11"),sQuery(id+"F0.wireOp",EDGE,"E23.26.0"),sQuery(id+"F0.wireOp",EDGE,"E23.26.1"),sQuery(id+"F0.wireOp",EDGE,"E23.26.2"),sQuery(id+"F0.wireOp",EDGE,"E23.26.3"),sQuery(id+"F0.wireOp",EDGE,"E23.26.4"),sQuery(id+"F0.wireOp",EDGE,"E23.26.5"),sQuery(id+"F0.wireOp",EDGE,"E23.26.6"),sQuery(id+"F0.wireOp",EDGE,"E23.26.7"),sQuery(id+"F0.wireOp",EDGE,"E23.26.8"),sQuery(id+"F0.wireOp",EDGE,"E23.26.9"),sQuery(id+"F0.wireOp",EDGE,"E23.26.10"),sQuery(id+"F0.wireOp",EDGE,"E23.26.11"),sQuery(id+"F0.wireOp",EDGE,"E23.27.0"),sQuery(id+"F0.wireOp",EDGE,"E23.27.1"),sQuery(id+"F0.wireOp",EDGE,"E23.27.2"),sQuery(id+"F0.wireOp",EDGE,"E23.27.3"),sQuery(id+"F0.wireOp",EDGE,"E23.27.4"),sQuery(id+"F0.wireOp",EDGE,"E23.27.5"),sQuery(id+"F0.wireOp",EDGE,"E23.27.6"),sQuery(id+"F0.wireOp",EDGE,"E23.27.7"),sQuery(id+"F0.wireOp",EDGE,"E23.27.8"),sQuery(id+"F0.wireOp",EDGE,"E23.27.9"),sQuery(id+"F0.wireOp",EDGE,"E23.27.10"),sQuery(id+"F0.wireOp",EDGE,"E23.27.11"),sQuery(id+"F0.wireOp",EDGE,"E23.28.0"),sQuery(id+"F0.wireOp",EDGE,"E23.28.1"),sQuery(id+"F0.wireOp",EDGE,"E23.28.2"),sQuery(id+"F0.wireOp",EDGE,"E23.28.3"),sQuery(id+"F0.wireOp",EDGE,"E23.28.4"),sQuery(id+"F0.wireOp",EDGE,"E23.28.5"),sQuery(id+"F0.wireOp",EDGE,"E23.28.6"),sQuery(id+"F0.wireOp",EDGE,"E23.28.7"),sQuery(id+"F0.wireOp",EDGE,"E23.28.8"),sQuery(id+"F0.wireOp",EDGE,"E23.28.9"),sQuery(id+"F0.wireOp",EDGE,"E23.28.10"),sQuery(id+"F0.wireOp",EDGE,"E23.28.11"),sQuery(id+"F0.wireOp",EDGE,"E23.29.0"),sQuery(id+"F0.wireOp",EDGE,"E23.29.1"),sQuery(id+"F0.wireOp",EDGE,"E23.29.2"),sQuery(id+"F0.wireOp",EDGE,"E23.29.3"),sQuery(id+"F0.wireOp",EDGE,"E23.29.4"),sQuery(id+"F0.wireOp",EDGE,"E23.29.5"),sQuery(id+"F0.wireOp",EDGE,"E23.29.6"),sQuery(id+"F0.wireOp",EDGE,"E23.29.7"),sQuery(id+"F0.wireOp",EDGE,"E23.29.8"),sQuery(id+"F0.wireOp",EDGE,"E23.29.9"),sQuery(id+"F0.wireOp",EDGE,"E23.29.10"),sQuery(id+"F0.wireOp",EDGE,"E23.29.11"),sQuery(id+"F0.wireOp",EDGE,"E23.30.0"),sQuery(id+"F0.wireOp",EDGE,"E23.30.1"),sQuery(id+"F0.wireOp",EDGE,"E23.30.2"),sQuery(id+"F0.wireOp",EDGE,"E23.30.3"),sQuery(id+"F0.wireOp",EDGE,"E23.30.4"),sQuery(id+"F0.wireOp",EDGE,"E23.30.5"),sQuery(id+"F0.wireOp",EDGE,"E23.30.6"),sQuery(id+"F0.wireOp",EDGE,"E23.30.7"),sQuery(id+"F0.wireOp",EDGE,"E23.30.8"),sQuery(id+"F0.wireOp",EDGE,"E23.30.9"),sQuery(id+"F0.wireOp",EDGE,"E23.30.10"),sQuery(id+"F0.wireOp",EDGE,"E23.30.11"),sQuery(id+"F0.wireOp",EDGE,"E23.31.0"),sQuery(id+"F0.wireOp",EDGE,"E23.31.1"),sQuery(id+"F0.wireOp",EDGE,"E23.31.2"),sQuery(id+"F0.wireOp",EDGE,"E23.31.3"),sQuery(id+"F0.wireOp",EDGE,"E23.31.4"),sQuery(id+"F0.wireOp",EDGE,"E23.31.5"),sQuery(id+"F0.wireOp",EDGE,"E23.31.6"),sQuery(id+"F0.wireOp",EDGE,"E23.31.7"),sQuery(id+"F0.wireOp",EDGE,"E23.31.8"),sQuery(id+"F0.wireOp",EDGE,"E23.31.9"),sQuery(id+"F0.wireOp",EDGE,"E23.31.10"),sQuery(id+"F0.wireOp",EDGE,"E23.31.11"),sQuery(id+"F0.wireOp",EDGE,"E23.32.0"),sQuery(id+"F0.wireOp",EDGE,"E23.32.1"),sQuery(id+"F0.wireOp",EDGE,"E23.32.2"),sQuery(id+"F0.wireOp",EDGE,"E23.32.3"),sQuery(id+"F0.wireOp",EDGE,"E23.32.4"),sQuery(id+"F0.wireOp",EDGE,"E23.32.5"),sQuery(id+"F0.wireOp",EDGE,"E23.32.6"),sQuery(id+"F0.wireOp",EDGE,"E23.32.7"),sQuery(id+"F0.wireOp",EDGE,"E23.32.8"),sQuery(id+"F0.wireOp",EDGE,"E23.32.9"),sQuery(id+"F0.wireOp",EDGE,"E23.32.10"),sQuery(id+"F0.wireOp",EDGE,"E23.32.11"),sQuery(id+"F0.wireOp",EDGE,"E23.33.0"),sQuery(id+"F0.wireOp",EDGE,"E23.33.1"),sQuery(id+"F0.wireOp",EDGE,"E23.33.2"),sQuery(id+"F0.wireOp",EDGE,"E23.33.3"),sQuery(id+"F0.wireOp",EDGE,"E23.33.4"),sQuery(id+"F0.wireOp",EDGE,"E23.33.5"),sQuery(id+"F0.wireOp",EDGE,"E23.33.6"),sQuery(id+"F0.wireOp",EDGE,"E23.33.7"),sQuery(id+"F0.wireOp",EDGE,"E23.33.8"),sQuery(id+"F0.wireOp",EDGE,"E23.33.9"),sQuery(id+"F0.wireOp",EDGE,"E23.33.10"),sQuery(id+"F0.wireOp",EDGE,"E23.33.11"),sQuery(id+"F0.wireOp",EDGE,"E23.34.0"),sQuery(id+"F0.wireOp",EDGE,"E23.34.1"),sQuery(id+"F0.wireOp",EDGE,"E23.34.2"),sQuery(id+"F0.wireOp",EDGE,"E23.34.3"),sQuery(id+"F0.wireOp",EDGE,"E23.34.4"),sQuery(id+"F0.wireOp",EDGE,"E23.34.5"),sQuery(id+"F0.wireOp",EDGE,"E23.34.6"),sQuery(id+"F0.wireOp",EDGE,"E23.34.7"),sQuery(id+"F0.wireOp",EDGE,"E23.34.8"),sQuery(id+"F0.wireOp",EDGE,"E23.34.9"),sQuery(id+"F0.wireOp",EDGE,"E23.34.10"),sQuery(id+"F0.wireOp",EDGE,"E23.34.11"),sQuery(id+"F0.wireOp",EDGE,"E23.35.0"),sQuery(id+"F0.wireOp",EDGE,"E23.35.1"),sQuery(id+"F0.wireOp",EDGE,"E23.35.2"),sQuery(id+"F0.wireOp",EDGE,"E23.35.3"),sQuery(id+"F0.wireOp",EDGE,"E23.35.4"),sQuery(id+"F0.wireOp",EDGE,"E23.35.5"),sQuery(id+"F0.wireOp",EDGE,"E23.35.6"),sQuery(id+"F0.wireOp",EDGE,"E23.35.7"),sQuery(id+"F0.wireOp",EDGE,"E23.35.8"),sQuery(id+"F0.wireOp",EDGE,"E23.35.9"),sQuery(id+"F0.wireOp",EDGE,"E23.35.10"),sQuery(id+"F0.wireOp",EDGE,"E23.35.11"),sQuery(id+"F0.wireOp",EDGE,"E23.36.0"),sQuery(id+"F0.wireOp",EDGE,"E23.36.1"),sQuery(id+"F0.wireOp",EDGE,"E23.36.2"),sQuery(id+"F0.wireOp",EDGE,"E23.36.3"),sQuery(id+"F0.wireOp",EDGE,"E23.36.4"),sQuery(id+"F0.wireOp",EDGE,"E23.36.5"),sQuery(id+"F0.wireOp",EDGE,"E23.36.6"),sQuery(id+"F0.wireOp",EDGE,"E23.36.7"),sQuery(id+"F0.wireOp",EDGE,"E23.36.8"),sQuery(id+"F0.wireOp",EDGE,"E23.36.9"),sQuery(id+"F0.wireOp",EDGE,"E23.36.10"),sQuery(id+"F0.wireOp",EDGE,"E23.36.11"),sQuery(id+"F0.wireOp",EDGE,"E23.37.0"),sQuery(id+"F0.wireOp",EDGE,"E23.37.1"),sQuery(id+"F0.wireOp",EDGE,"E23.37.2"),sQuery(id+"F0.wireOp",EDGE,"E23.37.3"),sQuery(id+"F0.wireOp",EDGE,"E23.37.4"),sQuery(id+"F0.wireOp",EDGE,"E23.37.5"),sQuery(id+"F0.wireOp",EDGE,"E23.37.6"),sQuery(id+"F0.wireOp",EDGE,"E23.37.7"),sQuery(id+"F0.wireOp",EDGE,"E23.37.8"),sQuery(id+"F0.wireOp",EDGE,"E23.37.9"),sQuery(id+"F0.wireOp",EDGE,"E23.37.10"),sQuery(id+"F0.wireOp",EDGE,"E23.37.11"),sQuery(id+"F0.wireOp",EDGE,"E23.38.0"),sQuery(id+"F0.wireOp",EDGE,"E23.38.1"),sQuery(id+"F0.wireOp",EDGE,"E23.38.2"),sQuery(id+"F0.wireOp",EDGE,"E23.38.3"),sQuery(id+"F0.wireOp",EDGE,"E23.38.4"),sQuery(id+"F0.wireOp",EDGE,"E23.38.5"),sQuery(id+"F0.wireOp",EDGE,"E23.38.6"),sQuery(id+"F0.wireOp",EDGE,"E23.38.7"),sQuery(id+"F0.wireOp",EDGE,"E23.38.8"),sQuery(id+"F0.wireOp",EDGE,"E23.38.9"),sQuery(id+"F0.wireOp",EDGE,"E23.38.10"),sQuery(id+"F0.wireOp",EDGE,"E23.38.11"),sQuery(id+"F0.wireOp",EDGE,"E23.39.0"),sQuery(id+"F0.wireOp",EDGE,"E23.39.1"),sQuery(id+"F0.wireOp",EDGE,"E23.39.2"),sQuery(id+"F0.wireOp",EDGE,"E23.39.3"),sQuery(id+"F0.wireOp",EDGE,"E23.39.4"),sQuery(id+"F0.wireOp",EDGE,"E23.39.5"),sQuery(id+"F0.wireOp",EDGE,"E23.39.6"),sQuery(id+"F0.wireOp",EDGE,"E23.39.7"),sQuery(id+"F0.wireOp",EDGE,"E23.39.8"),sQuery(id+"F0.wireOp",EDGE,"E23.39.9"),sQuery(id+"F0.wireOp",EDGE,"E23.39.10"),sQuery(id+"F0.wireOp",EDGE,"E23.39.11"),sQuery(id+"F0.wireOp",EDGE,"E23.40.0"),sQuery(id+"F0.wireOp",EDGE,"E23.40.1"),sQuery(id+"F0.wireOp",EDGE,"E23.40.2"),sQuery(id+"F0.wireOp",EDGE,"E23.40.3"),sQuery(id+"F0.wireOp",EDGE,"E23.40.4"),sQuery(id+"F0.wireOp",EDGE,"E23.40.5"),sQuery(id+"F0.wireOp",EDGE,"E23.40.6"),sQuery(id+"F0.wireOp",EDGE,"E23.40.7"),sQuery(id+"F0.wireOp",EDGE,"E23.40.8"),sQuery(id+"F0.wireOp",EDGE,"E23.40.9"),sQuery(id+"F0.wireOp",EDGE,"E23.40.10"),sQuery(id+"F0.wireOp",EDGE,"E23.40.11"),sQuery(id+"F0.wireOp",EDGE,"E23.41.0"),sQuery(id+"F0.wireOp",EDGE,"E23.41.1"),sQuery(id+"F0.wireOp",EDGE,"E23.41.2"),sQuery(id+"F0.wireOp",EDGE,"E23.41.3"),sQuery(id+"F0.wireOp",EDGE,"E23.41.4"),sQuery(id+"F0.wireOp",EDGE,"E23.41.5"),sQuery(id+"F0.wireOp",EDGE,"E23.41.6"),sQuery(id+"F0.wireOp",EDGE,"E23.41.7"),sQuery(id+"F0.wireOp",EDGE,"E23.41.8"),sQuery(id+"F0.wireOp",EDGE,"E23.41.9"),sQuery(id+"F0.wireOp",EDGE,"E23.41.10"),sQuery(id+"F0.wireOp",EDGE,"E23.41.11"),sQuery(id+"F0.wireOp",EDGE,"E23.42.0"),sQuery(id+"F0.wireOp",EDGE,"E23.42.1"),sQuery(id+"F0.wireOp",EDGE,"E23.42.2"),sQuery(id+"F0.wireOp",EDGE,"E23.42.3"),sQuery(id+"F0.wireOp",EDGE,"E23.42.4"),sQuery(id+"F0.wireOp",EDGE,"E23.42.5"),sQuery(id+"F0.wireOp",EDGE,"E23.42.6"),sQuery(id+"F0.wireOp",EDGE,"E23.42.7"),sQuery(id+"F0.wireOp",EDGE,"E23.42.8"),sQuery(id+"F0.wireOp",EDGE,"E23.42.9"),sQuery(id+"F0.wireOp",EDGE,"E23.42.10"),sQuery(id+"F0.wireOp",EDGE,"E23.42.11"),sQuery(id+"F0.wireOp",EDGE,"E23.43.0"),sQuery(id+"F0.wireOp",EDGE,"E23.43.1"),sQuery(id+"F0.wireOp",EDGE,"E23.43.2"),sQuery(id+"F0.wireOp",EDGE,"E23.43.3"),sQuery(id+"F0.wireOp",EDGE,"E23.43.4"),sQuery(id+"F0.wireOp",EDGE,"E23.43.5"),sQuery(id+"F0.wireOp",EDGE,"E23.43.6"),sQuery(id+"F0.wireOp",EDGE,"E23.43.7"),sQuery(id+"F0.wireOp",EDGE,"E23.43.8"),sQuery(id+"F0.wireOp",EDGE,"E23.43.9"),sQuery(id+"F0.wireOp",EDGE,"E23.43.10"),sQuery(id+"F0.wireOp",EDGE,"E23.43.11"),sQuery(id+"F0.wireOp",EDGE,"E23.44.0"),sQuery(id+"F0.wireOp",EDGE,"E23.44.1"),sQuery(id+"F0.wireOp",EDGE,"E23.44.2"),sQuery(id+"F0.wireOp",EDGE,"E23.44.3"),sQuery(id+"F0.wireOp",EDGE,"E23.44.4"),sQuery(id+"F0.wireOp",EDGE,"E23.44.5"),sQuery(id+"F0.wireOp",EDGE,"E23.44.6"),sQuery(id+"F0.wireOp",EDGE,"E23.44.7"),sQuery(id+"F0.wireOp",EDGE,"E23.44.8"),sQuery(id+"F0.wireOp",EDGE,"E23.44.9"),sQuery(id+"F0.wireOp",EDGE,"E23.44.10"),sQuery(id+"F0.wireOp",EDGE,"E23.44.11"),sQuery(id+"F0.wireOp",EDGE,"E23.45.0"),sQuery(id+"F0.wireOp",EDGE,"E23.45.1"),sQuery(id+"F0.wireOp",EDGE,"E23.45.2"),sQuery(id+"F0.wireOp",EDGE,"E23.45.3"),sQuery(id+"F0.wireOp",EDGE,"E23.45.4"),sQuery(id+"F0.wireOp",EDGE,"E23.45.5"),sQuery(id+"F0.wireOp",EDGE,"E23.45.6"),sQuery(id+"F0.wireOp",EDGE,"E23.45.7"),sQuery(id+"F0.wireOp",EDGE,"E23.45.8"),sQuery(id+"F0.wireOp",EDGE,"E23.45.9"),sQuery(id+"F0.wireOp",EDGE,"E23.45.10"),sQuery(id+"F0.wireOp",EDGE,"E23.45.11"),sQuery(id+"F0.wireOp",EDGE,"E23.46.0"),sQuery(id+"F0.wireOp",EDGE,"E23.46.1"),sQuery(id+"F0.wireOp",EDGE,"E23.46.2"),sQuery(id+"F0.wireOp",EDGE,"E23.46.3"),sQuery(id+"F0.wireOp",EDGE,"E23.46.4"),sQuery(id+"F0.wireOp",EDGE,"E23.46.5"),sQuery(id+"F0.wireOp",EDGE,"E23.46.6"),sQuery(id+"F0.wireOp",EDGE,"E23.46.7"),sQuery(id+"F0.wireOp",EDGE,"E23.46.8"),sQuery(id+"F0.wireOp",EDGE,"E23.46.9"),sQuery(id+"F0.wireOp",EDGE,"E23.46.10"),sQuery(id+"F0.wireOp",EDGE,"E23.46.11"),sQuery(id+"F0.wireOp",EDGE,"E23.47.0"),sQuery(id+"F0.wireOp",EDGE,"E23.47.1"),sQuery(id+"F0.wireOp",EDGE,"E23.47.2"),sQuery(id+"F0.wireOp",EDGE,"E23.47.3"),sQuery(id+"F0.wireOp",EDGE,"E23.47.4"),sQuery(id+"F0.wireOp",EDGE,"E23.47.5"),sQuery(id+"F0.wireOp",EDGE,"E23.47.6"),sQuery(id+"F0.wireOp",EDGE,"E23.47.7"),sQuery(id+"F0.wireOp",EDGE,"E23.47.8"),sQuery(id+"F0.wireOp",EDGE,"E23.47.9"),sQuery(id+"F0.wireOp",EDGE,"E23.47.10"),sQuery(id+"F0.wireOp",EDGE,"E23.47.11"),sQuery(id+"F0.wireOp",EDGE,"E23.48.0"),sQuery(id+"F0.wireOp",EDGE,"E23.48.1"),sQuery(id+"F0.wireOp",EDGE,"E23.48.2"),sQuery(id+"F0.wireOp",EDGE,"E23.48.3"),sQuery(id+"F0.wireOp",EDGE,"E23.48.4"),sQuery(id+"F0.wireOp",EDGE,"E23.48.5"),sQuery(id+"F0.wireOp",EDGE,"E23.48.6"),sQuery(id+"F0.wireOp",EDGE,"E23.48.7"),sQuery(id+"F0.wireOp",EDGE,"E23.48.8"),sQuery(id+"F0.wireOp",EDGE,"E23.48.9"),sQuery(id+"F0.wireOp",EDGE,"E23.48.10"),sQuery(id+"F0.wireOp",EDGE,"E23.48.11"),sQuery(id+"F0.wireOp",EDGE,"E23.49.0"),sQuery(id+"F0.wireOp",EDGE,"E23.49.1"),sQuery(id+"F0.wireOp",EDGE,"E23.49.2"),sQuery(id+"F0.wireOp",EDGE,"E23.49.3"),sQuery(id+"F0.wireOp",EDGE,"E23.49.4"),sQuery(id+"F0.wireOp",EDGE,"E23.49.5"),sQuery(id+"F0.wireOp",EDGE,"E23.49.6"),sQuery(id+"F0.wireOp",EDGE,"E23.49.7"),sQuery(id+"F0.wireOp",EDGE,"E23.49.8"),sQuery(id+"F0.wireOp",EDGE,"E23.49.9"),sQuery(id+"F0.wireOp",EDGE,"E23.49.10"),sQuery(id+"F0.wireOp",EDGE,"E23.49.11"),sQuery(id+"F0.wireOp",EDGE,"E23.50.0"),sQuery(id+"F0.wireOp",EDGE,"E23.50.1"),sQuery(id+"F0.wireOp",EDGE,"E23.50.2"),sQuery(id+"F0.wireOp",EDGE,"E23.50.3"),sQuery(id+"F0.wireOp",EDGE,"E23.50.4"),sQuery(id+"F0.wireOp",EDGE,"E23.50.5"),sQuery(id+"F0.wireOp",EDGE,"E23.50.6"),sQuery(id+"F0.wireOp",EDGE,"E23.50.7"),sQuery(id+"F0.wireOp",EDGE,"E23.50.8"),sQuery(id+"F0.wireOp",EDGE,"E23.50.9"),sQuery(id+"F0.wireOp",EDGE,"E23.50.10"),sQuery(id+"F0.wireOp",EDGE,"E23.50.11"),sQuery(id+"F0.wireOp",EDGE,"E23.51.0"),sQuery(id+"F0.wireOp",EDGE,"E23.51.1"),sQuery(id+"F0.wireOp",EDGE,"E23.51.2"),sQuery(id+"F0.wireOp",EDGE,"E23.51.3"),sQuery(id+"F0.wireOp",EDGE,"E23.51.4"),sQuery(id+"F0.wireOp",EDGE,"E23.51.5"),sQuery(id+"F0.wireOp",EDGE,"E23.51.6"),sQuery(id+"F0.wireOp",EDGE,"E23.51.7"),sQuery(id+"F0.wireOp",EDGE,"E23.51.8"),sQuery(id+"F0.wireOp",EDGE,"E23.51.9"),sQuery(id+"F0.wireOp",EDGE,"E23.51.10"),sQuery(id+"F0.wireOp",EDGE,"E23.51.11"),sQuery(id+"F0.wireOp",EDGE,"E23.52.0"),sQuery(id+"F0.wireOp",EDGE,"E23.52.1"),sQuery(id+"F0.wireOp",EDGE,"E23.52.2"),sQuery(id+"F0.wireOp",EDGE,"E23.52.3"),sQuery(id+"F0.wireOp",EDGE,"E23.52.4"),sQuery(id+"F0.wireOp",EDGE,"E23.52.5"),sQuery(id+"F0.wireOp",EDGE,"E23.52.6"),sQuery(id+"F0.wireOp",EDGE,"E23.52.7"),sQuery(id+"F0.wireOp",EDGE,"E23.52.8"),sQuery(id+"F0.wireOp",EDGE,"E23.52.9"),sQuery(id+"F0.wireOp",EDGE,"E23.52.10"),sQuery(id+"F0.wireOp",EDGE,"E23.52.11"),sQuery(id+"F0.wireOp",EDGE,"E23.53.0"),sQuery(id+"F0.wireOp",EDGE,"E23.53.1"),sQuery(id+"F0.wireOp",EDGE,"E23.53.2"),sQuery(id+"F0.wireOp",EDGE,"E23.53.3"),sQuery(id+"F0.wireOp",EDGE,"E23.53.4"),sQuery(id+"F0.wireOp",EDGE,"E23.53.5"),sQuery(id+"F0.wireOp",EDGE,"E23.53.6"),sQuery(id+"F0.wireOp",EDGE,"E23.53.7"),sQuery(id+"F0.wireOp",EDGE,"E23.53.8"),sQuery(id+"F0.wireOp",EDGE,"E23.53.9"),sQuery(id+"F0.wireOp",EDGE,"E23.53.10"),sQuery(id+"F0.wireOp",EDGE,"E23.53.11"),sQuery(id+"F0.wireOp",EDGE,"E23.54.0"),sQuery(id+"F0.wireOp",EDGE,"E23.54.1"),sQuery(id+"F0.wireOp",EDGE,"E23.54.2"),sQuery(id+"F0.wireOp",EDGE,"E23.54.3"),sQuery(id+"F0.wireOp",EDGE,"E23.54.4"),sQuery(id+"F0.wireOp",EDGE,"E23.54.5"),sQuery(id+"F0.wireOp",EDGE,"E23.54.6"),sQuery(id+"F0.wireOp",EDGE,"E23.54.7"),sQuery(id+"F0.wireOp",EDGE,"E23.54.8"),sQuery(id+"F0.wireOp",EDGE,"E23.54.9"),sQuery(id+"F0.wireOp",EDGE,"E23.54.10"),sQuery(id+"F0.wireOp",EDGE,"E23.54.11"),sQuery(id+"F0.wireOp",EDGE,"E23.55.0"),sQuery(id+"F0.wireOp",EDGE,"E23.55.1"),sQuery(id+"F0.wireOp",EDGE,"E23.55.2"),sQuery(id+"F0.wireOp",EDGE,"E23.55.3"),sQuery(id+"F0.wireOp",EDGE,"E23.55.4"),sQuery(id+"F0.wireOp",EDGE,"E23.55.5"),sQuery(id+"F0.wireOp",EDGE,"E23.55.6"),sQuery(id+"F0.wireOp",EDGE,"E23.55.7"),sQuery(id+"F0.wireOp",EDGE,"E23.55.8"),sQuery(id+"F0.wireOp",EDGE,"E23.55.9"),sQuery(id+"F0.wireOp",EDGE,"E23.55.10"),sQuery(id+"F0.wireOp",EDGE,"E23.55.11"),sQuery(id+"F0.wireOp",EDGE,"E23.56.0"),sQuery(id+"F0.wireOp",EDGE,"E23.56.1"),sQuery(id+"F0.wireOp",EDGE,"E23.56.2"),sQuery(id+"F0.wireOp",EDGE,"E23.56.3"),sQuery(id+"F0.wireOp",EDGE,"E23.56.4"),sQuery(id+"F0.wireOp",EDGE,"E23.56.5"),sQuery(id+"F0.wireOp",EDGE,"E23.56.6"),sQuery(id+"F0.wireOp",EDGE,"E23.56.7"),sQuery(id+"F0.wireOp",EDGE,"E23.56.8"),sQuery(id+"F0.wireOp",EDGE,"E23.56.9"),sQuery(id+"F0.wireOp",EDGE,"E23.56.10"),sQuery(id+"F0.wireOp",EDGE,"E23.56.11"),sQuery(id+"F0.wireOp",EDGE,"E23.57.0"),sQuery(id+"F0.wireOp",EDGE,"E23.57.1"),sQuery(id+"F0.wireOp",EDGE,"E23.57.2"),sQuery(id+"F0.wireOp",EDGE,"E23.57.3"),sQuery(id+"F0.wireOp",EDGE,"E23.57.4"),sQuery(id+"F0.wireOp",EDGE,"E23.57.5"),sQuery(id+"F0.wireOp",EDGE,"E23.57.6"),sQuery(id+"F0.wireOp",EDGE,"E23.57.7"),sQuery(id+"F0.wireOp",EDGE,"E23.57.8"),sQuery(id+"F0.wireOp",EDGE,"E23.57.9"),sQuery(id+"F0.wireOp",EDGE,"E23.57.10"),sQuery(id+"F0.wireOp",EDGE,"E23.57.11"),sQuery(id+"F0.wireOp",EDGE,"E23.58.0"),sQuery(id+"F0.wireOp",EDGE,"E23.58.1"),sQuery(id+"F0.wireOp",EDGE,"E23.58.2"),sQuery(id+"F0.wireOp",EDGE,"E23.58.3"),sQuery(id+"F0.wireOp",EDGE,"E23.58.4"),sQuery(id+"F0.wireOp",EDGE,"E23.58.5"),sQuery(id+"F0.wireOp",EDGE,"E23.58.6"),sQuery(id+"F0.wireOp",EDGE,"E23.58.7"),sQuery(id+"F0.wireOp",EDGE,"E23.58.8"),sQuery(id+"F0.wireOp",EDGE,"E23.58.9"),sQuery(id+"F0.wireOp",EDGE,"E23.58.10"),sQuery(id+"F0.wireOp",EDGE,"E23.58.11"),sQuery(id+"F0.wireOp",EDGE,"E23.59.0"),sQuery(id+"F0.wireOp",EDGE,"E23.59.1"),sQuery(id+"F0.wireOp",EDGE,"E23.59.2"),sQuery(id+"F0.wireOp",EDGE,"E23.59.3"),sQuery(id+"F0.wireOp",EDGE,"E23.59.4"),sQuery(id+"F0.wireOp",EDGE,"E23.59.5"),sQuery(id+"F0.wireOp",EDGE,"E23.59.6"),sQuery(id+"F0.wireOp",EDGE,"E23.59.7"),sQuery(id+"F0.wireOp",EDGE,"E23.59.8"),sQuery(id+"F0.wireOp",EDGE,"E23.59.9"),sQuery(id+"F0.wireOp",EDGE,"E23.59.10"),sQuery(id+"F0.wireOp",EDGE,"E23.59.11"),sQuery(id+"F0.wireOp",EDGE,"E23.60.0"),sQuery(id+"F0.wireOp",EDGE,"E23.60.1"),sQuery(id+"F0.wireOp",EDGE,"E23.60.2"),sQuery(id+"F0.wireOp",EDGE,"E23.60.3"),sQuery(id+"F0.wireOp",EDGE,"E23.60.4"),sQuery(id+"F0.wireOp",EDGE,"E23.60.5"),sQuery(id+"F0.wireOp",EDGE,"E23.60.6"),sQuery(id+"F0.wireOp",EDGE,"E23.60.7"),sQuery(id+"F0.wireOp",EDGE,"E23.60.8"),sQuery(id+"F0.wireOp",EDGE,"E23.60.9"),sQuery(id+"F0.wireOp",EDGE,"E23.60.10"),sQuery(id+"F0.wireOp",EDGE,"E23.60.11"),sQuery(id+"F0.wireOp",EDGE,"E23.61.0"),sQuery(id+"F0.wireOp",EDGE,"E23.61.1"),sQuery(id+"F0.wireOp",EDGE,"E23.61.2"),sQuery(id+"F0.wireOp",EDGE,"E23.61.3"),sQuery(id+"F0.wireOp",EDGE,"E23.61.4"),sQuery(id+"F0.wireOp",EDGE,"E23.61.5"),sQuery(id+"F0.wireOp",EDGE,"E23.61.6"),sQuery(id+"F0.wireOp",EDGE,"E23.61.7"),sQuery(id+"F0.wireOp",EDGE,"E23.61.8"),sQuery(id+"F0.wireOp",EDGE,"E23.61.9"),sQuery(id+"F0.wireOp",EDGE,"E23.61.10"),sQuery(id+"F0.wireOp",EDGE,"E23.61.11"),sQuery(id+"F0.wireOp",EDGE,"E23.62.0"),sQuery(id+"F0.wireOp",EDGE,"E23.62.1"),sQuery(id+"F0.wireOp",EDGE,"E23.62.2"),sQuery(id+"F0.wireOp",EDGE,"E23.62.3"),sQuery(id+"F0.wireOp",EDGE,"E23.62.4"),sQuery(id+"F0.wireOp",EDGE,"E23.62.5"),sQuery(id+"F0.wireOp",EDGE,"E23.62.6"),sQuery(id+"F0.wireOp",EDGE,"E23.62.7"),sQuery(id+"F0.wireOp",EDGE,"E23.62.8"),sQuery(id+"F0.wireOp",EDGE,"E23.62.9"),sQuery(id+"F0.wireOp",EDGE,"E23.62.10"),sQuery(id+"F0.wireOp",EDGE,"E23.62.11"),sQuery(id+"F0.wireOp",EDGE,"E23.63.0"),sQuery(id+"F0.wireOp",EDGE,"E23.63.1"),sQuery(id+"F0.wireOp",EDGE,"E23.63.2"),sQuery(id+"F0.wireOp",EDGE,"E23.63.3"),sQuery(id+"F0.wireOp",EDGE,"E23.63.4"),sQuery(id+"F0.wireOp",EDGE,"E23.63.5"),sQuery(id+"F0.wireOp",EDGE,"E23.63.6"),sQuery(id+"F0.wireOp",EDGE,"E23.63.7"),sQuery(id+"F0.wireOp",EDGE,"E23.63.8"),sQuery(id+"F0.wireOp",EDGE,"E23.63.9"),sQuery(id+"F0.wireOp",EDGE,"E23.63.10"),sQuery(id+"F0.wireOp",EDGE,"E23.63.11"),sQuery(id+"F0.wireOp",EDGE,"E23.64.0"),sQuery(id+"F0.wireOp",EDGE,"E23.64.1"),sQuery(id+"F0.wireOp",EDGE,"E23.64.2"),sQuery(id+"F0.wireOp",EDGE,"E23.64.3"),sQuery(id+"F0.wireOp",EDGE,"E23.64.4"),sQuery(id+"F0.wireOp",EDGE,"E23.64.5"),sQuery(id+"F0.wireOp",EDGE,"E23.64.6"),sQuery(id+"F0.wireOp",EDGE,"E23.64.7"),sQuery(id+"F0.wireOp",EDGE,"E23.64.8"),sQuery(id+"F0.wireOp",EDGE,"E23.64.9"),sQuery(id+"F0.wireOp",EDGE,"E23.64.10"),sQuery(id+"F0.wireOp",EDGE,"E23.64.11"),sQuery(id+"F0.wireOp",EDGE,"E23.65.0"),sQuery(id+"F0.wireOp",EDGE,"E23.65.1"),sQuery(id+"F0.wireOp",EDGE,"E23.65.2"),sQuery(id+"F0.wireOp",EDGE,"E23.65.3"),sQuery(id+"F0.wireOp",EDGE,"E23.65.4"),sQuery(id+"F0.wireOp",EDGE,"E23.65.5"),sQuery(id+"F0.wireOp",EDGE,"E23.65.6"),sQuery(id+"F0.wireOp",EDGE,"E23.65.7"),sQuery(id+"F0.wireOp",EDGE,"E23.65.8"),sQuery(id+"F0.wireOp",EDGE,"E23.65.9"),sQuery(id+"F0.wireOp",EDGE,"E23.65.10"),sQuery(id+"F0.wireOp",EDGE,"E23.65.11"),sQuery(id+"F0.wireOp",EDGE,"E23.66.0"),sQuery(id+"F0.wireOp",EDGE,"E23.66.1"),sQuery(id+"F0.wireOp",EDGE,"E23.66.2"),sQuery(id+"F0.wireOp",EDGE,"E23.66.3"),sQuery(id+"F0.wireOp",EDGE,"E23.66.4"),sQuery(id+"F0.wireOp",EDGE,"E23.66.5"),sQuery(id+"F0.wireOp",EDGE,"E23.66.6"),sQuery(id+"F0.wireOp",EDGE,"E23.66.7"),sQuery(id+"F0.wireOp",EDGE,"E23.66.8"),sQuery(id+"F0.wireOp",EDGE,"E23.66.9"),sQuery(id+"F0.wireOp",EDGE,"E23.66.10"),sQuery(id+"F0.wireOp",EDGE,"E23.66.11"),sQuery(id+"F0.wireOp",EDGE,"E23.67.0"),sQuery(id+"F0.wireOp",EDGE,"E23.67.1"),sQuery(id+"F0.wireOp",EDGE,"E23.67.2"),sQuery(id+"F0.wireOp",EDGE,"E23.67.3"),sQuery(id+"F0.wireOp",EDGE,"E23.67.4"),sQuery(id+"F0.wireOp",EDGE,"E23.67.5"),sQuery(id+"F0.wireOp",EDGE,"E23.67.6"),sQuery(id+"F0.wireOp",EDGE,"E23.67.7"),sQuery(id+"F0.wireOp",EDGE,"E23.67.8"),sQuery(id+"F0.wireOp",EDGE,"E23.67.9"),sQuery(id+"F0.wireOp",EDGE,"E23.67.10"),sQuery(id+"F0.wireOp",EDGE,"E23.67.11"),sQuery(id+"F0.wireOp",EDGE,"E23.68.0"),sQuery(id+"F0.wireOp",EDGE,"E23.68.1"),sQuery(id+"F0.wireOp",EDGE,"E23.68.2"),sQuery(id+"F0.wireOp",EDGE,"E23.68.3"),sQuery(id+"F0.wireOp",EDGE,"E23.68.4"),sQuery(id+"F0.wireOp",EDGE,"E23.68.5"),sQuery(id+"F0.wireOp",EDGE,"E23.68.6"),sQuery(id+"F0.wireOp",EDGE,"E23.68.7"),sQuery(id+"F0.wireOp",EDGE,"E23.68.8"),sQuery(id+"F0.wireOp",EDGE,"E23.68.9"),sQuery(id+"F0.wireOp",EDGE,"E23.68.10"),sQuery(id+"F0.wireOp",EDGE,"E23.68.11"),sQuery(id+"F0.wireOp",EDGE,"E23.69.0"),sQuery(id+"F0.wireOp",EDGE,"E23.69.1"),sQuery(id+"F0.wireOp",EDGE,"E23.69.2"),sQuery(id+"F0.wireOp",EDGE,"E23.69.3"),sQuery(id+"F0.wireOp",EDGE,"E23.69.4"),sQuery(id+"F0.wireOp",EDGE,"E23.69.5"),sQuery(id+"F0.wireOp",EDGE,"E23.69.6"),sQuery(id+"F0.wireOp",EDGE,"E23.69.7"),sQuery(id+"F0.wireOp",EDGE,"E23.69.8"),sQuery(id+"F0.wireOp",EDGE,"E23.69.9"),sQuery(id+"F0.wireOp",EDGE,"E23.69.10"),sQuery(id+"F0.wireOp",EDGE,"E23.69.11"),sQuery(id+"F0.wireOp",EDGE,"E23.70.0"),sQuery(id+"F0.wireOp",EDGE,"E23.70.1"),sQuery(id+"F0.wireOp",EDGE,"E23.70.2"),sQuery(id+"F0.wireOp",EDGE,"E23.70.3"),sQuery(id+"F0.wireOp",EDGE,"E23.70.4"),sQuery(id+"F0.wireOp",EDGE,"E23.70.5"),sQuery(id+"F0.wireOp",EDGE,"E23.70.6"),sQuery(id+"F0.wireOp",EDGE,"E23.70.7"),sQuery(id+"F0.wireOp",EDGE,"E23.70.8"),sQuery(id+"F0.wireOp",EDGE,"E23.70.9"),sQuery(id+"F0.wireOp",EDGE,"E23.70.10"),sQuery(id+"F0.wireOp",EDGE,"E23.70.11"),sQuery(id+"F0.wireOp",EDGE,"E23.71.0"),sQuery(id+"F0.wireOp",EDGE,"E23.71.1"),sQuery(id+"F0.wireOp",EDGE,"E23.71.2"),sQuery(id+"F0.wireOp",EDGE,"E23.71.3"),sQuery(id+"F0.wireOp",EDGE,"E23.71.4"),sQuery(id+"F0.wireOp",EDGE,"E23.71.5"),sQuery(id+"F0.wireOp",EDGE,"E23.71.6"),sQuery(id+"F0.wireOp",EDGE,"E23.71.7"),sQuery(id+"F0.wireOp",EDGE,"E23.71.8"),sQuery(id+"F0.wireOp",EDGE,"E23.71.9"),sQuery(id+"F0.wireOp",EDGE,"E23.71.10"),sQuery(id+"F0.wireOp",EDGE,"E23.71.11"),sQuery(id+"F0.wireOp",EDGE,"E24.trimOffspring"),sQuery(id+"F0.wireOp",EDGE,"E25.trimOffspring"),sQuery(id+"F0.wireOp",EDGE,"E26.trimOffspring"),sQuery(id+"F0.wireOp",EDGE,"E27.trimOffspring"),sQuery(id+"F0.wireOp",EDGE,"E28.trimOffspring"),sQuery(id+"F0.wireOp",EDGE,"E29.trimOffspring"),sQuery(id+"F0.wireOp",EDGE,"E30.trimOffspring"),sQuery(id+"F0.wireOp",EDGE,"E31.trimOffspring"),sQuery(id+"F0.wireOp",EDGE,"E32.trimOffspring"),sQuery(id+"F0.wireOp",EDGE,"E33.trimOffspring"),sQuery(id+"F0.wireOp",EDGE,"E34.trimOffspring"),sQuery(id+"F0.wireOp",EDGE,"E35.trimOffspring"),sQuery(id+"F0.wireOp",EDGE,"E36.trimOffspring"),sQuery(id+"F0.wireOp",EDGE,"E37.trimOffspring"),sQuery(id+"F0.wireOp",EDGE,"E38.trimOffspring"),sQuery(id+"F0.wireOp",EDGE,"E39.trimOffspring"),sQuery(id+"F0.wireOp",EDGE,"E40.trimOffspring"),sQuery(id+"F0.wireOp",EDGE,"E41.trimOffspring"),sQuery(id+"F0.wireOp",EDGE,"E42.trimOffspring"),sQuery(id+"F0.wireOp",EDGE,"E43.trimOffspring"),sQuery(id+"F0.wireOp",EDGE,"E44.trimOffspring"),sQuery(id+"F0.wireOp",EDGE,"E45.trimOffspring"),sQuery(id+"F0.wireOp",EDGE,"E46.trimOffspring"),sQuery(id+"F0.wireOp",EDGE,"E47.trimOffspring"),sQuery(id+"F0.wireOp",EDGE,"E48.trimOffspring"),sQuery(id+"F0.wireOp",EDGE,"E49.trimOffspring"),sQuery(id+"F0.wireOp",EDGE,"E50.trimOffspring"),sQuery(id+"F0.wireOp",EDGE,"E51.trimOffspring"),sQuery(id+"F0.wireOp",EDGE,"E52.trimOffspring"),sQuery(id+"F0.wireOp",EDGE,"E53.trimOffspring"),sQuery(id+"F0.wireOp",EDGE,"E54.trimOffspring"),sQuery(id+"F0.wireOp",EDGE,"E55.trimOffspring"),sQuery(id+"F0.wireOp",EDGE,"E56.trimOffspring"),sQuery(id+"F0.wireOp",EDGE,"E57.trimOffspring"),sQuery(id+"F0.wireOp",EDGE,"E58.trimOffspring"),sQuery(id+"F0.wireOp",EDGE,"E59.trimOffspring"),sQuery(id+"F0.wireOp",EDGE,"E60.trimOffspring"),sQuery(id+"F0.wireOp",EDGE,"E61.trimOffspring"),sQuery(id+"F0.wireOp",EDGE,"E62.trimOffspring"),sQuery(id+"F0.wireOp",EDGE,"E63.trimOffspring"),sQuery(id+"F0.wireOp",EDGE,"E64.trimOffspring"),sQuery(id+"F0.wireOp",EDGE,"E65.trimOffspring"),sQuery(id+"F0.wireOp",EDGE,"E66.trimOffspring"),sQuery(id+"F0.wireOp",EDGE,"E67.trimOffspring"),sQuery(id+"F0.wireOp",EDGE,"E68.trimOffspring"),sQuery(id+"F0.wireOp",EDGE,"E69.trimOffspring"),sQuery(id+"F0.wireOp",EDGE,"E70.trimOffspring"),sQuery(id+"F0.wireOp",EDGE,"E71.trimOffspring"),sQuery(id+"F0.wireOp",EDGE,"E72.trimOffspring"),sQuery(id+"F0.wireOp",EDGE,"E73.trimOffspring"),sQuery(id+"F0.wireOp",EDGE,"E74.trimOffspring"),sQuery(id+"F0.wireOp",EDGE,"E75.trimOffspring"),sQuery(id+"F0.wireOp",EDGE,"E76.trimOffspring"),sQuery(id+"F0.wireOp",EDGE,"E77.trimOffspring"),sQuery(id+"F0.wireOp",EDGE,"E78.trimOffspring"),sQuery(id+"F0.wireOp",EDGE,"E79.trimOffspring"),sQuery(id+"F0.wireOp",EDGE,"E80.trimOffspring"),sQuery(id+"F0.wireOp",EDGE,"E81.trimOffspring"),sQuery(id+"F0.wireOp",EDGE,"E82.trimOffspring"),sQuery(id+"F0.wireOp",EDGE,"E83.trimOffspring"),sQuery(id+"F0.wireOp",EDGE,"E84.trimOffspring"),sQuery(id+"F0.wireOp",EDGE,"E85.trimOffspring"),sQuery(id+"F0.wireOp",EDGE,"E86.trimOffspring"),sQuery(id+"F0.wireOp",EDGE,"E87.trimOffspring"),sQuery(id+"F0.wireOp",EDGE,"E88.trimOffspring"),sQuery(id+"F0.wireOp",EDGE,"E89.trimOffspring"),sQuery(id+"F0.wireOp",EDGE,"E90.trimOffspring"),sQuery(id+"F0.wireOp",EDGE,"E91.trimOffspring"),sQuery(id+"F0.wireOp",EDGE,"E92.trimOffspring"),sQuery(id+"F0.wireOp",EDGE,"E93.trimOffspring"),sQuery(id+"F0.wireOp",EDGE,"E94")])],"isStart":false});
            var sketch = newSketch(context, id + "F3", { "sketchPlane" : qUnion([Q0])});
            skCircle(sketch, "E95", {"center": v(50.8, 0) * mm, "radius": 3.18 * mm});
            skCircle(sketch, "E96.1.0", {"center": v(-25.4, 44) * mm, "radius": 3.18 * mm});
            skCircle(sketch, "E96.2.0", {"center": v(-25.4, -44) * mm, "radius": 3.18 * mm});
            skPoint(sketch, "E96.center", {"position": v(0, 0) * mm});
            skSolve(sketch);
        }
        {
            var Q0;
            Q0 = qSketchRegion(id + "F3", true);
            extrude(context, id + "F4", {"entities" : qUnion([Q0]), "operationType" : NewBodyOperationType.ADD, "depth" : 12.7 * mm});
        }
        {
            var Q0;
            Q0=makeQuery(id+"F1.opExtrude","CAP_FACE",FACE,{"disambiguationData":[OSD([sQuery(id+"F0.wireOp",EDGE,"E0"),sQuery(id+"F0.wireOp",EDGE,"E1.MirrorCS"),sQuery(id+"F0.wireOp",EDGE,"E2.MirrorCS"),sQuery(id+"F0.wireOp",EDGE,"E3.MirrorCS"),sQuery(id+"F0.wireOp",EDGE,"E4.MirrorCS"),sQuery(id+"F0.wireOp",EDGE,"E5.MirrorCS"),sQuery(id+"F0.wireOp",EDGE,"E6.MirrorCS"),sQuery(id+"F0.wireOp",EDGE,"E16.filletArc"),sQuery(id+"F0.wireOp",EDGE,"E17.filletArc"),sQuery(id+"F0.wireOp",EDGE,"E18.filletArc"),sQuery(id+"F0.wireOp",EDGE,"E19.filletArc"),sQuery(id+"F0.wireOp",EDGE,"E20.filletArc"),sQuery(id+"F0.wireOp",EDGE,"E21.filletArc"),sQuery(id+"F0.wireOp",EDGE,"E23.1.0"),sQuery(id+"F0.wireOp",EDGE,"E23.1.1"),sQuery(id+"F0.wireOp",EDGE,"E23.1.2"),sQuery(id+"F0.wireOp",EDGE,"E23.1.3"),sQuery(id+"F0.wireOp",EDGE,"E23.1.4"),sQuery(id+"F0.wireOp",EDGE,"E23.1.5"),sQuery(id+"F0.wireOp",EDGE,"E23.1.6"),sQuery(id+"F0.wireOp",EDGE,"E23.1.7"),sQuery(id+"F0.wireOp",EDGE,"E23.1.8"),sQuery(id+"F0.wireOp",EDGE,"E23.1.9"),sQuery(id+"F0.wireOp",EDGE,"E23.1.10"),sQuery(id+"F0.wireOp",EDGE,"E23.1.11"),sQuery(id+"F0.wireOp",EDGE,"E23.2.0"),sQuery(id+"F0.wireOp",EDGE,"E23.2.1"),sQuery(id+"F0.wireOp",EDGE,"E23.2.2"),sQuery(id+"F0.wireOp",EDGE,"E23.2.3"),sQuery(id+"F0.wireOp",EDGE,"E23.2.4"),sQuery(id+"F0.wireOp",EDGE,"E23.2.5"),sQuery(id+"F0.wireOp",EDGE,"E23.2.6"),sQuery(id+"F0.wireOp",EDGE,"E23.2.7"),sQuery(id+"F0.wireOp",EDGE,"E23.2.8"),sQuery(id+"F0.wireOp",EDGE,"E23.2.9"),sQuery(id+"F0.wireOp",EDGE,"E23.2.10"),sQuery(id+"F0.wireOp",EDGE,"E23.2.11"),sQuery(id+"F0.wireOp",EDGE,"E23.3.0"),sQuery(id+"F0.wireOp",EDGE,"E23.3.1"),sQuery(id+"F0.wireOp",EDGE,"E23.3.2"),sQuery(id+"F0.wireOp",EDGE,"E23.3.3"),sQuery(id+"F0.wireOp",EDGE,"E23.3.4"),sQuery(id+"F0.wireOp",EDGE,"E23.3.5"),sQuery(id+"F0.wireOp",EDGE,"E23.3.6"),sQuery(id+"F0.wireOp",EDGE,"E23.3.7"),sQuery(id+"F0.wireOp",EDGE,"E23.3.8"),sQuery(id+"F0.wireOp",EDGE,"E23.3.9"),sQuery(id+"F0.wireOp",EDGE,"E23.3.10"),sQuery(id+"F0.wireOp",EDGE,"E23.3.11"),sQuery(id+"F0.wireOp",EDGE,"E23.4.0"),sQuery(id+"F0.wireOp",EDGE,"E23.4.1"),sQuery(id+"F0.wireOp",EDGE,"E23.4.2"),sQuery(id+"F0.wireOp",EDGE,"E23.4.3"),sQuery(id+"F0.wireOp",EDGE,"E23.4.4"),sQuery(id+"F0.wireOp",EDGE,"E23.4.5"),sQuery(id+"F0.wireOp",EDGE,"E23.4.6"),sQuery(id+"F0.wireOp",EDGE,"E23.4.7"),sQuery(id+"F0.wireOp",EDGE,"E23.4.8"),sQuery(id+"F0.wireOp",EDGE,"E23.4.9"),sQuery(id+"F0.wireOp",EDGE,"E23.4.10"),sQuery(id+"F0.wireOp",EDGE,"E23.4.11"),sQuery(id+"F0.wireOp",EDGE,"E23.5.0"),sQuery(id+"F0.wireOp",EDGE,"E23.5.1"),sQuery(id+"F0.wireOp",EDGE,"E23.5.2"),sQuery(id+"F0.wireOp",EDGE,"E23.5.3"),sQuery(id+"F0.wireOp",EDGE,"E23.5.4"),sQuery(id+"F0.wireOp",EDGE,"E23.5.5"),sQuery(id+"F0.wireOp",EDGE,"E23.5.6"),sQuery(id+"F0.wireOp",EDGE,"E23.5.7"),sQuery(id+"F0.wireOp",EDGE,"E23.5.8"),sQuery(id+"F0.wireOp",EDGE,"E23.5.9"),sQuery(id+"F0.wireOp",EDGE,"E23.5.10"),sQuery(id+"F0.wireOp",EDGE,"E23.5.11"),sQuery(id+"F0.wireOp",EDGE,"E23.6.0"),sQuery(id+"F0.wireOp",EDGE,"E23.6.1"),sQuery(id+"F0.wireOp",EDGE,"E23.6.2"),sQuery(id+"F0.wireOp",EDGE,"E23.6.3"),sQuery(id+"F0.wireOp",EDGE,"E23.6.4"),sQuery(id+"F0.wireOp",EDGE,"E23.6.5"),sQuery(id+"F0.wireOp",EDGE,"E23.6.6"),sQuery(id+"F0.wireOp",EDGE,"E23.6.7"),sQuery(id+"F0.wireOp",EDGE,"E23.6.8"),sQuery(id+"F0.wireOp",EDGE,"E23.6.9"),sQuery(id+"F0.wireOp",EDGE,"E23.6.10"),sQuery(id+"F0.wireOp",EDGE,"E23.6.11"),sQuery(id+"F0.wireOp",EDGE,"E23.7.0"),sQuery(id+"F0.wireOp",EDGE,"E23.7.1"),sQuery(id+"F0.wireOp",EDGE,"E23.7.2"),sQuery(id+"F0.wireOp",EDGE,"E23.7.3"),sQuery(id+"F0.wireOp",EDGE,"E23.7.4"),sQuery(id+"F0.wireOp",EDGE,"E23.7.5"),sQuery(id+"F0.wireOp",EDGE,"E23.7.6"),sQuery(id+"F0.wireOp",EDGE,"E23.7.7"),sQuery(id+"F0.wireOp",EDGE,"E23.7.8"),sQuery(id+"F0.wireOp",EDGE,"E23.7.9"),sQuery(id+"F0.wireOp",EDGE,"E23.7.10"),sQuery(id+"F0.wireOp",EDGE,"E23.7.11"),sQuery(id+"F0.wireOp",EDGE,"E23.8.0"),sQuery(id+"F0.wireOp",EDGE,"E23.8.1"),sQuery(id+"F0.wireOp",EDGE,"E23.8.2"),sQuery(id+"F0.wireOp",EDGE,"E23.8.3"),sQuery(id+"F0.wireOp",EDGE,"E23.8.4"),sQuery(id+"F0.wireOp",EDGE,"E23.8.5"),sQuery(id+"F0.wireOp",EDGE,"E23.8.6"),sQuery(id+"F0.wireOp",EDGE,"E23.8.7"),sQuery(id+"F0.wireOp",EDGE,"E23.8.8"),sQuery(id+"F0.wireOp",EDGE,"E23.8.9"),sQuery(id+"F0.wireOp",EDGE,"E23.8.10"),sQuery(id+"F0.wireOp",EDGE,"E23.8.11"),sQuery(id+"F0.wireOp",EDGE,"E23.9.0"),sQuery(id+"F0.wireOp",EDGE,"E23.9.1"),sQuery(id+"F0.wireOp",EDGE,"E23.9.2"),sQuery(id+"F0.wireOp",EDGE,"E23.9.3"),sQuery(id+"F0.wireOp",EDGE,"E23.9.4"),sQuery(id+"F0.wireOp",EDGE,"E23.9.5"),sQuery(id+"F0.wireOp",EDGE,"E23.9.6"),sQuery(id+"F0.wireOp",EDGE,"E23.9.7"),sQuery(id+"F0.wireOp",EDGE,"E23.9.8"),sQuery(id+"F0.wireOp",EDGE,"E23.9.9"),sQuery(id+"F0.wireOp",EDGE,"E23.9.10"),sQuery(id+"F0.wireOp",EDGE,"E23.9.11"),sQuery(id+"F0.wireOp",EDGE,"E23.10.0"),sQuery(id+"F0.wireOp",EDGE,"E23.10.1"),sQuery(id+"F0.wireOp",EDGE,"E23.10.2"),sQuery(id+"F0.wireOp",EDGE,"E23.10.3"),sQuery(id+"F0.wireOp",EDGE,"E23.10.4"),sQuery(id+"F0.wireOp",EDGE,"E23.10.5"),sQuery(id+"F0.wireOp",EDGE,"E23.10.6"),sQuery(id+"F0.wireOp",EDGE,"E23.10.7"),sQuery(id+"F0.wireOp",EDGE,"E23.10.8"),sQuery(id+"F0.wireOp",EDGE,"E23.10.9"),sQuery(id+"F0.wireOp",EDGE,"E23.10.10"),sQuery(id+"F0.wireOp",EDGE,"E23.10.11"),sQuery(id+"F0.wireOp",EDGE,"E23.11.0"),sQuery(id+"F0.wireOp",EDGE,"E23.11.1"),sQuery(id+"F0.wireOp",EDGE,"E23.11.2"),sQuery(id+"F0.wireOp",EDGE,"E23.11.3"),sQuery(id+"F0.wireOp",EDGE,"E23.11.4"),sQuery(id+"F0.wireOp",EDGE,"E23.11.5"),sQuery(id+"F0.wireOp",EDGE,"E23.11.6"),sQuery(id+"F0.wireOp",EDGE,"E23.11.7"),sQuery(id+"F0.wireOp",EDGE,"E23.11.8"),sQuery(id+"F0.wireOp",EDGE,"E23.11.9"),sQuery(id+"F0.wireOp",EDGE,"E23.11.10"),sQuery(id+"F0.wireOp",EDGE,"E23.11.11"),sQuery(id+"F0.wireOp",EDGE,"E23.12.0"),sQuery(id+"F0.wireOp",EDGE,"E23.12.1"),sQuery(id+"F0.wireOp",EDGE,"E23.12.2"),sQuery(id+"F0.wireOp",EDGE,"E23.12.3"),sQuery(id+"F0.wireOp",EDGE,"E23.12.4"),sQuery(id+"F0.wireOp",EDGE,"E23.12.5"),sQuery(id+"F0.wireOp",EDGE,"E23.12.6"),sQuery(id+"F0.wireOp",EDGE,"E23.12.7"),sQuery(id+"F0.wireOp",EDGE,"E23.12.8"),sQuery(id+"F0.wireOp",EDGE,"E23.12.9"),sQuery(id+"F0.wireOp",EDGE,"E23.12.10"),sQuery(id+"F0.wireOp",EDGE,"E23.12.11"),sQuery(id+"F0.wireOp",EDGE,"E23.13.0"),sQuery(id+"F0.wireOp",EDGE,"E23.13.1"),sQuery(id+"F0.wireOp",EDGE,"E23.13.2"),sQuery(id+"F0.wireOp",EDGE,"E23.13.3"),sQuery(id+"F0.wireOp",EDGE,"E23.13.4"),sQuery(id+"F0.wireOp",EDGE,"E23.13.5"),sQuery(id+"F0.wireOp",EDGE,"E23.13.6"),sQuery(id+"F0.wireOp",EDGE,"E23.13.7"),sQuery(id+"F0.wireOp",EDGE,"E23.13.8"),sQuery(id+"F0.wireOp",EDGE,"E23.13.9"),sQuery(id+"F0.wireOp",EDGE,"E23.13.10"),sQuery(id+"F0.wireOp",EDGE,"E23.13.11"),sQuery(id+"F0.wireOp",EDGE,"E23.14.0"),sQuery(id+"F0.wireOp",EDGE,"E23.14.1"),sQuery(id+"F0.wireOp",EDGE,"E23.14.2"),sQuery(id+"F0.wireOp",EDGE,"E23.14.3"),sQuery(id+"F0.wireOp",EDGE,"E23.14.4"),sQuery(id+"F0.wireOp",EDGE,"E23.14.5"),sQuery(id+"F0.wireOp",EDGE,"E23.14.6"),sQuery(id+"F0.wireOp",EDGE,"E23.14.7"),sQuery(id+"F0.wireOp",EDGE,"E23.14.8"),sQuery(id+"F0.wireOp",EDGE,"E23.14.9"),sQuery(id+"F0.wireOp",EDGE,"E23.14.10"),sQuery(id+"F0.wireOp",EDGE,"E23.14.11"),sQuery(id+"F0.wireOp",EDGE,"E23.15.0"),sQuery(id+"F0.wireOp",EDGE,"E23.15.1"),sQuery(id+"F0.wireOp",EDGE,"E23.15.2"),sQuery(id+"F0.wireOp",EDGE,"E23.15.3"),sQuery(id+"F0.wireOp",EDGE,"E23.15.4"),sQuery(id+"F0.wireOp",EDGE,"E23.15.5"),sQuery(id+"F0.wireOp",EDGE,"E23.15.6"),sQuery(id+"F0.wireOp",EDGE,"E23.15.7"),sQuery(id+"F0.wireOp",EDGE,"E23.15.8"),sQuery(id+"F0.wireOp",EDGE,"E23.15.9"),sQuery(id+"F0.wireOp",EDGE,"E23.15.10"),sQuery(id+"F0.wireOp",EDGE,"E23.15.11"),sQuery(id+"F0.wireOp",EDGE,"E23.16.0"),sQuery(id+"F0.wireOp",EDGE,"E23.16.1"),sQuery(id+"F0.wireOp",EDGE,"E23.16.2"),sQuery(id+"F0.wireOp",EDGE,"E23.16.3"),sQuery(id+"F0.wireOp",EDGE,"E23.16.4"),sQuery(id+"F0.wireOp",EDGE,"E23.16.5"),sQuery(id+"F0.wireOp",EDGE,"E23.16.6"),sQuery(id+"F0.wireOp",EDGE,"E23.16.7"),sQuery(id+"F0.wireOp",EDGE,"E23.16.8"),sQuery(id+"F0.wireOp",EDGE,"E23.16.9"),sQuery(id+"F0.wireOp",EDGE,"E23.16.10"),sQuery(id+"F0.wireOp",EDGE,"E23.16.11"),sQuery(id+"F0.wireOp",EDGE,"E23.17.0"),sQuery(id+"F0.wireOp",EDGE,"E23.17.1"),sQuery(id+"F0.wireOp",EDGE,"E23.17.2"),sQuery(id+"F0.wireOp",EDGE,"E23.17.3"),sQuery(id+"F0.wireOp",EDGE,"E23.17.4"),sQuery(id+"F0.wireOp",EDGE,"E23.17.5"),sQuery(id+"F0.wireOp",EDGE,"E23.17.6"),sQuery(id+"F0.wireOp",EDGE,"E23.17.7"),sQuery(id+"F0.wireOp",EDGE,"E23.17.8"),sQuery(id+"F0.wireOp",EDGE,"E23.17.9"),sQuery(id+"F0.wireOp",EDGE,"E23.17.10"),sQuery(id+"F0.wireOp",EDGE,"E23.17.11"),sQuery(id+"F0.wireOp",EDGE,"E23.18.0"),sQuery(id+"F0.wireOp",EDGE,"E23.18.1"),sQuery(id+"F0.wireOp",EDGE,"E23.18.2"),sQuery(id+"F0.wireOp",EDGE,"E23.18.3"),sQuery(id+"F0.wireOp",EDGE,"E23.18.4"),sQuery(id+"F0.wireOp",EDGE,"E23.18.5"),sQuery(id+"F0.wireOp",EDGE,"E23.18.6"),sQuery(id+"F0.wireOp",EDGE,"E23.18.7"),sQuery(id+"F0.wireOp",EDGE,"E23.18.8"),sQuery(id+"F0.wireOp",EDGE,"E23.18.9"),sQuery(id+"F0.wireOp",EDGE,"E23.18.10"),sQuery(id+"F0.wireOp",EDGE,"E23.18.11"),sQuery(id+"F0.wireOp",EDGE,"E23.19.0"),sQuery(id+"F0.wireOp",EDGE,"E23.19.1"),sQuery(id+"F0.wireOp",EDGE,"E23.19.2"),sQuery(id+"F0.wireOp",EDGE,"E23.19.3"),sQuery(id+"F0.wireOp",EDGE,"E23.19.4"),sQuery(id+"F0.wireOp",EDGE,"E23.19.5"),sQuery(id+"F0.wireOp",EDGE,"E23.19.6"),sQuery(id+"F0.wireOp",EDGE,"E23.19.7"),sQuery(id+"F0.wireOp",EDGE,"E23.19.8"),sQuery(id+"F0.wireOp",EDGE,"E23.19.9"),sQuery(id+"F0.wireOp",EDGE,"E23.19.10"),sQuery(id+"F0.wireOp",EDGE,"E23.19.11"),sQuery(id+"F0.wireOp",EDGE,"E23.20.0"),sQuery(id+"F0.wireOp",EDGE,"E23.20.1"),sQuery(id+"F0.wireOp",EDGE,"E23.20.2"),sQuery(id+"F0.wireOp",EDGE,"E23.20.3"),sQuery(id+"F0.wireOp",EDGE,"E23.20.4"),sQuery(id+"F0.wireOp",EDGE,"E23.20.5"),sQuery(id+"F0.wireOp",EDGE,"E23.20.6"),sQuery(id+"F0.wireOp",EDGE,"E23.20.7"),sQuery(id+"F0.wireOp",EDGE,"E23.20.8"),sQuery(id+"F0.wireOp",EDGE,"E23.20.9"),sQuery(id+"F0.wireOp",EDGE,"E23.20.10"),sQuery(id+"F0.wireOp",EDGE,"E23.20.11"),sQuery(id+"F0.wireOp",EDGE,"E23.21.0"),sQuery(id+"F0.wireOp",EDGE,"E23.21.1"),sQuery(id+"F0.wireOp",EDGE,"E23.21.2"),sQuery(id+"F0.wireOp",EDGE,"E23.21.3"),sQuery(id+"F0.wireOp",EDGE,"E23.21.4"),sQuery(id+"F0.wireOp",EDGE,"E23.21.5"),sQuery(id+"F0.wireOp",EDGE,"E23.21.6"),sQuery(id+"F0.wireOp",EDGE,"E23.21.7"),sQuery(id+"F0.wireOp",EDGE,"E23.21.8"),sQuery(id+"F0.wireOp",EDGE,"E23.21.9"),sQuery(id+"F0.wireOp",EDGE,"E23.21.10"),sQuery(id+"F0.wireOp",EDGE,"E23.21.11"),sQuery(id+"F0.wireOp",EDGE,"E23.22.0"),sQuery(id+"F0.wireOp",EDGE,"E23.22.1"),sQuery(id+"F0.wireOp",EDGE,"E23.22.2"),sQuery(id+"F0.wireOp",EDGE,"E23.22.3"),sQuery(id+"F0.wireOp",EDGE,"E23.22.4"),sQuery(id+"F0.wireOp",EDGE,"E23.22.5"),sQuery(id+"F0.wireOp",EDGE,"E23.22.6"),sQuery(id+"F0.wireOp",EDGE,"E23.22.7"),sQuery(id+"F0.wireOp",EDGE,"E23.22.8"),sQuery(id+"F0.wireOp",EDGE,"E23.22.9"),sQuery(id+"F0.wireOp",EDGE,"E23.22.10"),sQuery(id+"F0.wireOp",EDGE,"E23.22.11"),sQuery(id+"F0.wireOp",EDGE,"E23.23.0"),sQuery(id+"F0.wireOp",EDGE,"E23.23.1"),sQuery(id+"F0.wireOp",EDGE,"E23.23.2"),sQuery(id+"F0.wireOp",EDGE,"E23.23.3"),sQuery(id+"F0.wireOp",EDGE,"E23.23.4"),sQuery(id+"F0.wireOp",EDGE,"E23.23.5"),sQuery(id+"F0.wireOp",EDGE,"E23.23.6"),sQuery(id+"F0.wireOp",EDGE,"E23.23.7"),sQuery(id+"F0.wireOp",EDGE,"E23.23.8"),sQuery(id+"F0.wireOp",EDGE,"E23.23.9"),sQuery(id+"F0.wireOp",EDGE,"E23.23.10"),sQuery(id+"F0.wireOp",EDGE,"E23.23.11"),sQuery(id+"F0.wireOp",EDGE,"E23.24.0"),sQuery(id+"F0.wireOp",EDGE,"E23.24.1"),sQuery(id+"F0.wireOp",EDGE,"E23.24.2"),sQuery(id+"F0.wireOp",EDGE,"E23.24.3"),sQuery(id+"F0.wireOp",EDGE,"E23.24.4"),sQuery(id+"F0.wireOp",EDGE,"E23.24.5"),sQuery(id+"F0.wireOp",EDGE,"E23.24.6"),sQuery(id+"F0.wireOp",EDGE,"E23.24.7"),sQuery(id+"F0.wireOp",EDGE,"E23.24.8"),sQuery(id+"F0.wireOp",EDGE,"E23.24.9"),sQuery(id+"F0.wireOp",EDGE,"E23.24.10"),sQuery(id+"F0.wireOp",EDGE,"E23.24.11"),sQuery(id+"F0.wireOp",EDGE,"E23.25.0"),sQuery(id+"F0.wireOp",EDGE,"E23.25.1"),sQuery(id+"F0.wireOp",EDGE,"E23.25.2"),sQuery(id+"F0.wireOp",EDGE,"E23.25.3"),sQuery(id+"F0.wireOp",EDGE,"E23.25.4"),sQuery(id+"F0.wireOp",EDGE,"E23.25.5"),sQuery(id+"F0.wireOp",EDGE,"E23.25.6"),sQuery(id+"F0.wireOp",EDGE,"E23.25.7"),sQuery(id+"F0.wireOp",EDGE,"E23.25.8"),sQuery(id+"F0.wireOp",EDGE,"E23.25.9"),sQuery(id+"F0.wireOp",EDGE,"E23.25.10"),sQuery(id+"F0.wireOp",EDGE,"E23.25.11"),sQuery(id+"F0.wireOp",EDGE,"E23.26.0"),sQuery(id+"F0.wireOp",EDGE,"E23.26.1"),sQuery(id+"F0.wireOp",EDGE,"E23.26.2"),sQuery(id+"F0.wireOp",EDGE,"E23.26.3"),sQuery(id+"F0.wireOp",EDGE,"E23.26.4"),sQuery(id+"F0.wireOp",EDGE,"E23.26.5"),sQuery(id+"F0.wireOp",EDGE,"E23.26.6"),sQuery(id+"F0.wireOp",EDGE,"E23.26.7"),sQuery(id+"F0.wireOp",EDGE,"E23.26.8"),sQuery(id+"F0.wireOp",EDGE,"E23.26.9"),sQuery(id+"F0.wireOp",EDGE,"E23.26.10"),sQuery(id+"F0.wireOp",EDGE,"E23.26.11"),sQuery(id+"F0.wireOp",EDGE,"E23.27.0"),sQuery(id+"F0.wireOp",EDGE,"E23.27.1"),sQuery(id+"F0.wireOp",EDGE,"E23.27.2"),sQuery(id+"F0.wireOp",EDGE,"E23.27.3"),sQuery(id+"F0.wireOp",EDGE,"E23.27.4"),sQuery(id+"F0.wireOp",EDGE,"E23.27.5"),sQuery(id+"F0.wireOp",EDGE,"E23.27.6"),sQuery(id+"F0.wireOp",EDGE,"E23.27.7"),sQuery(id+"F0.wireOp",EDGE,"E23.27.8"),sQuery(id+"F0.wireOp",EDGE,"E23.27.9"),sQuery(id+"F0.wireOp",EDGE,"E23.27.10"),sQuery(id+"F0.wireOp",EDGE,"E23.27.11"),sQuery(id+"F0.wireOp",EDGE,"E23.28.0"),sQuery(id+"F0.wireOp",EDGE,"E23.28.1"),sQuery(id+"F0.wireOp",EDGE,"E23.28.2"),sQuery(id+"F0.wireOp",EDGE,"E23.28.3"),sQuery(id+"F0.wireOp",EDGE,"E23.28.4"),sQuery(id+"F0.wireOp",EDGE,"E23.28.5"),sQuery(id+"F0.wireOp",EDGE,"E23.28.6"),sQuery(id+"F0.wireOp",EDGE,"E23.28.7"),sQuery(id+"F0.wireOp",EDGE,"E23.28.8"),sQuery(id+"F0.wireOp",EDGE,"E23.28.9"),sQuery(id+"F0.wireOp",EDGE,"E23.28.10"),sQuery(id+"F0.wireOp",EDGE,"E23.28.11"),sQuery(id+"F0.wireOp",EDGE,"E23.29.0"),sQuery(id+"F0.wireOp",EDGE,"E23.29.1"),sQuery(id+"F0.wireOp",EDGE,"E23.29.2"),sQuery(id+"F0.wireOp",EDGE,"E23.29.3"),sQuery(id+"F0.wireOp",EDGE,"E23.29.4"),sQuery(id+"F0.wireOp",EDGE,"E23.29.5"),sQuery(id+"F0.wireOp",EDGE,"E23.29.6"),sQuery(id+"F0.wireOp",EDGE,"E23.29.7"),sQuery(id+"F0.wireOp",EDGE,"E23.29.8"),sQuery(id+"F0.wireOp",EDGE,"E23.29.9"),sQuery(id+"F0.wireOp",EDGE,"E23.29.10"),sQuery(id+"F0.wireOp",EDGE,"E23.29.11"),sQuery(id+"F0.wireOp",EDGE,"E23.30.0"),sQuery(id+"F0.wireOp",EDGE,"E23.30.1"),sQuery(id+"F0.wireOp",EDGE,"E23.30.2"),sQuery(id+"F0.wireOp",EDGE,"E23.30.3"),sQuery(id+"F0.wireOp",EDGE,"E23.30.4"),sQuery(id+"F0.wireOp",EDGE,"E23.30.5"),sQuery(id+"F0.wireOp",EDGE,"E23.30.6"),sQuery(id+"F0.wireOp",EDGE,"E23.30.7"),sQuery(id+"F0.wireOp",EDGE,"E23.30.8"),sQuery(id+"F0.wireOp",EDGE,"E23.30.9"),sQuery(id+"F0.wireOp",EDGE,"E23.30.10"),sQuery(id+"F0.wireOp",EDGE,"E23.30.11"),sQuery(id+"F0.wireOp",EDGE,"E23.31.0"),sQuery(id+"F0.wireOp",EDGE,"E23.31.1"),sQuery(id+"F0.wireOp",EDGE,"E23.31.2"),sQuery(id+"F0.wireOp",EDGE,"E23.31.3"),sQuery(id+"F0.wireOp",EDGE,"E23.31.4"),sQuery(id+"F0.wireOp",EDGE,"E23.31.5"),sQuery(id+"F0.wireOp",EDGE,"E23.31.6"),sQuery(id+"F0.wireOp",EDGE,"E23.31.7"),sQuery(id+"F0.wireOp",EDGE,"E23.31.8"),sQuery(id+"F0.wireOp",EDGE,"E23.31.9"),sQuery(id+"F0.wireOp",EDGE,"E23.31.10"),sQuery(id+"F0.wireOp",EDGE,"E23.31.11"),sQuery(id+"F0.wireOp",EDGE,"E23.32.0"),sQuery(id+"F0.wireOp",EDGE,"E23.32.1"),sQuery(id+"F0.wireOp",EDGE,"E23.32.2"),sQuery(id+"F0.wireOp",EDGE,"E23.32.3"),sQuery(id+"F0.wireOp",EDGE,"E23.32.4"),sQuery(id+"F0.wireOp",EDGE,"E23.32.5"),sQuery(id+"F0.wireOp",EDGE,"E23.32.6"),sQuery(id+"F0.wireOp",EDGE,"E23.32.7"),sQuery(id+"F0.wireOp",EDGE,"E23.32.8"),sQuery(id+"F0.wireOp",EDGE,"E23.32.9"),sQuery(id+"F0.wireOp",EDGE,"E23.32.10"),sQuery(id+"F0.wireOp",EDGE,"E23.32.11"),sQuery(id+"F0.wireOp",EDGE,"E23.33.0"),sQuery(id+"F0.wireOp",EDGE,"E23.33.1"),sQuery(id+"F0.wireOp",EDGE,"E23.33.2"),sQuery(id+"F0.wireOp",EDGE,"E23.33.3"),sQuery(id+"F0.wireOp",EDGE,"E23.33.4"),sQuery(id+"F0.wireOp",EDGE,"E23.33.5"),sQuery(id+"F0.wireOp",EDGE,"E23.33.6"),sQuery(id+"F0.wireOp",EDGE,"E23.33.7"),sQuery(id+"F0.wireOp",EDGE,"E23.33.8"),sQuery(id+"F0.wireOp",EDGE,"E23.33.9"),sQuery(id+"F0.wireOp",EDGE,"E23.33.10"),sQuery(id+"F0.wireOp",EDGE,"E23.33.11"),sQuery(id+"F0.wireOp",EDGE,"E23.34.0"),sQuery(id+"F0.wireOp",EDGE,"E23.34.1"),sQuery(id+"F0.wireOp",EDGE,"E23.34.2"),sQuery(id+"F0.wireOp",EDGE,"E23.34.3"),sQuery(id+"F0.wireOp",EDGE,"E23.34.4"),sQuery(id+"F0.wireOp",EDGE,"E23.34.5"),sQuery(id+"F0.wireOp",EDGE,"E23.34.6"),sQuery(id+"F0.wireOp",EDGE,"E23.34.7"),sQuery(id+"F0.wireOp",EDGE,"E23.34.8"),sQuery(id+"F0.wireOp",EDGE,"E23.34.9"),sQuery(id+"F0.wireOp",EDGE,"E23.34.10"),sQuery(id+"F0.wireOp",EDGE,"E23.34.11"),sQuery(id+"F0.wireOp",EDGE,"E23.35.0"),sQuery(id+"F0.wireOp",EDGE,"E23.35.1"),sQuery(id+"F0.wireOp",EDGE,"E23.35.2"),sQuery(id+"F0.wireOp",EDGE,"E23.35.3"),sQuery(id+"F0.wireOp",EDGE,"E23.35.4"),sQuery(id+"F0.wireOp",EDGE,"E23.35.5"),sQuery(id+"F0.wireOp",EDGE,"E23.35.6"),sQuery(id+"F0.wireOp",EDGE,"E23.35.7"),sQuery(id+"F0.wireOp",EDGE,"E23.35.8"),sQuery(id+"F0.wireOp",EDGE,"E23.35.9"),sQuery(id+"F0.wireOp",EDGE,"E23.35.10"),sQuery(id+"F0.wireOp",EDGE,"E23.35.11"),sQuery(id+"F0.wireOp",EDGE,"E23.36.0"),sQuery(id+"F0.wireOp",EDGE,"E23.36.1"),sQuery(id+"F0.wireOp",EDGE,"E23.36.2"),sQuery(id+"F0.wireOp",EDGE,"E23.36.3"),sQuery(id+"F0.wireOp",EDGE,"E23.36.4"),sQuery(id+"F0.wireOp",EDGE,"E23.36.5"),sQuery(id+"F0.wireOp",EDGE,"E23.36.6"),sQuery(id+"F0.wireOp",EDGE,"E23.36.7"),sQuery(id+"F0.wireOp",EDGE,"E23.36.8"),sQuery(id+"F0.wireOp",EDGE,"E23.36.9"),sQuery(id+"F0.wireOp",EDGE,"E23.36.10"),sQuery(id+"F0.wireOp",EDGE,"E23.36.11"),sQuery(id+"F0.wireOp",EDGE,"E23.37.0"),sQuery(id+"F0.wireOp",EDGE,"E23.37.1"),sQuery(id+"F0.wireOp",EDGE,"E23.37.2"),sQuery(id+"F0.wireOp",EDGE,"E23.37.3"),sQuery(id+"F0.wireOp",EDGE,"E23.37.4"),sQuery(id+"F0.wireOp",EDGE,"E23.37.5"),sQuery(id+"F0.wireOp",EDGE,"E23.37.6"),sQuery(id+"F0.wireOp",EDGE,"E23.37.7"),sQuery(id+"F0.wireOp",EDGE,"E23.37.8"),sQuery(id+"F0.wireOp",EDGE,"E23.37.9"),sQuery(id+"F0.wireOp",EDGE,"E23.37.10"),sQuery(id+"F0.wireOp",EDGE,"E23.37.11"),sQuery(id+"F0.wireOp",EDGE,"E23.38.0"),sQuery(id+"F0.wireOp",EDGE,"E23.38.1"),sQuery(id+"F0.wireOp",EDGE,"E23.38.2"),sQuery(id+"F0.wireOp",EDGE,"E23.38.3"),sQuery(id+"F0.wireOp",EDGE,"E23.38.4"),sQuery(id+"F0.wireOp",EDGE,"E23.38.5"),sQuery(id+"F0.wireOp",EDGE,"E23.38.6"),sQuery(id+"F0.wireOp",EDGE,"E23.38.7"),sQuery(id+"F0.wireOp",EDGE,"E23.38.8"),sQuery(id+"F0.wireOp",EDGE,"E23.38.9"),sQuery(id+"F0.wireOp",EDGE,"E23.38.10"),sQuery(id+"F0.wireOp",EDGE,"E23.38.11"),sQuery(id+"F0.wireOp",EDGE,"E23.39.0"),sQuery(id+"F0.wireOp",EDGE,"E23.39.1"),sQuery(id+"F0.wireOp",EDGE,"E23.39.2"),sQuery(id+"F0.wireOp",EDGE,"E23.39.3"),sQuery(id+"F0.wireOp",EDGE,"E23.39.4"),sQuery(id+"F0.wireOp",EDGE,"E23.39.5"),sQuery(id+"F0.wireOp",EDGE,"E23.39.6"),sQuery(id+"F0.wireOp",EDGE,"E23.39.7"),sQuery(id+"F0.wireOp",EDGE,"E23.39.8"),sQuery(id+"F0.wireOp",EDGE,"E23.39.9"),sQuery(id+"F0.wireOp",EDGE,"E23.39.10"),sQuery(id+"F0.wireOp",EDGE,"E23.39.11"),sQuery(id+"F0.wireOp",EDGE,"E23.40.0"),sQuery(id+"F0.wireOp",EDGE,"E23.40.1"),sQuery(id+"F0.wireOp",EDGE,"E23.40.2"),sQuery(id+"F0.wireOp",EDGE,"E23.40.3"),sQuery(id+"F0.wireOp",EDGE,"E23.40.4"),sQuery(id+"F0.wireOp",EDGE,"E23.40.5"),sQuery(id+"F0.wireOp",EDGE,"E23.40.6"),sQuery(id+"F0.wireOp",EDGE,"E23.40.7"),sQuery(id+"F0.wireOp",EDGE,"E23.40.8"),sQuery(id+"F0.wireOp",EDGE,"E23.40.9"),sQuery(id+"F0.wireOp",EDGE,"E23.40.10"),sQuery(id+"F0.wireOp",EDGE,"E23.40.11"),sQuery(id+"F0.wireOp",EDGE,"E23.41.0"),sQuery(id+"F0.wireOp",EDGE,"E23.41.1"),sQuery(id+"F0.wireOp",EDGE,"E23.41.2"),sQuery(id+"F0.wireOp",EDGE,"E23.41.3"),sQuery(id+"F0.wireOp",EDGE,"E23.41.4"),sQuery(id+"F0.wireOp",EDGE,"E23.41.5"),sQuery(id+"F0.wireOp",EDGE,"E23.41.6"),sQuery(id+"F0.wireOp",EDGE,"E23.41.7"),sQuery(id+"F0.wireOp",EDGE,"E23.41.8"),sQuery(id+"F0.wireOp",EDGE,"E23.41.9"),sQuery(id+"F0.wireOp",EDGE,"E23.41.10"),sQuery(id+"F0.wireOp",EDGE,"E23.41.11"),sQuery(id+"F0.wireOp",EDGE,"E23.42.0"),sQuery(id+"F0.wireOp",EDGE,"E23.42.1"),sQuery(id+"F0.wireOp",EDGE,"E23.42.2"),sQuery(id+"F0.wireOp",EDGE,"E23.42.3"),sQuery(id+"F0.wireOp",EDGE,"E23.42.4"),sQuery(id+"F0.wireOp",EDGE,"E23.42.5"),sQuery(id+"F0.wireOp",EDGE,"E23.42.6"),sQuery(id+"F0.wireOp",EDGE,"E23.42.7"),sQuery(id+"F0.wireOp",EDGE,"E23.42.8"),sQuery(id+"F0.wireOp",EDGE,"E23.42.9"),sQuery(id+"F0.wireOp",EDGE,"E23.42.10"),sQuery(id+"F0.wireOp",EDGE,"E23.42.11"),sQuery(id+"F0.wireOp",EDGE,"E23.43.0"),sQuery(id+"F0.wireOp",EDGE,"E23.43.1"),sQuery(id+"F0.wireOp",EDGE,"E23.43.2"),sQuery(id+"F0.wireOp",EDGE,"E23.43.3"),sQuery(id+"F0.wireOp",EDGE,"E23.43.4"),sQuery(id+"F0.wireOp",EDGE,"E23.43.5"),sQuery(id+"F0.wireOp",EDGE,"E23.43.6"),sQuery(id+"F0.wireOp",EDGE,"E23.43.7"),sQuery(id+"F0.wireOp",EDGE,"E23.43.8"),sQuery(id+"F0.wireOp",EDGE,"E23.43.9"),sQuery(id+"F0.wireOp",EDGE,"E23.43.10"),sQuery(id+"F0.wireOp",EDGE,"E23.43.11"),sQuery(id+"F0.wireOp",EDGE,"E23.44.0"),sQuery(id+"F0.wireOp",EDGE,"E23.44.1"),sQuery(id+"F0.wireOp",EDGE,"E23.44.2"),sQuery(id+"F0.wireOp",EDGE,"E23.44.3"),sQuery(id+"F0.wireOp",EDGE,"E23.44.4"),sQuery(id+"F0.wireOp",EDGE,"E23.44.5"),sQuery(id+"F0.wireOp",EDGE,"E23.44.6"),sQuery(id+"F0.wireOp",EDGE,"E23.44.7"),sQuery(id+"F0.wireOp",EDGE,"E23.44.8"),sQuery(id+"F0.wireOp",EDGE,"E23.44.9"),sQuery(id+"F0.wireOp",EDGE,"E23.44.10"),sQuery(id+"F0.wireOp",EDGE,"E23.44.11"),sQuery(id+"F0.wireOp",EDGE,"E23.45.0"),sQuery(id+"F0.wireOp",EDGE,"E23.45.1"),sQuery(id+"F0.wireOp",EDGE,"E23.45.2"),sQuery(id+"F0.wireOp",EDGE,"E23.45.3"),sQuery(id+"F0.wireOp",EDGE,"E23.45.4"),sQuery(id+"F0.wireOp",EDGE,"E23.45.5"),sQuery(id+"F0.wireOp",EDGE,"E23.45.6"),sQuery(id+"F0.wireOp",EDGE,"E23.45.7"),sQuery(id+"F0.wireOp",EDGE,"E23.45.8"),sQuery(id+"F0.wireOp",EDGE,"E23.45.9"),sQuery(id+"F0.wireOp",EDGE,"E23.45.10"),sQuery(id+"F0.wireOp",EDGE,"E23.45.11"),sQuery(id+"F0.wireOp",EDGE,"E23.46.0"),sQuery(id+"F0.wireOp",EDGE,"E23.46.1"),sQuery(id+"F0.wireOp",EDGE,"E23.46.2"),sQuery(id+"F0.wireOp",EDGE,"E23.46.3"),sQuery(id+"F0.wireOp",EDGE,"E23.46.4"),sQuery(id+"F0.wireOp",EDGE,"E23.46.5"),sQuery(id+"F0.wireOp",EDGE,"E23.46.6"),sQuery(id+"F0.wireOp",EDGE,"E23.46.7"),sQuery(id+"F0.wireOp",EDGE,"E23.46.8"),sQuery(id+"F0.wireOp",EDGE,"E23.46.9"),sQuery(id+"F0.wireOp",EDGE,"E23.46.10"),sQuery(id+"F0.wireOp",EDGE,"E23.46.11"),sQuery(id+"F0.wireOp",EDGE,"E23.47.0"),sQuery(id+"F0.wireOp",EDGE,"E23.47.1"),sQuery(id+"F0.wireOp",EDGE,"E23.47.2"),sQuery(id+"F0.wireOp",EDGE,"E23.47.3"),sQuery(id+"F0.wireOp",EDGE,"E23.47.4"),sQuery(id+"F0.wireOp",EDGE,"E23.47.5"),sQuery(id+"F0.wireOp",EDGE,"E23.47.6"),sQuery(id+"F0.wireOp",EDGE,"E23.47.7"),sQuery(id+"F0.wireOp",EDGE,"E23.47.8"),sQuery(id+"F0.wireOp",EDGE,"E23.47.9"),sQuery(id+"F0.wireOp",EDGE,"E23.47.10"),sQuery(id+"F0.wireOp",EDGE,"E23.47.11"),sQuery(id+"F0.wireOp",EDGE,"E23.48.0"),sQuery(id+"F0.wireOp",EDGE,"E23.48.1"),sQuery(id+"F0.wireOp",EDGE,"E23.48.2"),sQuery(id+"F0.wireOp",EDGE,"E23.48.3"),sQuery(id+"F0.wireOp",EDGE,"E23.48.4"),sQuery(id+"F0.wireOp",EDGE,"E23.48.5"),sQuery(id+"F0.wireOp",EDGE,"E23.48.6"),sQuery(id+"F0.wireOp",EDGE,"E23.48.7"),sQuery(id+"F0.wireOp",EDGE,"E23.48.8"),sQuery(id+"F0.wireOp",EDGE,"E23.48.9"),sQuery(id+"F0.wireOp",EDGE,"E23.48.10"),sQuery(id+"F0.wireOp",EDGE,"E23.48.11"),sQuery(id+"F0.wireOp",EDGE,"E23.49.0"),sQuery(id+"F0.wireOp",EDGE,"E23.49.1"),sQuery(id+"F0.wireOp",EDGE,"E23.49.2"),sQuery(id+"F0.wireOp",EDGE,"E23.49.3"),sQuery(id+"F0.wireOp",EDGE,"E23.49.4"),sQuery(id+"F0.wireOp",EDGE,"E23.49.5"),sQuery(id+"F0.wireOp",EDGE,"E23.49.6"),sQuery(id+"F0.wireOp",EDGE,"E23.49.7"),sQuery(id+"F0.wireOp",EDGE,"E23.49.8"),sQuery(id+"F0.wireOp",EDGE,"E23.49.9"),sQuery(id+"F0.wireOp",EDGE,"E23.49.10"),sQuery(id+"F0.wireOp",EDGE,"E23.49.11"),sQuery(id+"F0.wireOp",EDGE,"E23.50.0"),sQuery(id+"F0.wireOp",EDGE,"E23.50.1"),sQuery(id+"F0.wireOp",EDGE,"E23.50.2"),sQuery(id+"F0.wireOp",EDGE,"E23.50.3"),sQuery(id+"F0.wireOp",EDGE,"E23.50.4"),sQuery(id+"F0.wireOp",EDGE,"E23.50.5"),sQuery(id+"F0.wireOp",EDGE,"E23.50.6"),sQuery(id+"F0.wireOp",EDGE,"E23.50.7"),sQuery(id+"F0.wireOp",EDGE,"E23.50.8"),sQuery(id+"F0.wireOp",EDGE,"E23.50.9"),sQuery(id+"F0.wireOp",EDGE,"E23.50.10"),sQuery(id+"F0.wireOp",EDGE,"E23.50.11"),sQuery(id+"F0.wireOp",EDGE,"E23.51.0"),sQuery(id+"F0.wireOp",EDGE,"E23.51.1"),sQuery(id+"F0.wireOp",EDGE,"E23.51.2"),sQuery(id+"F0.wireOp",EDGE,"E23.51.3"),sQuery(id+"F0.wireOp",EDGE,"E23.51.4"),sQuery(id+"F0.wireOp",EDGE,"E23.51.5"),sQuery(id+"F0.wireOp",EDGE,"E23.51.6"),sQuery(id+"F0.wireOp",EDGE,"E23.51.7"),sQuery(id+"F0.wireOp",EDGE,"E23.51.8"),sQuery(id+"F0.wireOp",EDGE,"E23.51.9"),sQuery(id+"F0.wireOp",EDGE,"E23.51.10"),sQuery(id+"F0.wireOp",EDGE,"E23.51.11"),sQuery(id+"F0.wireOp",EDGE,"E23.52.0"),sQuery(id+"F0.wireOp",EDGE,"E23.52.1"),sQuery(id+"F0.wireOp",EDGE,"E23.52.2"),sQuery(id+"F0.wireOp",EDGE,"E23.52.3"),sQuery(id+"F0.wireOp",EDGE,"E23.52.4"),sQuery(id+"F0.wireOp",EDGE,"E23.52.5"),sQuery(id+"F0.wireOp",EDGE,"E23.52.6"),sQuery(id+"F0.wireOp",EDGE,"E23.52.7"),sQuery(id+"F0.wireOp",EDGE,"E23.52.8"),sQuery(id+"F0.wireOp",EDGE,"E23.52.9"),sQuery(id+"F0.wireOp",EDGE,"E23.52.10"),sQuery(id+"F0.wireOp",EDGE,"E23.52.11"),sQuery(id+"F0.wireOp",EDGE,"E23.53.0"),sQuery(id+"F0.wireOp",EDGE,"E23.53.1"),sQuery(id+"F0.wireOp",EDGE,"E23.53.2"),sQuery(id+"F0.wireOp",EDGE,"E23.53.3"),sQuery(id+"F0.wireOp",EDGE,"E23.53.4"),sQuery(id+"F0.wireOp",EDGE,"E23.53.5"),sQuery(id+"F0.wireOp",EDGE,"E23.53.6"),sQuery(id+"F0.wireOp",EDGE,"E23.53.7"),sQuery(id+"F0.wireOp",EDGE,"E23.53.8"),sQuery(id+"F0.wireOp",EDGE,"E23.53.9"),sQuery(id+"F0.wireOp",EDGE,"E23.53.10"),sQuery(id+"F0.wireOp",EDGE,"E23.53.11"),sQuery(id+"F0.wireOp",EDGE,"E23.54.0"),sQuery(id+"F0.wireOp",EDGE,"E23.54.1"),sQuery(id+"F0.wireOp",EDGE,"E23.54.2"),sQuery(id+"F0.wireOp",EDGE,"E23.54.3"),sQuery(id+"F0.wireOp",EDGE,"E23.54.4"),sQuery(id+"F0.wireOp",EDGE,"E23.54.5"),sQuery(id+"F0.wireOp",EDGE,"E23.54.6"),sQuery(id+"F0.wireOp",EDGE,"E23.54.7"),sQuery(id+"F0.wireOp",EDGE,"E23.54.8"),sQuery(id+"F0.wireOp",EDGE,"E23.54.9"),sQuery(id+"F0.wireOp",EDGE,"E23.54.10"),sQuery(id+"F0.wireOp",EDGE,"E23.54.11"),sQuery(id+"F0.wireOp",EDGE,"E23.55.0"),sQuery(id+"F0.wireOp",EDGE,"E23.55.1"),sQuery(id+"F0.wireOp",EDGE,"E23.55.2"),sQuery(id+"F0.wireOp",EDGE,"E23.55.3"),sQuery(id+"F0.wireOp",EDGE,"E23.55.4"),sQuery(id+"F0.wireOp",EDGE,"E23.55.5"),sQuery(id+"F0.wireOp",EDGE,"E23.55.6"),sQuery(id+"F0.wireOp",EDGE,"E23.55.7"),sQuery(id+"F0.wireOp",EDGE,"E23.55.8"),sQuery(id+"F0.wireOp",EDGE,"E23.55.9"),sQuery(id+"F0.wireOp",EDGE,"E23.55.10"),sQuery(id+"F0.wireOp",EDGE,"E23.55.11"),sQuery(id+"F0.wireOp",EDGE,"E23.56.0"),sQuery(id+"F0.wireOp",EDGE,"E23.56.1"),sQuery(id+"F0.wireOp",EDGE,"E23.56.2"),sQuery(id+"F0.wireOp",EDGE,"E23.56.3"),sQuery(id+"F0.wireOp",EDGE,"E23.56.4"),sQuery(id+"F0.wireOp",EDGE,"E23.56.5"),sQuery(id+"F0.wireOp",EDGE,"E23.56.6"),sQuery(id+"F0.wireOp",EDGE,"E23.56.7"),sQuery(id+"F0.wireOp",EDGE,"E23.56.8"),sQuery(id+"F0.wireOp",EDGE,"E23.56.9"),sQuery(id+"F0.wireOp",EDGE,"E23.56.10"),sQuery(id+"F0.wireOp",EDGE,"E23.56.11"),sQuery(id+"F0.wireOp",EDGE,"E23.57.0"),sQuery(id+"F0.wireOp",EDGE,"E23.57.1"),sQuery(id+"F0.wireOp",EDGE,"E23.57.2"),sQuery(id+"F0.wireOp",EDGE,"E23.57.3"),sQuery(id+"F0.wireOp",EDGE,"E23.57.4"),sQuery(id+"F0.wireOp",EDGE,"E23.57.5"),sQuery(id+"F0.wireOp",EDGE,"E23.57.6"),sQuery(id+"F0.wireOp",EDGE,"E23.57.7"),sQuery(id+"F0.wireOp",EDGE,"E23.57.8"),sQuery(id+"F0.wireOp",EDGE,"E23.57.9"),sQuery(id+"F0.wireOp",EDGE,"E23.57.10"),sQuery(id+"F0.wireOp",EDGE,"E23.57.11"),sQuery(id+"F0.wireOp",EDGE,"E23.58.0"),sQuery(id+"F0.wireOp",EDGE,"E23.58.1"),sQuery(id+"F0.wireOp",EDGE,"E23.58.2"),sQuery(id+"F0.wireOp",EDGE,"E23.58.3"),sQuery(id+"F0.wireOp",EDGE,"E23.58.4"),sQuery(id+"F0.wireOp",EDGE,"E23.58.5"),sQuery(id+"F0.wireOp",EDGE,"E23.58.6"),sQuery(id+"F0.wireOp",EDGE,"E23.58.7"),sQuery(id+"F0.wireOp",EDGE,"E23.58.8"),sQuery(id+"F0.wireOp",EDGE,"E23.58.9"),sQuery(id+"F0.wireOp",EDGE,"E23.58.10"),sQuery(id+"F0.wireOp",EDGE,"E23.58.11"),sQuery(id+"F0.wireOp",EDGE,"E23.59.0"),sQuery(id+"F0.wireOp",EDGE,"E23.59.1"),sQuery(id+"F0.wireOp",EDGE,"E23.59.2"),sQuery(id+"F0.wireOp",EDGE,"E23.59.3"),sQuery(id+"F0.wireOp",EDGE,"E23.59.4"),sQuery(id+"F0.wireOp",EDGE,"E23.59.5"),sQuery(id+"F0.wireOp",EDGE,"E23.59.6"),sQuery(id+"F0.wireOp",EDGE,"E23.59.7"),sQuery(id+"F0.wireOp",EDGE,"E23.59.8"),sQuery(id+"F0.wireOp",EDGE,"E23.59.9"),sQuery(id+"F0.wireOp",EDGE,"E23.59.10"),sQuery(id+"F0.wireOp",EDGE,"E23.59.11"),sQuery(id+"F0.wireOp",EDGE,"E23.60.0"),sQuery(id+"F0.wireOp",EDGE,"E23.60.1"),sQuery(id+"F0.wireOp",EDGE,"E23.60.2"),sQuery(id+"F0.wireOp",EDGE,"E23.60.3"),sQuery(id+"F0.wireOp",EDGE,"E23.60.4"),sQuery(id+"F0.wireOp",EDGE,"E23.60.5"),sQuery(id+"F0.wireOp",EDGE,"E23.60.6"),sQuery(id+"F0.wireOp",EDGE,"E23.60.7"),sQuery(id+"F0.wireOp",EDGE,"E23.60.8"),sQuery(id+"F0.wireOp",EDGE,"E23.60.9"),sQuery(id+"F0.wireOp",EDGE,"E23.60.10"),sQuery(id+"F0.wireOp",EDGE,"E23.60.11"),sQuery(id+"F0.wireOp",EDGE,"E23.61.0"),sQuery(id+"F0.wireOp",EDGE,"E23.61.1"),sQuery(id+"F0.wireOp",EDGE,"E23.61.2"),sQuery(id+"F0.wireOp",EDGE,"E23.61.3"),sQuery(id+"F0.wireOp",EDGE,"E23.61.4"),sQuery(id+"F0.wireOp",EDGE,"E23.61.5"),sQuery(id+"F0.wireOp",EDGE,"E23.61.6"),sQuery(id+"F0.wireOp",EDGE,"E23.61.7"),sQuery(id+"F0.wireOp",EDGE,"E23.61.8"),sQuery(id+"F0.wireOp",EDGE,"E23.61.9"),sQuery(id+"F0.wireOp",EDGE,"E23.61.10"),sQuery(id+"F0.wireOp",EDGE,"E23.61.11"),sQuery(id+"F0.wireOp",EDGE,"E23.62.0"),sQuery(id+"F0.wireOp",EDGE,"E23.62.1"),sQuery(id+"F0.wireOp",EDGE,"E23.62.2"),sQuery(id+"F0.wireOp",EDGE,"E23.62.3"),sQuery(id+"F0.wireOp",EDGE,"E23.62.4"),sQuery(id+"F0.wireOp",EDGE,"E23.62.5"),sQuery(id+"F0.wireOp",EDGE,"E23.62.6"),sQuery(id+"F0.wireOp",EDGE,"E23.62.7"),sQuery(id+"F0.wireOp",EDGE,"E23.62.8"),sQuery(id+"F0.wireOp",EDGE,"E23.62.9"),sQuery(id+"F0.wireOp",EDGE,"E23.62.10"),sQuery(id+"F0.wireOp",EDGE,"E23.62.11"),sQuery(id+"F0.wireOp",EDGE,"E23.63.0"),sQuery(id+"F0.wireOp",EDGE,"E23.63.1"),sQuery(id+"F0.wireOp",EDGE,"E23.63.2"),sQuery(id+"F0.wireOp",EDGE,"E23.63.3"),sQuery(id+"F0.wireOp",EDGE,"E23.63.4"),sQuery(id+"F0.wireOp",EDGE,"E23.63.5"),sQuery(id+"F0.wireOp",EDGE,"E23.63.6"),sQuery(id+"F0.wireOp",EDGE,"E23.63.7"),sQuery(id+"F0.wireOp",EDGE,"E23.63.8"),sQuery(id+"F0.wireOp",EDGE,"E23.63.9"),sQuery(id+"F0.wireOp",EDGE,"E23.63.10"),sQuery(id+"F0.wireOp",EDGE,"E23.63.11"),sQuery(id+"F0.wireOp",EDGE,"E23.64.0"),sQuery(id+"F0.wireOp",EDGE,"E23.64.1"),sQuery(id+"F0.wireOp",EDGE,"E23.64.2"),sQuery(id+"F0.wireOp",EDGE,"E23.64.3"),sQuery(id+"F0.wireOp",EDGE,"E23.64.4"),sQuery(id+"F0.wireOp",EDGE,"E23.64.5"),sQuery(id+"F0.wireOp",EDGE,"E23.64.6"),sQuery(id+"F0.wireOp",EDGE,"E23.64.7"),sQuery(id+"F0.wireOp",EDGE,"E23.64.8"),sQuery(id+"F0.wireOp",EDGE,"E23.64.9"),sQuery(id+"F0.wireOp",EDGE,"E23.64.10"),sQuery(id+"F0.wireOp",EDGE,"E23.64.11"),sQuery(id+"F0.wireOp",EDGE,"E23.65.0"),sQuery(id+"F0.wireOp",EDGE,"E23.65.1"),sQuery(id+"F0.wireOp",EDGE,"E23.65.2"),sQuery(id+"F0.wireOp",EDGE,"E23.65.3"),sQuery(id+"F0.wireOp",EDGE,"E23.65.4"),sQuery(id+"F0.wireOp",EDGE,"E23.65.5"),sQuery(id+"F0.wireOp",EDGE,"E23.65.6"),sQuery(id+"F0.wireOp",EDGE,"E23.65.7"),sQuery(id+"F0.wireOp",EDGE,"E23.65.8"),sQuery(id+"F0.wireOp",EDGE,"E23.65.9"),sQuery(id+"F0.wireOp",EDGE,"E23.65.10"),sQuery(id+"F0.wireOp",EDGE,"E23.65.11"),sQuery(id+"F0.wireOp",EDGE,"E23.66.0"),sQuery(id+"F0.wireOp",EDGE,"E23.66.1"),sQuery(id+"F0.wireOp",EDGE,"E23.66.2"),sQuery(id+"F0.wireOp",EDGE,"E23.66.3"),sQuery(id+"F0.wireOp",EDGE,"E23.66.4"),sQuery(id+"F0.wireOp",EDGE,"E23.66.5"),sQuery(id+"F0.wireOp",EDGE,"E23.66.6"),sQuery(id+"F0.wireOp",EDGE,"E23.66.7"),sQuery(id+"F0.wireOp",EDGE,"E23.66.8"),sQuery(id+"F0.wireOp",EDGE,"E23.66.9"),sQuery(id+"F0.wireOp",EDGE,"E23.66.10"),sQuery(id+"F0.wireOp",EDGE,"E23.66.11"),sQuery(id+"F0.wireOp",EDGE,"E23.67.0"),sQuery(id+"F0.wireOp",EDGE,"E23.67.1"),sQuery(id+"F0.wireOp",EDGE,"E23.67.2"),sQuery(id+"F0.wireOp",EDGE,"E23.67.3"),sQuery(id+"F0.wireOp",EDGE,"E23.67.4"),sQuery(id+"F0.wireOp",EDGE,"E23.67.5"),sQuery(id+"F0.wireOp",EDGE,"E23.67.6"),sQuery(id+"F0.wireOp",EDGE,"E23.67.7"),sQuery(id+"F0.wireOp",EDGE,"E23.67.8"),sQuery(id+"F0.wireOp",EDGE,"E23.67.9"),sQuery(id+"F0.wireOp",EDGE,"E23.67.10"),sQuery(id+"F0.wireOp",EDGE,"E23.67.11"),sQuery(id+"F0.wireOp",EDGE,"E23.68.0"),sQuery(id+"F0.wireOp",EDGE,"E23.68.1"),sQuery(id+"F0.wireOp",EDGE,"E23.68.2"),sQuery(id+"F0.wireOp",EDGE,"E23.68.3"),sQuery(id+"F0.wireOp",EDGE,"E23.68.4"),sQuery(id+"F0.wireOp",EDGE,"E23.68.5"),sQuery(id+"F0.wireOp",EDGE,"E23.68.6"),sQuery(id+"F0.wireOp",EDGE,"E23.68.7"),sQuery(id+"F0.wireOp",EDGE,"E23.68.8"),sQuery(id+"F0.wireOp",EDGE,"E23.68.9"),sQuery(id+"F0.wireOp",EDGE,"E23.68.10"),sQuery(id+"F0.wireOp",EDGE,"E23.68.11"),sQuery(id+"F0.wireOp",EDGE,"E23.69.0"),sQuery(id+"F0.wireOp",EDGE,"E23.69.1"),sQuery(id+"F0.wireOp",EDGE,"E23.69.2"),sQuery(id+"F0.wireOp",EDGE,"E23.69.3"),sQuery(id+"F0.wireOp",EDGE,"E23.69.4"),sQuery(id+"F0.wireOp",EDGE,"E23.69.5"),sQuery(id+"F0.wireOp",EDGE,"E23.69.6"),sQuery(id+"F0.wireOp",EDGE,"E23.69.7"),sQuery(id+"F0.wireOp",EDGE,"E23.69.8"),sQuery(id+"F0.wireOp",EDGE,"E23.69.9"),sQuery(id+"F0.wireOp",EDGE,"E23.69.10"),sQuery(id+"F0.wireOp",EDGE,"E23.69.11"),sQuery(id+"F0.wireOp",EDGE,"E23.70.0"),sQuery(id+"F0.wireOp",EDGE,"E23.70.1"),sQuery(id+"F0.wireOp",EDGE,"E23.70.2"),sQuery(id+"F0.wireOp",EDGE,"E23.70.3"),sQuery(id+"F0.wireOp",EDGE,"E23.70.4"),sQuery(id+"F0.wireOp",EDGE,"E23.70.5"),sQuery(id+"F0.wireOp",EDGE,"E23.70.6"),sQuery(id+"F0.wireOp",EDGE,"E23.70.7"),sQuery(id+"F0.wireOp",EDGE,"E23.70.8"),sQuery(id+"F0.wireOp",EDGE,"E23.70.9"),sQuery(id+"F0.wireOp",EDGE,"E23.70.10"),sQuery(id+"F0.wireOp",EDGE,"E23.70.11"),sQuery(id+"F0.wireOp",EDGE,"E23.71.0"),sQuery(id+"F0.wireOp",EDGE,"E23.71.1"),sQuery(id+"F0.wireOp",EDGE,"E23.71.2"),sQuery(id+"F0.wireOp",EDGE,"E23.71.3"),sQuery(id+"F0.wireOp",EDGE,"E23.71.4"),sQuery(id+"F0.wireOp",EDGE,"E23.71.5"),sQuery(id+"F0.wireOp",EDGE,"E23.71.6"),sQuery(id+"F0.wireOp",EDGE,"E23.71.7"),sQuery(id+"F0.wireOp",EDGE,"E23.71.8"),sQuery(id+"F0.wireOp",EDGE,"E23.71.9"),sQuery(id+"F0.wireOp",EDGE,"E23.71.10"),sQuery(id+"F0.wireOp",EDGE,"E23.71.11"),sQuery(id+"F0.wireOp",EDGE,"E24.trimOffspring"),sQuery(id+"F0.wireOp",EDGE,"E25.trimOffspring"),sQuery(id+"F0.wireOp",EDGE,"E26.trimOffspring"),sQuery(id+"F0.wireOp",EDGE,"E27.trimOffspring"),sQuery(id+"F0.wireOp",EDGE,"E28.trimOffspring"),sQuery(id+"F0.wireOp",EDGE,"E29.trimOffspring"),sQuery(id+"F0.wireOp",EDGE,"E30.trimOffspring"),sQuery(id+"F0.wireOp",EDGE,"E31.trimOffspring"),sQuery(id+"F0.wireOp",EDGE,"E32.trimOffspring"),sQuery(id+"F0.wireOp",EDGE,"E33.trimOffspring"),sQuery(id+"F0.wireOp",EDGE,"E34.trimOffspring"),sQuery(id+"F0.wireOp",EDGE,"E35.trimOffspring"),sQuery(id+"F0.wireOp",EDGE,"E36.trimOffspring"),sQuery(id+"F0.wireOp",EDGE,"E37.trimOffspring"),sQuery(id+"F0.wireOp",EDGE,"E38.trimOffspring"),sQuery(id+"F0.wireOp",EDGE,"E39.trimOffspring"),sQuery(id+"F0.wireOp",EDGE,"E40.trimOffspring"),sQuery(id+"F0.wireOp",EDGE,"E41.trimOffspring"),sQuery(id+"F0.wireOp",EDGE,"E42.trimOffspring"),sQuery(id+"F0.wireOp",EDGE,"E43.trimOffspring"),sQuery(id+"F0.wireOp",EDGE,"E44.trimOffspring"),sQuery(id+"F0.wireOp",EDGE,"E45.trimOffspring"),sQuery(id+"F0.wireOp",EDGE,"E46.trimOffspring"),sQuery(id+"F0.wireOp",EDGE,"E47.trimOffspring"),sQuery(id+"F0.wireOp",EDGE,"E48.trimOffspring"),sQuery(id+"F0.wireOp",EDGE,"E49.trimOffspring"),sQuery(id+"F0.wireOp",EDGE,"E50.trimOffspring"),sQuery(id+"F0.wireOp",EDGE,"E51.trimOffspring"),sQuery(id+"F0.wireOp",EDGE,"E52.trimOffspring"),sQuery(id+"F0.wireOp",EDGE,"E53.trimOffspring"),sQuery(id+"F0.wireOp",EDGE,"E54.trimOffspring"),sQuery(id+"F0.wireOp",EDGE,"E55.trimOffspring"),sQuery(id+"F0.wireOp",EDGE,"E56.trimOffspring"),sQuery(id+"F0.wireOp",EDGE,"E57.trimOffspring"),sQuery(id+"F0.wireOp",EDGE,"E58.trimOffspring"),sQuery(id+"F0.wireOp",EDGE,"E59.trimOffspring"),sQuery(id+"F0.wireOp",EDGE,"E60.trimOffspring"),sQuery(id+"F0.wireOp",EDGE,"E61.trimOffspring"),sQuery(id+"F0.wireOp",EDGE,"E62.trimOffspring"),sQuery(id+"F0.wireOp",EDGE,"E63.trimOffspring"),sQuery(id+"F0.wireOp",EDGE,"E64.trimOffspring"),sQuery(id+"F0.wireOp",EDGE,"E65.trimOffspring"),sQuery(id+"F0.wireOp",EDGE,"E66.trimOffspring"),sQuery(id+"F0.wireOp",EDGE,"E67.trimOffspring"),sQuery(id+"F0.wireOp",EDGE,"E68.trimOffspring"),sQuery(id+"F0.wireOp",EDGE,"E69.trimOffspring"),sQuery(id+"F0.wireOp",EDGE,"E70.trimOffspring"),sQuery(id+"F0.wireOp",EDGE,"E71.trimOffspring"),sQuery(id+"F0.wireOp",EDGE,"E72.trimOffspring"),sQuery(id+"F0.wireOp",EDGE,"E73.trimOffspring"),sQuery(id+"F0.wireOp",EDGE,"E74.trimOffspring"),sQuery(id+"F0.wireOp",EDGE,"E75.trimOffspring"),sQuery(id+"F0.wireOp",EDGE,"E76.trimOffspring"),sQuery(id+"F0.wireOp",EDGE,"E77.trimOffspring"),sQuery(id+"F0.wireOp",EDGE,"E78.trimOffspring"),sQuery(id+"F0.wireOp",EDGE,"E79.trimOffspring"),sQuery(id+"F0.wireOp",EDGE,"E80.trimOffspring"),sQuery(id+"F0.wireOp",EDGE,"E81.trimOffspring"),sQuery(id+"F0.wireOp",EDGE,"E82.trimOffspring"),sQuery(id+"F0.wireOp",EDGE,"E83.trimOffspring"),sQuery(id+"F0.wireOp",EDGE,"E84.trimOffspring"),sQuery(id+"F0.wireOp",EDGE,"E85.trimOffspring"),sQuery(id+"F0.wireOp",EDGE,"E86.trimOffspring"),sQuery(id+"F0.wireOp",EDGE,"E87.trimOffspring"),sQuery(id+"F0.wireOp",EDGE,"E88.trimOffspring"),sQuery(id+"F0.wireOp",EDGE,"E89.trimOffspring"),sQuery(id+"F0.wireOp",EDGE,"E90.trimOffspring"),sQuery(id+"F0.wireOp",EDGE,"E91.trimOffspring"),sQuery(id+"F0.wireOp",EDGE,"E92.trimOffspring"),sQuery(id+"F0.wireOp",EDGE,"E93.trimOffspring"),sQuery(id+"F0.wireOp",EDGE,"E94")])],"isStart":false});
            var sketch = newSketch(context, id + "F5", { "sketchPlane" : qUnion([Q0])});
            skCircle(sketch, "E97", {"center": v(0, 0) * mm, "radius": 3.18 * mm});
            skSolve(sketch);
        }
        {
            var Q0;
            Q0 = qSketchRegion(id + "F5", true);
            extrude(context, id + "F6", {"entities" : qUnion([Q0]), "operationType" : NewBodyOperationType.ADD, "depth" : 5.08 * mm});
        }
    });
